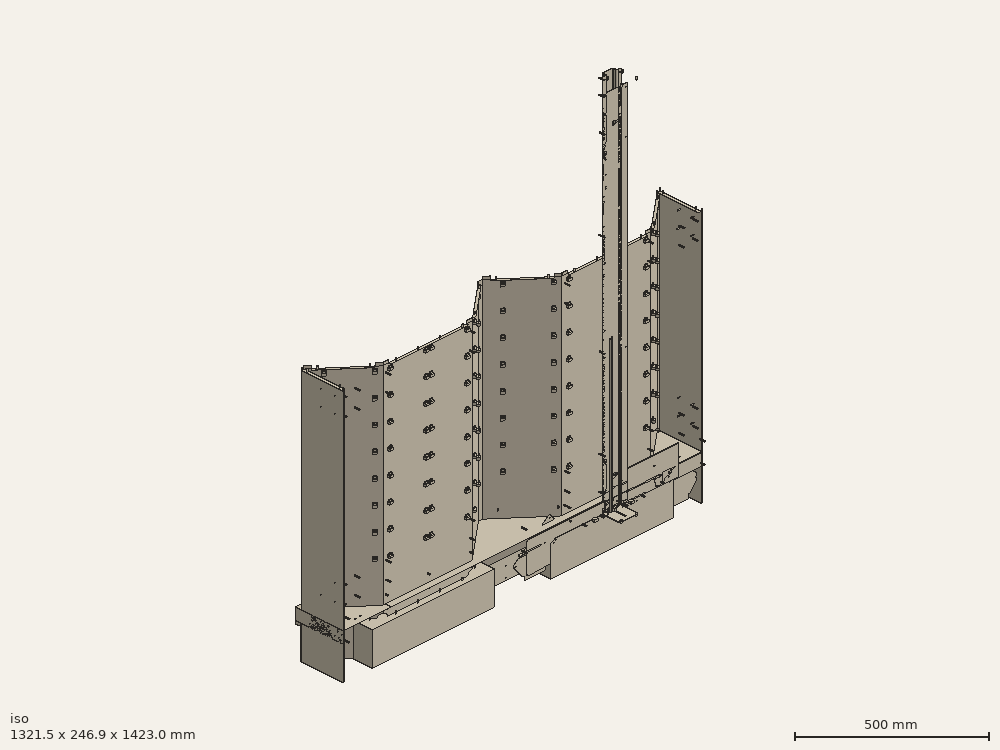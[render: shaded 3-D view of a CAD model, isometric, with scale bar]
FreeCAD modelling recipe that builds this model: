
FCSTD DOCUMENT  (FreeCAD 0.22R35209 (Git))
Label: composit_stand7
License: All rights reserved
LicenseURL: http://en.wikipedia.org/wiki/All_rights_reserved
objects: Sketcher::SketchObject×75, Part::FeaturePython×73, PartDesign::SubShapeBinder×27, Part::Compound×26, PartDesign::FeaturePython×20, PartDesign::Body×18, PartDesign::Pad×16, TechDraw::DrawViewPart×16, Part::Mirroring×15, PartDesign::Boolean×14, Part::Extrusion×12, PartDesign::Pocket×12, TechDraw::DrawViewDimension×10, PartDesign::Mirrored×9, App::DocumentObjectGroup×8, App::Part×5, TechDraw::DrawPage×5, PartDesign::Plane×4, Part::Part2DObjectPython×4, Part::Feature×4, +12 more types
note: 394 computed .brp shape members not serialized (recipe doc carries the construction recipe); baked Part::Feature solids carry a one-line shape summary decoded from their .brp
EXTERNAL_REF file=module.FCStd obj=Spreadsheet
EXTERNAL_REF file=module.FCStd obj=Sketch
EXTERNAL_REF file=dropper.FCStd obj=Part
EXTERNAL_REF file=module.FCStd obj=Body

FEATURE [Sketcher::SketchObject] Sketch  label="base_sketch"
  FullyConstrained = true
  expr: Constraints[19] = module#<<Properties>>.module_width * 2 + 2 mm
  expr: Constraints[20] = module#<<Properties>>.module_width + 2 mm
  sketch-geometry (11):
    g0: LineSegment StartX=0 StartY=21 StartZ=0 EndX=162.217 EndY=21 EndZ=0
    g1: LineSegment StartX=162.217 StartY=21 StartZ=0 EndX=319.002 EndY=154.059 EndZ=0
    g2: LineSegment StartX=0 StartY=57 StartZ=0 EndX=149 EndY=57 EndZ=0
    g3: LineSegment StartX=149 StartY=57 StartZ=0 EndX=263.366 EndY=154.059 EndZ=0
    g4: LineSegment StartX=149 StartY=21 StartZ=0 EndX=149 EndY=57 EndZ=0
    g5: LineSegment StartX=149 StartY=57 StartZ=0 EndX=172.294 EndY=29.5522 EndZ=0
    g6: LineSegment StartX=263.366 StartY=154.059 StartZ=0 EndX=286.66 EndY=126.611 EndZ=0
    g7: GeomPoint X=-149 Y=57 Z=0
    g8: GeomPoint X=-162.217 Y=21 Z=0
    g9: LineSegment StartX=162.217 StartY=21 StartZ=0 EndX=353.688 EndY=96 EndZ=0
    g10: LineSegment StartX=319.002 StartY=154.059 StartZ=0 EndX=263.366 EndY=154.059 EndZ=0
  constraints (35):
    c: Horizontal(g0)
    c: Coincident(g0,g1)
    c: PointOnObject(g0,g-2)
    c: DistanceY(g0) = 21  'offset'
    c: PointOnObject(g2,g-2)
    c: Horizontal(g2)
    c: Coincident(g2,g3)
    c: PointOnObject(g4,g0)
    c: Coincident(g4,g2)
    c: Coincident(g4,g5)
    c: PointOnObject(g5,g1)
    c: Perpendicular(g0,g4)
    c: Perpendicular(g1,g5)
    c: Equal(g4,g5)
    c: Perpendicular(g3,g5)
    c: Coincident(g6,g3)
    c: PointOnObject(g6,g1)
    c: Perpendicular(g3,g6)
    c: Symmetric(g7,g2,g-2)
    c: DistanceX(g7,g2) = 298
    c: Distance(g3) = 150
    c: DistanceY(g4,g4) = 36
    c: DistanceX(g0,g1) = 156.785
    c: DistanceX(g1) = 319.002  'width'
    c: Symmetric(g8,g0,g-2)
    c: DistanceX(g8,g0) = 324.434  'face_width'
    c: DistanceY(g1) = 154.059  'max_y'
    c: Coincident(g9,g0)
    c: Equal(g9,g1)
    c: DistanceY(g0,g9) = 75
    c: Angle(g9) = 0.373334
    c: Angle(g1) = 0.70372
    c: Coincident(g10,g3)
    c: Horizontal(g10)
    c: Coincident(g1,g10)
FEATURE [Part::Mirroring] Part__Mirroring  label="Sketch (Mirror #1)"
  Base = (0,0,0)
  Normal = (1,0,0)
  Source = -> Sketch
FEATURE [Part::FeaturePython] Connect  # WARN: FeaturePython — macro-defined, semantics opaque (R4)
  Objects = -> [Sketch,Part__Mirroring]
  Refine = true
  Tolerance = 0.0001
FEATURE [Sketcher::SketchObject] Sketch001  label="faces_bridge"
  ExternalGeometry = -> [Sketch]
  FullyConstrained = true
  sketch-geometry (3):
    g0: LineSegment StartX=319.002 StartY=154.059 StartZ=0 EndX=329.002 EndY=154.059 EndZ=0
    g1: LineSegment StartX=-319.002 StartY=154.059 StartZ=0 EndX=-326.502 EndY=154.059 EndZ=0
    g2: GeomPoint X=-334.002 Y=154.059 Z=0
  constraints (8):
    c: Coincident(g0,g-3)
    c: Horizontal(g0)
    c: Horizontal(g1)
    c: Symmetric(g1,g0,g-2)
    c: DistanceX(g1) = -326.502  'offset'
    c: Symmetric(g2,g1,g1)
    c: DistanceX(g2,g1) = 15
    c: DistanceX(g0,g0) = 10
FEATURE [Sketcher::SketchObject] Sketch002  label="wall"
  ExternalGeometry = -> [Sketch001]
  FullyConstrained = true
  sketch-geometry (1):
    g0: LineSegment StartX=329.002 StartY=154.059 StartZ=0 EndX=329.002 EndY=0 EndZ=0
  constraints (4):
    c: Coincident(g0,g-3)
    c: PointOnObject(g0,g-1)
    c: Vertical(g0)
    c: DistanceX(g0) = 329.002  'distance'
FEATURE [PartDesign::SubShapeBinder] Binder
  BindCopyOnChange = 0
  BindMode = 0
  ClaimChildren = true
  Context = -> Body [Binder.]
  Fuse = false
  MakeFace = true
  OffsetFill = false
  OffsetIntersection = false
  OffsetJoinType = 0
  OffsetOpenResult = false
  PartialLoad = false
  Placement = pos=(0,0,-115) rot=(0,0,1;0rad)
  Relative = false
  Support = -> [Connect002]
  _Version = 2
  expr: .Placement.Base.z = -<<Properties>>.bottom_extend
FEATURE [PartDesign::FeaturePython] BaseBend  # WARN: FeaturePython — macro-defined, semantics opaque (R4)
  BendSide = 0
  BendSketch = -> Binder
  MidPlane = false
  Reverse = false
  length = 870
  radius = 0.1
  thickness = 0.3
  expr: length = <<Properties>>.face_height - .BendSketch.Placement.Base.z * 1 mm
FEATURE [Spreadsheet::Sheet] Spreadsheet  label="Properties"
  cells = B2(number_of_modules)=8; C2(face_height)==755 mm; D2(rivet_d)==3.4 mm; E2(bottom_extend)==115 mm
FEATURE [Sketcher::SketchObject] Sketch003
  ExternalGeometry = -> [Sketch002]
  FullyConstrained = true
  sketch-geometry (1):
    g0: LineSegment StartX=326.002 StartY=0 StartZ=0 EndX=329.002 EndY=0 EndZ=0
  constraints (3):
    c: PointOnObject(g0,g-1)
    c: Coincident(g0,g-3)
    c: DistanceX(g0,g0) = 3
FEATURE [Part::FeaturePython] Connect001  # WARN: FeaturePython — macro-defined, semantics opaque (R4)
  Objects = -> [Connect,Sketch001,Sketch002,Sketch003]
  Tolerance = 0
FEATURE [Part::Mirroring] Part__Mirroring001  label="Connect001 (Mirror #2)"
  Base = (-326.502,0,0)
  Normal = (1,0,0)
  Source = -> Connect001
  expr: .Base.x = Sketch001.Constraints.offset
FEATURE [Part::FeaturePython] Connect002  # WARN: FeaturePython — macro-defined, semantics opaque (R4)
  Objects = -> [Connect001,Part__Mirroring001]
  Tolerance = 0
FEATURE [App::Link] Link  label="module_holes"
  LinkedObject = -> <external module.FCStd>#Sketch
FEATURE [Sketcher::SketchObject] Sketch004  label="modules_placements"
  ExternalGeometry = -> [Sketch]
  FullyConstrained = true
  sketch-geometry (14):
    g0: LineSegment StartX=0 StartY=57 StartZ=0 EndX=149 EndY=57 EndZ=0
    g1: LineSegment StartX=149 StartY=57 StartZ=0 EndX=262.604 EndY=153.412 EndZ=0
    g2: LineSegment StartX=149 StartY=21 StartZ=0 EndX=149 EndY=57 EndZ=0
    g3: LineSegment StartX=149 StartY=57 StartZ=0 EndX=172.294 EndY=29.5522 EndZ=0
    g4: LineSegment StartX=74.5 StartY=57 StartZ=0 EndX=74.5 EndY=21 EndZ=0
    g5: LineSegment StartX=205.802 StartY=105.206 StartZ=0 EndX=229.096 EndY=77.758 EndZ=0
    g6: LineSegment StartX=64.5 StartY=21 StartZ=0 EndX=74.5 EndY=21 EndZ=0
    g7: LineSegment StartX=74.5 StartY=21 StartZ=0 EndX=74.5 EndY=41 EndZ=0
    g8: LineSegment StartX=221.472 StartY=71.2874 StartZ=0 EndX=229.096 EndY=77.758 EndZ=0
    g9: LineSegment StartX=229.096 StartY=77.758 StartZ=0 EndX=216.155 EndY=93.0068 EndZ=0
    g10: LineSegment StartX=-84.5 StartY=21 StartZ=0 EndX=-74.5 EndY=21 EndZ=0
    g11: LineSegment StartX=-74.5 StartY=21 StartZ=0 EndX=-74.5 EndY=41 EndZ=0
    g12: LineSegment StartX=-236.72 StartY=84.2286 StartZ=0 EndX=-229.096 EndY=77.758 EndZ=0
    g13: LineSegment StartX=-229.096 StartY=77.758 StartZ=0 EndX=-216.155 EndY=93.0068 EndZ=0
  constraints (42):
    c: PointOnObject(g0,g-2)
    c: Horizontal(g0)
    c: Coincident(g1,g0)
    c: PointOnObject(g2,g-3)
    c: Coincident(g2,g0)
    c: Coincident(g2,g3)
    c: PointOnObject(g3,g-4)
    c: Perpendicular(g1,g3)
    c: Perpendicular(g-4,g3)
    c: Perpendicular(g0,g2)
    c: Equal(g3,g2)
    c: DistanceY(g2,g2) = 36
    c: PointOnObject(g4,g-3)
    c: Vertical(g4)
    c: PointOnObject(g5,g-4)
    c: Equal(g0,g1)
    c: Symmetric(g0,g1,g5)
    c: Perpendicular(g1,g5)
    c: Symmetric(g0,g0,g4)
    c: PointOnObject(g6,g-3)
    c: Coincident(g6,g4)
    c: Coincident(g6,g7)
    c: PointOnObject(g7,g4)
    c: PointOnObject(g8,g-4)
    c: Coincident(g8,g5)
    c: Coincident(g8,g9)
    c: PointOnObject(g9,g5)
    c: Equal(g6,g8)
    c: Equal(g7,g9)
    c: Distance(g6) = 10
    c: DistanceY(g7,g7) = 20
    c: Horizontal(g10)
    c: Coincident(g10,g11)
    c: Vertical(g11)
    c: Coincident(g12,g13)
    c: Perpendicular(g13,g12)
    c: Symmetric(g8,g12,g-2)
    c: Symmetric(g10,g6,g-2)
    c: Equal(g11,g7)
    c: Equal(g10,g6)
    c: Equal(g12,g8)
    c: Symmetric(g13,g9,g-2)
FEATURE [Part::Extrusion] Extrude
  Base = -> Link
  Dir = (0,0,1)
  DirMode = 2
  FaceMakerClass = Part::FaceMakerBullseye
  LengthFwd = 10
  LengthRev = 0
  Placement = pos=(0,0,0) rot=(1,0,0;1.5708rad)
  Solid = true
  Symmetric = false
FEATURE [PartDesign::Body] Body001  label="dummy_body"
  Origin = -> Origin001
FEATURE [Part::FeaturePython] Placment  # WARN: FeaturePython — macro-defined, semantics opaque (R4)
  AttacherType = Attacher::AttachEngine3D
  ExposePlacement = true
  MapMode = 49
  MarkerShape = 1
  MarkerSize = 20
  NumElements = 1
  Placement = pos=(74.5,21,0) rot=(0,0,1;0rad)
  Support = -> [Sketch004]
  Type = lattice2AttachablePlacement.AttachablePlacement
  isLattice = 1
FEATURE [Part::FeaturePython] PlacementSubsequence  # WARN: FeaturePython — macro-defined, semantics opaque (R4)
  Base = -> Placment
  CycleMode = 0
  ExposePlacement = false
  MarkerShape = 1
  MarkerSize = 0
  NumElements = 4
  Type = lattice2AttachablePlacement.AttachedPlacementSubsequence
  isLattice = 1
FEATURE [Part::FeaturePython] LinearArray  # WARN: FeaturePython — macro-defined, semantics opaque (R4)
  Alignment = 0
  CellStart = A1
  Count = 8
  Dir = (0,0,1)
  DirIsDriven = true
  DistributionLaw = 0
  DrivenProperty = 1
  EndInclusive = true
  ExposePlacement = false
  GeneratorMode = 1
  MarkerShape = 1
  MarkerSize = 0
  NumElements = 8
  OrientMode = 0
  Point = (0,0,0)
  PointIsDriven = true
  Reverse = false
  SpanEnd = 100
  SpanStart = 180
  Step = 80
  Type = lattice2LinearArray.LinearArray
  VSGVersion = 1
  Values = 180.0 | 260.0 | 340.0 | 420.0 | 500.0 | 580.0 | 660.0 | 740.0
  ValuesSource = 2
  isLattice = 1
  expr: Count = <<Properties>>.number_of_modules
  expr: Step = <<module>>#<<Properties>>.module_fixture_distance_y
FEATURE [Part::FeaturePython] Join  # WARN: FeaturePython — macro-defined, semantics opaque (R4)
  ExposePlacement = false
  Interleave = false
  Links = -> [PlacementSubsequence]
  MarkerShape = 1
  MarkerSize = 0
  NumElements = 4
  Type = lattice2JoinArrays.JoinArrays
  isLattice = 1
FEATURE [Part::FeaturePython] LinearArray001  label="faces_placements"  # WARN: FeaturePython — macro-defined, semantics opaque (R4)
  Alignment = 0
  CellStart = A1
  Count = 2
  Dir = (1,0,0)
  DirIsDriven = true
  DistributionLaw = 0
  DrivenProperty = 1
  EndInclusive = true
  ExposePlacement = false
  GeneratorMode = 0
  MarkerShape = 1
  MarkerSize = 0
  NumElements = 2
  OrientMode = 1
  Point = (0,0,0)
  PointIsDriven = true
  Reverse = false
  SpanEnd = -653.005
  SpanStart = 0
  Step = -653.005
  Type = lattice2LinearArray.LinearArray
  VSGVersion = 1
  Values = 0.0 | -653.0048374651761
  ValuesSource = 2
  isLattice = 1
  expr: SpanEnd = Sketch001.Constraints.offset * 2
FEATURE [Part::FeaturePython] Populate002  label="Populate LinearArray001 with Join"  # WARN: FeaturePython — macro-defined, semantics opaque (R4)
  Copying = 0
  ExposePlacement = false
  MarkerShape = 1
  MarkerSize = 0
  NumElements = 8
  Object = -> Join
  OutputCompounding = 0
  PlacementsTo = -> LinearArray001
  Referencing = 0
  Type = lattice2PopulateCopies.LatticePopulateCopies
  isLattice = 1
FEATURE [Part::FeaturePython] Populate  label="Populate Join001 with LinearArray"  # WARN: FeaturePython — macro-defined, semantics opaque (R4)
  Copying = 0
  ExposePlacement = false
  MarkerShape = 1
  MarkerSize = 0
  NumElements = 64
  Object = -> Populate002
  OutputCompounding = 0
  PlacementsTo = -> LinearArray
  Referencing = 0
  Type = lattice2PopulateCopies.LatticePopulateCopies
  isLattice = 1
FEATURE [Part::FeaturePython] Populate001  label="Populate Populate Join001 with LinearArray with Extrude"  # WARN: FeaturePython — macro-defined, semantics opaque (R4)
  Copying = 0
  ExposePlacement = false
  MarkerShape = 1
  MarkerSize = 0
  NumElements = 0
  Object = -> Extrude
  OutputCompounding = 1
  PlacementsTo = -> Populate
  Referencing = 0
  Type = lattice2PopulateCopies.LatticePopulateCopies
  isLattice = 0
FEATURE [PartDesign::FeaturePython] Extend  # WARN: FeaturePython — macro-defined, semantics opaque (R4)
  BaseFeature = -> BaseBend
  Offset = 0.02
  Refine = true
  UseSubtraction = false
  baseObject = -> BaseBend [Face1]
  gap1 = 0
  gap2 = 0
  length = 0
FEATURE [PartDesign::FeaturePython] Bend  # WARN: FeaturePython — macro-defined, semantics opaque (R4)
  AutoMiter = false
  BaseFeature = -> Extend
  BendType = 0
  LengthList = [0.1]
  LengthSpec = 0
  ReliefFactor = 0.7
  UseReliefFactor = false
  angle = 90
  baseObject = -> Extend [Edge17,Edge49,Edge199,Edge78,Edge108,Edge203,Edge138,Edge171]
  bendAList = [90]
  extend1 = 0
  extend2 = 0
  gap1 = 0
  gap2 = 0
  invert = false
  kfactor = 0.5
  length = 0.1
  maxExtendDist = 5
  minGap = 0.1
  minReliefGap = 1
  miterangle1 = 0
  miterangle2 = 0
  offset = 0
  radius = 0.1
  reliefType = 0
  reliefd = 1
  reliefw = 0.8
  sketchflip = false
  sketchinvert = false
  unfold = false
  expr: radius = BaseBend.radius
FEATURE [Sketcher::SketchObject] Sketch005  label="top_fix_lines"
  ExternalGeometry = -> [Sketch,Sketch002]
  FullyConstrained = true
  sketch-geometry (8):
    g0: LineSegment StartX=142.217 StartY=21 StartZ=0 EndX=142.217 EndY=20.5 EndZ=0
    g1: LineSegment StartX=177.466 StartY=33.9412 StartZ=0 EndX=177.789 EndY=33.56 EndZ=0
    g2: LineSegment StartX=303.754 StartY=141.118 StartZ=0 EndX=304.077 EndY=140.736 EndZ=0
    g3: LineSegment StartX=162.217 StartY=21 StartZ=0 EndX=177.466 EndY=33.9412 EndZ=0
    g4: LineSegment StartX=162.217 StartY=21 StartZ=0 EndX=142.217 EndY=21 EndZ=0
    g5: LineSegment StartX=319.002 StartY=154.059 StartZ=0 EndX=303.754 EndY=141.118 EndZ=0
    g6: LineSegment StartX=328.502 StartY=151.059 StartZ=0 EndX=329.002 EndY=151.059 EndZ=0
    g7: LineSegment StartX=328.502 StartY=2 StartZ=0 EndX=329.002 EndY=2 EndZ=0
  constraints (26):
    c: Vertical(g0)
    c: PointOnObject(g1,g-3)
    c: PointOnObject(g2,g-3)
    c: Perpendicular(g-3,g1)
    c: Perpendicular(g-3,g2)
    c: Equal(g0,g1)
    c: Equal(g1,g2)
    c: Horizontal(g0,g-3)
    c: DistanceY(g0,g0) = 0.5
    c: Distance(g-3,g1) = 20
    c: Coincident(g3,g-3)
    c: Coincident(g3,g1)
    c: Coincident(g4,g3)
    c: Coincident(g4,g0)
    c: Coincident(g5,g-3)
    c: Coincident(g5,g2)
    c: Equal(g5,g3)
    c: Equal(g3,g4)
    c: PointOnObject(g6,g-4)
    c: PointOnObject(g7,g-4)
    c: Equal(g2,g6)
    c: Equal(g6,g7)
    c: DistanceY(g-4,g7) = 2
    c: DistanceY(g6,g-4) = 3
    c: Horizontal(g7)
    c: Horizontal(g6)
FEATURE [Sketcher::SketchObject] Sketch006
  ExternalGeometry = -> [Sketch,Sketch005]
  FullyConstrained = true
  sketch-geometry (15):
    g0: LineSegment StartX=162.209 StartY=20.9935 StartZ=0 EndX=177.466 EndY=33.9412 EndZ=0
    g1: LineSegment StartX=177.466 StartY=33.9412 StartZ=0 EndX=177.789 EndY=33.56 EndZ=0
    g2: LineSegment StartX=177.789 StartY=33.56 StartZ=0 EndX=162.533 EndY=20.6123 EndZ=0
    g3: LineSegment StartX=162.533 StartY=20.6123 StartZ=0 EndX=162.209 EndY=20.9935 EndZ=0
    g4: LineSegment StartX=162.207 StartY=21 StartZ=0 EndX=142.217 EndY=21 EndZ=0
    g5: LineSegment StartX=142.217 StartY=21 StartZ=0 EndX=142.217 EndY=20.5 EndZ=0
    g6: LineSegment StartX=142.217 StartY=20.5 StartZ=0 EndX=162.207 EndY=20.5 EndZ=0
    g7: LineSegment StartX=162.207 StartY=20.5 StartZ=0 EndX=162.207 EndY=21 EndZ=0
    g8: LineSegment StartX=304.077 StartY=140.736 StartZ=0 EndX=319.318 EndY=153.671 EndZ=0
    g9: LineSegment StartX=319.318 StartY=153.671 StartZ=0 EndX=318.995 EndY=154.052 EndZ=0
    g10: LineSegment StartX=318.995 StartY=154.052 StartZ=0 EndX=303.754 EndY=141.118 EndZ=0
    g11: LineSegment StartX=303.754 StartY=141.118 StartZ=0 EndX=304.077 EndY=140.736 EndZ=0
    g12: LineSegment StartX=162.207 StartY=21 StartZ=0 EndX=162.217 EndY=21 EndZ=0
    g13: LineSegment StartX=162.217 StartY=21 StartZ=0 EndX=162.209 EndY=20.9935 EndZ=0
    g14: LineSegment StartX=318.995 StartY=154.052 StartZ=0 EndX=319.002 EndY=154.059 EndZ=0
  constraints (39):
    c: Coincident(g0,g1)
    c: Coincident(g1,g2)
    c: Coincident(g2,g3)
    c: Parallel(g0,g2)
    c: Parallel(g1,g3)
    c: Coincident(g4,g5)
    c: Coincident(g5,g6)
    c: Coincident(g6,g7)
    c: Coincident(g7,g4)
    c: Parallel(g4,g6)
    c: Parallel(g5,g7)
    c: Coincident(g8,g9)
    c: Coincident(g9,g10)
    c: Coincident(g10,g11)
    c: Coincident(g11,g8)
    c: Parallel(g8,g10)
    c: Parallel(g9,g11)
    c: Perpendicular(g1,g0)
    c: Perpendicular(g9,g8)
    c: Perpendicular(g5,g4)
    c: Coincident(g10,g-6)
    c: PointOnObject(g-6,g8)
    c: Coincident(g0,g-5)
    c: PointOnObject(g-5,g2)
    c: Coincident(g4,g-4)
    c: PointOnObject(g-4,g6)
    c: PointOnObject(g4,g-3)
    c: Coincident(g3,g0)
    c: PointOnObject(g0,g-7)
    c: Coincident(g12,g4)
    c: Coincident(g12,g-7)
    c: Coincident(g13,g12)
    c: Coincident(g13,g0)
    c: Equal(g12,g13)
    c: PointOnObject(g9,g-7)
    c: Coincident(g14,g9)
    c: Coincident(g14,g-7)
    c: Equal(g14,g13)
    c: DistanceX(g12,g12) = 0.01
FEATURE [Part::Mirroring] Part__Mirroring002  label="Sketch006 (Mirror #3)"
  Base = (0,0,0)
  Normal = (1,0,0)
  Source = -> Sketch006
FEATURE [Part::Compound] Compound001
  Links = -> [Sketch006,Part__Mirroring002]
FEATURE [Part::FeaturePython] Populate003  label="Populate LinearArray001 with Compound001"  # WARN: FeaturePython — macro-defined, semantics opaque (R4)
  Copying = 0
  ExposePlacement = false
  MarkerShape = 1
  MarkerSize = 0
  NumElements = 0
  Object = -> Compound001
  OutputCompounding = 1
  PlacementsTo = -> LinearArray001
  Referencing = 0
  Type = lattice2PopulateCopies.LatticePopulateCopies
  isLattice = 0
FEATURE [Sketcher::SketchObject] Sketch007
  ExternalGeometry = -> [Sketch002,Sketch005]
  FullyConstrained = true
  sketch-geometry (8):
    g0: LineSegment StartX=329.002 StartY=154.059 StartZ=0 EndX=328.502 EndY=154.059 EndZ=0
    g1: LineSegment StartX=328.502 StartY=154.059 StartZ=0 EndX=328.502 EndY=151.059 EndZ=0
    g2: LineSegment StartX=328.502 StartY=151.059 StartZ=0 EndX=329.002 EndY=151.059 EndZ=0
    g3: LineSegment StartX=329.002 StartY=151.059 StartZ=0 EndX=329.002 EndY=154.059 EndZ=0
    g4: LineSegment StartX=329.002 StartY=0 StartZ=0 EndX=328.502 EndY=0 EndZ=0
    g5: LineSegment StartX=328.502 StartY=0 StartZ=0 EndX=328.502 EndY=2 EndZ=0
    g6: LineSegment StartX=328.502 StartY=2 StartZ=0 EndX=329.002 EndY=2 EndZ=0
    g7: LineSegment StartX=329.002 StartY=2 StartZ=0 EndX=329.002 EndY=0 EndZ=0
  constraints (19):
    c: Coincident(g0,g1)
    c: Coincident(g1,g2)
    c: Coincident(g2,g3)
    c: Coincident(g3,g0)
    c: Horizontal(g0)
    c: Vertical(g1)
    c: Coincident(g0,g-3)
    c: Coincident(g4,g5)
    c: Coincident(g5,g6)
    c: Coincident(g6,g7)
    c: Coincident(g7,g4)
    c: Horizontal(g4)
    c: Horizontal(g6)
    c: Vertical(g5)
    c: Vertical(g7)
    c: Coincident(g4,g-3)
    c: Coincident(g2,g-4)
    c: Coincident(g1,g-4)
    c: Coincident(g5,g-5)
FEATURE [Part::Mirroring] Part__Mirroring003  label="Sketch007 (Mirror #4)"
  Base = (-326.502,0,0)
  Normal = (1,0,0)
  Source = -> Sketch007
  expr: .Base.x = Sketch001.Constraints.offset
FEATURE [Part::Compound] Compound002
  Links = -> [Sketch007,Populate003,Part__Mirroring003]
FEATURE [Part::Extrusion] Extrude001
  Base = -> Compound002
  Dir = (0,0,1)
  DirMode = 2
  FaceMakerClass = Part::FaceMakerBullseye
  LengthFwd = 10
  LengthRev = 0
  Placement = pos=(0,0,755) rot=(0,0,1;0rad)
  Solid = true
  Symmetric = false
  expr: .Placement.Base.z = <<Properties>>.face_height
FEATURE [Sketcher::SketchObject] Sketch008
  ExternalGeometry = -> [Sketch005]
  FullyConstrained = true
  sketch-geometry (7):
    g0: LineSegment StartX=182.966 StartY=27.4604 StartZ=0 EndX=309.254 EndY=134.637 EndZ=0
    g1: LineSegment StartX=309.254 StartY=134.637 StartZ=0 EndX=304.077 EndY=140.736 EndZ=0
    g2: LineSegment StartX=304.077 StartY=140.736 StartZ=0 EndX=177.789 EndY=33.56 EndZ=0
    g3: LineSegment StartX=177.789 StartY=33.56 StartZ=0 EndX=182.966 EndY=27.4604 EndZ=0
    g4: LineSegment StartX=142.217 StartY=20.5 StartZ=0 EndX=0 EndY=20.5 EndZ=0
    g5: LineSegment StartX=0 StartY=12.5 StartZ=0 EndX=142.217 EndY=12.5 EndZ=0
    g6: LineSegment StartX=142.217 StartY=12.5 StartZ=0 EndX=142.217 EndY=20.5 EndZ=0
  constraints (19):
    c: Coincident(g0,g1)
    c: Coincident(g1,g2)
    c: Coincident(g2,g3)
    c: Coincident(g3,g0)
    c: Parallel(g0,g2)
    c: Parallel(g1,g3)
    c: Perpendicular(g1,g0)
    c: Coincident(g1,g-5)
    c: Coincident(g2,g-4)
    c: Coincident(g5,g6)
    c: Coincident(g6,g4)
    c: Horizontal(g4)
    c: Horizontal(g5)
    c: Vertical(g6)
    c: Coincident(g4,g-3)
    c: PointOnObject(g5,g-2)
    c: PointOnObject(g4,g-2)
    c: Equal(g6,g3)
    c: DistanceY(g6,g6) = 8
FEATURE [Sketcher::SketchObject] Sketch009
  ExternalGeometry = -> [Sketch005]
  FullyConstrained = true
  sketch-geometry (6):
    g0: LineSegment StartX=328.502 StartY=151.059 StartZ=0 EndX=324.502 EndY=151.059 EndZ=0
    g1: LineSegment StartX=318.502 StartY=145.059 StartZ=0 EndX=318.502 EndY=2 EndZ=0
    g2: LineSegment StartX=318.502 StartY=2 StartZ=0 EndX=328.502 EndY=2 EndZ=0
    g3: LineSegment StartX=328.502 StartY=2 StartZ=0 EndX=328.502 EndY=151.059 EndZ=0
    g4: ArcOfCircle CenterX=324.502 CenterY=145.059 CenterZ=0 NormalX=0 NormalY=0 NormalZ=1 AngleXU=0 Radius=6 StartAngle=1.5708 EndAngle=3.14159
    g5: GeomPoint X=318.502 Y=151.059 Z=0
  constraints (14):
    c: Coincident(g1,g2)
    c: Coincident(g2,g3)
    c: Coincident(g3,g0)
    c: Horizontal(g0)
    c: Horizontal(g2)
    c: Vertical(g1)
    c: Coincident(g0,g-4)
    c: Coincident(g2,g-3)
    c: DistanceX(g2,g2) = 10
    c: PointOnObject(g5,g0)
    c: PointOnObject(g5,g1)
    c: Tangent(g0,g4) = -1.5708
    c: Tangent(g1,g4) = -1.5708
    c: Radius(g4) = 6
FEATURE [Part::Mirroring] Part__Mirroring004  label="Sketch008 (Mirror #5)"
  Base = (0,0,0)
  Normal = (1,0,0)
  Source = -> Sketch008
FEATURE [Part::Compound] Compound003
  Links = -> [Part__Mirroring004,Sketch008]
FEATURE [Part::FeaturePython] Populate004  label="Populate LinearArray001 with Compound003"  # WARN: FeaturePython — macro-defined, semantics opaque (R4)
  Copying = 0
  ExposePlacement = false
  MarkerShape = 1
  MarkerSize = 0
  NumElements = 0
  Object = -> Compound003
  OutputCompounding = 1
  PlacementsTo = -> LinearArray001
  Referencing = 0
  Type = lattice2PopulateCopies.LatticePopulateCopies
  isLattice = 0
FEATURE [Part::FeaturePython] Mirror  label="Mirror of Sketch009"  # WARN: FeaturePython — macro-defined, semantics opaque (R4)
  ExposePlacement = false
  FlipX = true
  FlipY = false
  FlipZ = false
  MarkerShape = 1
  MarkerSize = 0
  NumElements = 0
  Object = -> Sketch009
  ObjectTraversal = 0
  PivotPlacement = pos=(-326.502,0,0) rot=(0,0,1;0rad)
  Type = lattice2Mirror.LatticeMirror
  isLattice = 0
  expr: .PivotPlacement.Base.x = Sketch001.Constraints.offset
FEATURE [Part::Compound] Compound004
  Links = -> [Sketch009,Populate004,Mirror]
FEATURE [PartDesign::SubShapeBinder] Binder001
  BindCopyOnChange = 0
  BindMode = 0
  ClaimChildren = true
  Context = -> Body [Binder001.]
  Fuse = false
  MakeFace = true
  OffsetFill = false
  OffsetIntersection = false
  OffsetJoinType = 0
  OffsetOpenResult = false
  PartialLoad = false
  Placement = pos=(0,0,755.1) rot=(0,0,1;0rad)
  Relative = false
  Support = -> [Compound004]
  _Version = 2
  expr: .Placement.Base.z = <<Properties>>.face_height + <<BaseBend>>.radius
FEATURE [PartDesign::Pad] Pad
  BaseFeature = -> Bend
  Direction = (0,0,1)
  Length = 0.3
  Length2 = 10
  Profile = -> Binder001
  Type = 0
  expr: Length = <<BaseBend>>.thickness
FEATURE [Sketcher::SketchObject] Sketch010  label="top_base_sketch"
  ExternalGeometry = -> [Sketch]
  FullyConstrained = true
  Placement = pos=(0,0,0) rot=(0.57735,0.57735,0.57735;2.0944rad)
  sketch-geometry (2):
    g0: LineSegment StartX=-10 StartY=0 StartZ=0 EndX=154.059 EndY=0 EndZ=0
    g1: LineSegment StartX=154.059 StartY=0 StartZ=0 EndX=158.226 EndY=23.6354 EndZ=0
  constraints (6):
    c: Coincident(g0,g-3)
    c: Coincident(g1,g0)
    c: Angle(g1) = 1.39626
    c: PointOnObject(g0,g-1)
    c: DistanceX(g0) = -10
    c: Distance(g1) = 24
FEATURE [PartDesign::FeaturePython] BaseBend001  # WARN: FeaturePython — macro-defined, semantics opaque (R4)
  BendSide = 1
  BendSketch = -> Sketch010
  MidPlane = true
  Reverse = false
  length = 638.005
  radius = 0.1
  thickness = 0.3
  expr: length = <<base_sketch>>.Constraints.width * 2
FEATURE [Sketcher::SketchObject] Sketch011  label="top_cut"
  ExternalGeometry = -> [Sketch]
  FullyConstrained = true
  sketch-geometry (4):
    g0: LineSegment StartX=0 StartY=9 StartZ=0 EndX=166.623 EndY=9 EndZ=0
    g1: LineSegment StartX=166.623 StartY=9 StartZ=0 EndX=319.002 EndY=138.32 EndZ=0
    g2: LineSegment StartX=162.217 StartY=9 StartZ=0 EndX=162.217 EndY=21 EndZ=0
    g3: LineSegment StartX=162.217 StartY=21 StartZ=0 EndX=169.982 EndY=11.8507 EndZ=0
  constraints (13):
    c: PointOnObject(g0,g-2)
    c: Horizontal(g0)
    c: Coincident(g1,g0)
    c: PointOnObject(g2,g0)
    c: Coincident(g2,g-4)
    c: Coincident(g2,g3)
    c: PointOnObject(g3,g1)
    c: Perpendicular(g0,g2)
    c: Perpendicular(g1,g3)
    c: Perpendicular(g-3,g3)
    c: Equal(g3,g2)
    c: DistanceY(g2,g2) = 12
    c: Vertical(g1,g-3)
FEATURE [Sketcher::SketchObject] Sketch012
  ExternalGeometry = -> [Sketch011]
  FullyConstrained = false
  sketch-geometry (2):
    g0: LineSegment StartX=319.002 StartY=138.32 StartZ=0 EndX=319.002 EndY=-34.0475 EndZ=0
    g1: LineSegment StartX=319.002 StartY=-34.0475 StartZ=0 EndX=0 EndY=-34.0475 EndZ=0
  constraints (5):
    c: Coincident(g0,g-4)
    c: Vertical(g0)
    c: Coincident(g1,g0)
    c: PointOnObject(g1,g-2)
    c: Horizontal(g1)
FEATURE [Part::FeaturePython] Connect003  # WARN: FeaturePython — macro-defined, semantics opaque (R4)
  Objects = -> [Sketch011,Sketch012]
  Tolerance = 0
FEATURE [Part::Mirroring] Part__Mirroring005  label="Connect003 (Mirror #6)"
  Base = (0,0,0)
  Normal = (1,0,0)
  Source = -> Connect003
FEATURE [Part::FeaturePython] Connect004  # WARN: FeaturePython — macro-defined, semantics opaque (R4)
  Objects = -> [Connect003,Part__Mirroring005]
  Tolerance = 0
FEATURE [PartDesign::SubShapeBinder] Binder002
  BindCopyOnChange = 0
  BindMode = 0
  ClaimChildren = true
  Context = -> Part [Body002.Binder002.]
  Fuse = false
  MakeFace = true
  OffsetFill = false
  OffsetIntersection = false
  OffsetJoinType = 0
  OffsetOpenResult = false
  PartialLoad = false
  Relative = false
  Support = -> [Connect004]
  _Version = 2
FEATURE [PartDesign::Pocket] Pocket
  BaseFeature = -> BaseBend001
  Direction = (0,0,-1)
  Length = 5
  Length2 = 5
  Midplane = true
  Profile = -> Binder002
  Refine = true
  Type = 1
FEATURE [PartDesign::FeaturePython] Bend001  # WARN: FeaturePython — macro-defined, semantics opaque (R4)
  AutoMiter = false
  BaseFeature = -> Pocket
  BendType = 1
  LengthList = [20]
  LengthSpec = 0
  ReliefFactor = 0.7
  UseReliefFactor = false
  angle = 90
  baseObject = -> Pocket [Edge27,Edge29,Edge32,Edge33,Edge26]
  bendAList = [90]
  extend1 = 0
  extend2 = 0
  gap1 = 0
  gap2 = 0
  invert = false
  kfactor = 0.5
  length = 20
  maxExtendDist = 5
  minGap = 0.1
  minReliefGap = 1
  miterangle1 = 0
  miterangle2 = 0
  offset = 0
  radius = 0.1
  reliefType = 0
  reliefd = 1
  reliefw = 0.8
  sketchflip = false
  sketchinvert = false
  unfold = false
  expr: radius = BaseBend001.radius
FEATURE [PartDesign::SubShapeBinder] Binder003
  BindCopyOnChange = 0
  BindMode = 0
  ClaimChildren = false
  Context = -> Part [Body002.Binder003.]
  Fuse = false
  MakeFace = true
  OffsetFill = false
  OffsetIntersection = false
  OffsetJoinType = 0
  OffsetOpenResult = false
  PartialLoad = false
  Relative = true
  Support = -> [Sketch,Sketch011]
  _Version = 2
  expr: Support = list(<<top_cut>>._self; <<base_sketch>>._self)
FEATURE [Sketcher::SketchObject] Sketch013
  ExternalGeometry = -> [Binder003]
  FullyConstrained = true
  MapMode = 5
  Support = -> [XY_Plane003]
  sketch-geometry (12):
    g0: LineSegment StartX=167.462 StartY=9.71268 StartZ=0 EndX=165.521 EndY=12 EndZ=0
    g1: LineSegment StartX=165.521 StartY=12 StartZ=0 EndX=165.521 EndY=9 EndZ=0
    g2: LineSegment StartX=165.521 StartY=9 StartZ=0 EndX=166.623 EndY=9 EndZ=0
    g3: LineSegment StartX=166.623 StartY=9 StartZ=0 EndX=167.462 EndY=9.71268 EndZ=0
    g4: LineSegment StartX=319.002 StartY=138.32 StartZ=0 EndX=319.002 EndY=138.32 EndZ=0
    g5: LineSegment StartX=319.002 StartY=138.32 StartZ=0 EndX=317.061 EndY=140.607 EndZ=0
    g6: LineSegment StartX=317.061 StartY=140.607 StartZ=0 EndX=319.002 EndY=138.32 EndZ=0
    g7: LineSegment StartX=319.002 StartY=138.32 StartZ=0 EndX=319.002 EndY=138.32 EndZ=0
    g8: LineSegment StartX=319.002 StartY=153.759 StartZ=0 EndX=318.602 EndY=153.759 EndZ=0
    g9: LineSegment StartX=318.602 StartY=153.759 StartZ=0 EndX=318.602 EndY=150.759 EndZ=0
    g10: LineSegment StartX=318.602 StartY=150.759 StartZ=0 EndX=319.002 EndY=150.759 EndZ=0
    g11: LineSegment StartX=319.002 StartY=150.759 StartZ=0 EndX=319.002 EndY=153.759 EndZ=0
  constraints (34):
    c: Coincident(g0,g1)
    c: Coincident(g1,g2)
    c: Coincident(g3,g0)
    c: Coincident(g5,g6)
    c: Coincident(g6,g7)
    c: Perpendicular(g4,g5)
    c: Perpendicular(g7,g6)
    c: Equal(g0,g1)
    c: Equal(g1,g5)
    c: Equal(g5,g6)
    c: Coincident(g8,g9)
    c: Coincident(g9,g10)
    c: Coincident(g10,g11)
    c: Horizontal(g8)
    c: Horizontal(g10)
    c: Vertical(g9)
    c: Vertical(g11)
    c: Equal(g11,g6)
    c: Coincident(g2,g3)
    c: Coincident(g2,g-4)
    c: PointOnObject(g0,g-4)
    c: Horizontal(g2)
    c: Perpendicular(g2,g1)
    c: Perpendicular(g3,g0)
    c: DistanceY(g1,g1) = 3
    c: DistanceX(g10,g10) = 0.4
    c: Coincident(g11,g8)
    c: Vertical(g8,g-3)
    c: DistanceY(g8,g-3) = 0.3
    c: Coincident(g7,g4)
    c: Coincident(g5,g4)
    c: PointOnObject(g6,g-4)
    c: Coincident(g4,g-4)
    c: Vertical(g4)
FEATURE [PartDesign::Pocket] Pocket001
  BaseFeature = -> Bend001
  Direction = (0,0,-1)
  Length = 5
  Length2 = 5
  Profile = -> Sketch013
  ReferenceAxis = -> Sketch013 [N_Axis]
  Reversed = true
  Type = 1
FEATURE [PartDesign::Mirrored] Mirrored
  BaseFeature = -> Pocket001
  MirrorPlane = -> Sketch013 [V_Axis]
  Originals = -> [Pocket001]
FEATURE [Sketcher::SketchObject] Sketch014
  ExternalGeometry = -> [Sketch005]
  FullyConstrained = true
  expr: Constraints[10] = <<Properties>>.rivet_d
  expr: Constraints[34] = <<Properties>>.rivet_d / 2 + 3 mm + 1 mm
  sketch-geometry (16):
    g0: LineSegment StartX=142.217 StartY=21 StartZ=0 EndX=0 EndY=21 EndZ=0
    g1: LineSegment StartX=177.466 StartY=33.9412 StartZ=0 EndX=303.754 EndY=141.118 EndZ=0
    g2: Circle CenterX=122.217 CenterY=15.3 CenterZ=0 NormalX=0 NormalY=0 NormalZ=1 AngleXU=0 Radius=1.7
    g3: Circle CenterX=40.739 CenterY=15.3 CenterZ=0 NormalX=0 NormalY=0 NormalZ=1 AngleXU=0 Radius=1.7
    g4: Circle CenterX=192.591 CenterY=39.3011 CenterZ=0 NormalX=0 NormalY=0 NormalZ=1 AngleXU=0 Radius=1.7
    g5: Circle CenterX=296.005 CenterY=127.066 CenterZ=0 NormalX=0 NormalY=0 NormalZ=1 AngleXU=0 Radius=1.7
    g6: Circle CenterX=0 CenterY=0 CenterZ=0 NormalX=0 NormalY=0 NormalZ=1 AngleXU=0 Radius=1.7
    g7: LineSegment StartX=0 StartY=15.3 StartZ=0 EndX=40.739 EndY=15.3 EndZ=0
    g8: LineSegment StartX=40.739 StartY=15.3 StartZ=0 EndX=81.478 EndY=15.3 EndZ=0
    g9: LineSegment StartX=81.478 StartY=15.3 StartZ=0 EndX=122.217 EndY=15.3 EndZ=0
    g10: LineSegment StartX=122.217 StartY=15.3 StartZ=0 EndX=142.217 EndY=15.3 EndZ=0
    g11: LineSegment StartX=122.217 StartY=15.3 StartZ=0 EndX=122.217 EndY=21 EndZ=0
    g12: LineSegment StartX=192.591 StartY=39.3011 StartZ=0 EndX=296.005 EndY=127.066 EndZ=0
    g13: LineSegment StartX=192.591 StartY=39.3011 StartZ=0 EndX=188.902 EndY=43.6471 EndZ=0
    g14: LineSegment StartX=177.466 StartY=33.9412 StartZ=0 EndX=192.591 EndY=39.3011 EndZ=0
    g15: LineSegment StartX=303.754 StartY=141.118 StartZ=0 EndX=296.005 EndY=127.066 EndZ=0
  constraints (42):
    c: Coincident(g0,g-3)
    c: PointOnObject(g0,g-2)
    c: Horizontal(g0)
    c: Coincident(g1,g-4)
    c: Coincident(g1,g-5)
    c: Coincident(g6,g-1)
    c: Equal(g6,g3)
    c: Equal(g6,g2)
    c: Equal(g6,g4)
    c: Equal(g6,g5)
    c: Diameter(g6) = 3.4
    c: PointOnObject(g7,g-2)
    c: Coincident(g7,g3)
    c: Horizontal(g7)
    c: Coincident(g8,g3)
    c: Horizontal(g8)
    c: Coincident(g9,g8)
    c: Coincident(g9,g2)
    c: Horizontal(g9)
    c: Coincident(g10,g2)
    c: Horizontal(g10)
    c: Vertical(g10,g0)
    c: Equal(g7,g8)
    c: Equal(g8,g9)
    c: DistanceX(g10,g10) = 20
    c: Coincident(g11,g2)
    c: PointOnObject(g11,g0)
    c: Vertical(g11)
    c: Coincident(g12,g4)
    c: Coincident(g12,g5)
    c: Coincident(g13,g4)
    c: PointOnObject(g13,g1)
    c: Parallel(g12,g1)
    c: Equal(g13,g11)
    c: DistanceY(g11,g11) = 5.7
    c: Coincident(g14,g1)
    c: Coincident(g14,g4)
    c: Coincident(g15,g1)
    c: Coincident(g15,g5)
    c: Equal(g15,g14)
    c: Perpendicular(g1,g13)
    c: Distance(g1,g13) = 15
FEATURE [Sketcher::SketchObject] Sketch015
  ExternalGeometry = -> [Sketch005]
  FullyConstrained = true
  expr: Constraints[13] = <<Properties>>.rivet_d / 2 + 3 mm + 1 mm
  expr: Constraints[3] = <<Properties>>.rivet_d
  sketch-geometry (6):
    g0: Circle CenterX=323.302 CenterY=17 CenterZ=0 NormalX=0 NormalY=0 NormalZ=1 AngleXU=0 Radius=1.7
    g1: Circle CenterX=323.302 CenterY=136.059 CenterZ=0 NormalX=0 NormalY=0 NormalZ=1 AngleXU=0 Radius=1.7
    g2: Circle CenterX=0 CenterY=0 CenterZ=0 NormalX=0 NormalY=0 NormalZ=1 AngleXU=0 Radius=1.7
    g3: LineSegment StartX=329.002 StartY=2 StartZ=0 EndX=329.002 EndY=151.059 EndZ=0
    g4: LineSegment StartX=323.302 StartY=136.059 StartZ=0 EndX=329.002 EndY=136.059 EndZ=0
    g5: LineSegment StartX=323.302 StartY=17 StartZ=0 EndX=329.002 EndY=17 EndZ=0
  constraints (16):
    c: Coincident(g2,g-1)
    c: Equal(g2,g0)
    c: Equal(g2,g1)
    c: Diameter(g2) = 3.4
    c: Coincident(g3,g-4)
    c: Coincident(g3,g-3)
    c: Coincident(g4,g1)
    c: PointOnObject(g4,g3)
    c: Horizontal(g4)
    c: Coincident(g5,g0)
    c: PointOnObject(g5,g3)
    c: Horizontal(g5)
    c: Equal(g5,g4)
    c: DistanceX(g5,g5) = 5.7
    c: DistanceY(g3,g5) = 15
    c: DistanceY(g4,g3) = 15
FEATURE [Part::Mirroring] Part__Mirroring006  label="Sketch014 (Mirror #7)"
  Base = (0,0,0)
  Normal = (1,0,0)
  Source = -> Sketch014
FEATURE [Part::Compound] Compound005
  Links = -> [Part__Mirroring006,Sketch014,Sketch015]
FEATURE [Part::Mirroring] Part__Mirroring007  label="Compound005 (Mirror #8)"
  Base = (-326.502,0,0)
  Normal = (1,0,0)
  Source = -> Compound005
  expr: .Base.x = <<faces_bridge>>.Constraints.offset
FEATURE [Part::Compound] Compound006
  Links = -> [Part__Mirroring007,Compound005]
FEATURE [Part::Extrusion] Extrude002
  Base = -> Compound006
  Dir = (0,0,1)
  DirMode = 2
  FaceMakerClass = Part::FaceMakerBullseye
  LengthFwd = 10
  LengthRev = 0
  Solid = true
  Symmetric = false
FEATURE [Part::FeaturePython] Placment001  label="top_placement"  # WARN: FeaturePython — macro-defined, semantics opaque (R4)
  AttacherType = Attacher::AttachEngine3D
  ExposePlacement = true
  MarkerShape = 1
  MarkerSize = 100
  NumElements = 1
  Placement = pos=(0,0,755) rot=(0,0,1;0rad)
  Type = lattice2AttachablePlacement.AttachablePlacement
  isLattice = 1
  expr: .Placement.Base.z = <<Properties>>.face_height
FEATURE [Part::FeaturePython] Populate005  label="Populate top_placement with Extrude002"  # WARN: FeaturePython — macro-defined, semantics opaque (R4)
  Copying = 0
  ExposePlacement = false
  MarkerShape = 1
  MarkerSize = 0
  NumElements = 0
  Object = -> Extrude002
  OutputCompounding = 2
  PlacementsTo = -> Placment001
  Referencing = 0
  Type = lattice2PopulateCopies.LatticePopulateCopies
  isLattice = 0
FEATURE [PartDesign::SubShapeBinder] Binder004
  BindCopyOnChange = 0
  BindMode = 0
  ClaimChildren = false
  Fuse = false
  MakeFace = true
  Offset = 0.5
  OffsetFill = false
  OffsetIntersection = false
  OffsetJoinType = 0
  OffsetOpenResult = false
  PartialLoad = false
  Relative = true
  Support = -> [<external dropper.FCStd>#Part[Body.Binder.Connect.]]
  _Version = 2
FEATURE [PartDesign::SubShapeBinder] Binder005
  BindCopyOnChange = 0
  BindMode = 0
  ClaimChildren = false
  Fuse = false
  MakeFace = true
  OffsetFill = false
  OffsetIntersection = false
  OffsetJoinType = 0
  OffsetOpenResult = false
  PartialLoad = false
  Relative = true
  Support = -> [<external dropper.FCStd>#Part[Body001.Sketch007.]]
  _Version = 2
FEATURE [Part::FeaturePython] LinearArray002  # WARN: FeaturePython — macro-defined, semantics opaque (R4)
  Alignment = 0
  CellStart = A1
  Count = 2
  Dir = (1,0,0)
  DirIsDriven = true
  DistributionLaw = 0
  DrivenProperty = 1
  EndInclusive = true
  ExposePlacement = false
  GeneratorMode = 0
  MarkerShape = 1
  MarkerSize = 0
  NumElements = 2
  OrientMode = 1
  Placement = pos=(-32.5,13.8,0) rot=(0,0,1;0rad)
  Point = (0,0,0)
  PointIsDriven = true
  Reverse = false
  SpanEnd = 65
  SpanStart = 0
  Step = 65
  Type = lattice2LinearArray.LinearArray
  VSGVersion = 1
  Values = 0.0 | 65.0
  ValuesSource = 2
  isLattice = 1
  expr: .Placement.Base.x = -SpanEnd / 2
  expr: .Placement.Base.y = 11.8 + 2
FEATURE [Part::Compound] Compound008
  Links = -> [Binder004,Binder005]
FEATURE [Part::FeaturePython] FuseCompound  # WARN: FeaturePython — macro-defined, semantics opaque (R4)
  Base = -> Compound008
  Refine = true
  recomputeQuota = -1
FEATURE [Part::Extrusion] Extrude003
  Base = -> FuseCompound
  Dir = (0,0,1)
  DirMode = 2
  FaceMakerClass = Part::FaceMakerBullseye
  LengthFwd = 2.5
  LengthRev = 0
  Solid = false
  Symmetric = false
FEATURE [Part::FeaturePython] Populate006  label="Populate Join with LinearArray002"  # WARN: FeaturePython — macro-defined, semantics opaque (R4)
  Copying = 0
  ExposePlacement = false
  MarkerShape = 1
  MarkerSize = 0
  NumElements = 8
  Object = -> LinearArray002
  OutputCompounding = 0
  PlacementsTo = -> Join
  Referencing = 0
  Type = lattice2PopulateCopies.LatticePopulateCopies
  isLattice = 1
FEATURE [Part::Extrusion] Extrude004
  Base = -> Binder005
  Dir = (0,0,1)
  DirMode = 2
  FaceMakerClass = Part::FaceMakerBullseye
  LengthFwd = 10
  LengthRev = 0
  Solid = false
  Symmetric = false
FEATURE [Part::FeaturePython] Populate008  label="Populate Populate Join with LinearArray002 with Extrude004"  # WARN: FeaturePython — macro-defined, semantics opaque (R4)
  Copying = 0
  ExposePlacement = false
  MarkerShape = 1
  MarkerSize = 0
  NumElements = 0
  Object = -> Extrude004
  OutputCompounding = 1
  PlacementsTo = -> Populate006
  Referencing = 0
  Type = lattice2PopulateCopies.LatticePopulateCopies
  isLattice = 0
FEATURE [PartDesign::SubShapeBinder] Binder006
  BindCopyOnChange = 0
  BindMode = 0
  ClaimChildren = false
  Context = -> Part [Body003.Binder006.]
  Fuse = false
  MakeFace = true
  OffsetFill = false
  OffsetIntersection = false
  OffsetJoinType = 0
  OffsetOpenResult = false
  PartialLoad = false
  Relative = false
  Support = -> [Sketch011]
  _Version = 2
FEATURE [PartDesign::SubShapeBinder] Binder007
  BindCopyOnChange = 0
  BindMode = 0
  ClaimChildren = false
  Fuse = false
  MakeFace = true
  OffsetFill = false
  OffsetIntersection = false
  OffsetJoinType = 0
  OffsetOpenResult = false
  PartialLoad = false
  Relative = true
  Support = -> [<external dropper.FCStd>#Part[Body.Sketch008.]]
  _Version = 2
FEATURE [Part::Extrusion] Extrude005
  Base = -> Binder007
  Dir = (0,0,1)
  DirMode = 2
  FaceMakerClass = Part::FaceMakerBullseye
  LengthFwd = 10
  LengthRev = 0
  Solid = false
  Symmetric = false
FEATURE [Part::Box] Box  label="Cube"
  AttacherType = Attacher::AttachEngine3D
  AttachmentOffset = pos=(0,-5,0) rot=(0,0,1;0rad)
  Height = 2.5
  Length = 3.2
  Placement = pos=(-1.6,-50,0) rot=(0,0,1;0rad)
  Width = 100
  expr: .Placement.Base.x = -Length / 2
  expr: .Placement.Base.y = -Width / 2
  expr: Height = <<Extrude003>>.LengthFwd
FEATURE [Part::MultiFuse] Fusion
  Refine = true
  Shapes = -> [Extrude003,Extrude005,Box]
FEATURE [Part::FeaturePython] Populate009  label="Populate Populate Join with LinearArray002 with Fusion"  # WARN: FeaturePython — macro-defined, semantics opaque (R4)
  Copying = 0
  ExposePlacement = false
  MarkerShape = 1
  MarkerSize = 0
  NumElements = 0
  Object = -> Fusion
  OutputCompounding = 1
  PlacementsTo = -> Populate006
  Referencing = 0
  Type = lattice2PopulateCopies.LatticePopulateCopies
  isLattice = 0
FEATURE [PartDesign::SubShapeBinder] Binder008
  BindCopyOnChange = 0
  BindMode = 0
  ClaimChildren = false
  Context = -> Part [Body003.Binder008.]
  Fuse = false
  MakeFace = true
  OffsetFill = false
  OffsetIntersection = false
  OffsetJoinType = 0
  OffsetOpenResult = false
  PartialLoad = false
  Relative = true
  Support = -> [Sketch]
  _Version = 2
  expr: Support = <<base_sketch>>._self
FEATURE [Sketcher::SketchObject] Sketch016
  ExternalGeometry = -> [Binder006,Binder008]
  FullyConstrained = true
  MapMode = 5
  Support = -> [XY_Plane004]
  expr: Constraints[45] = <<base_sketch>>.Constraints.offset + LinearArray002.Placement.Base.y + 11.8 mm
  sketch-geometry (17):
    g0: LineSegment StartX=166.623 StartY=9 StartZ=0 EndX=167.462 EndY=9.71268 EndZ=0
    g1: LineSegment StartX=167.462 StartY=9.71268 StartZ=0 EndX=165.521 EndY=12 EndZ=0
    g2: LineSegment StartX=165.521 StartY=12 StartZ=0 EndX=165.521 EndY=9 EndZ=0
    g3: LineSegment StartX=165.521 StartY=9 StartZ=0 EndX=166.623 EndY=9 EndZ=0
    g4: LineSegment StartX=0 StartY=12 StartZ=0 EndX=165.521 EndY=12 EndZ=0
    g5: LineSegment StartX=165.521 StartY=12 StartZ=0 EndX=312.059 EndY=136.362 EndZ=0
    g6: LineSegment StartX=149.757 StartY=46.6 StartZ=0 EndX=0 EndY=46.6 EndZ=0
    g7: LineSegment StartX=0 StartY=46.6 StartZ=0 EndX=0 EndY=12 EndZ=0
    g8: ArcOfCircle CenterX=149.757 CenterY=54.9388 CenterZ=0 NormalX=0 NormalY=0 NormalZ=1 AngleXU=0 Radius=8.33877 StartAngle=4.71239 EndAngle=5.41611
    g9: GeomPoint X=152.818 Y=46.6 Z=0
    g10: LineSegment StartX=152.818 StartY=46.6 StartZ=0 EndX=152.818 EndY=9 EndZ=0
    g11: LineSegment StartX=155.152 StartY=48.581 StartZ=0 EndX=275.904 EndY=151.059 EndZ=0
    g12: LineSegment StartX=152.818 StartY=46.6 StartZ=0 EndX=177.148 EndY=17.9322 EndZ=0
    g13: LineSegment StartX=275.904 StartY=151.059 StartZ=0 EndX=306.664 EndY=151.059 EndZ=0
    g14: ArcOfCircle CenterX=306.664 CenterY=142.72 CenterZ=0 NormalX=0 NormalY=0 NormalZ=1 AngleXU=0 Radius=8.33877 StartAngle=5.41611 EndAngle=7.85398
    g15: GeomPoint X=329.377 Y=151.059 Z=0
    g16: LineSegment StartX=315.002 StartY=134.925 StartZ=0 EndX=315.002 EndY=150.664 EndZ=0
  constraints (46):
    c: Coincident(g-4,g0)
    c: PointOnObject(g0,g-3)
    c: Coincident(g0,g1)
    c: Coincident(g1,g2)
    c: PointOnObject(g2,g-4)
    c: Vertical(g2)
    c: Coincident(g2,g3)
    c: Coincident(g3,g0)
    c: Perpendicular(g1,g0)
    c: Equal(g1,g2)
    c: PointOnObject(g4,g-2)
    c: Coincident(g4,g1)
    c: Coincident(g5,g4)
    c: PointOnObject(g6,g-2)
    c: Coincident(g7,g6)
    c: Coincident(g7,g4)
    c: Horizontal(g4)
    c: Perpendicular(g5,g1)
    c: PointOnObject(g9,g6)
    c: Tangent(g6,g8) = 1.5708
    c: Coincident(g10,g9)
    c: Vertical(g10)
    c: PointOnObject(g10,g-4)
    c: DistanceY(g2,g2) = 3
    c: PointOnObject(g9,g11)
    c: Tangent(g11,g8) = -1.5708
    c: Parallel(g11,g5)
    c: Perpendicular(g7,g6)
    c: Coincident(g12,g9)
    c: PointOnObject(g12,g-3)
    c: Perpendicular(g-3,g12)
    c: Horizontal(g13)
    c: DistanceY(g15,g-5) = 3
    c: Coincident(g13,g11)
    c: PointOnObject(g15,g5)
    c: PointOnObject(g15,g13)
    c: Tangent(g5,g14) = -1.5708
    c: Tangent(g13,g14) = 1.5708
    c: PointOnObject(g16,g-3)
    c: PointOnObject(g16,g-5)
    c: Vertical(g16)
    c: Distance(g-3,g16) = 4
    c: Tangent(g16,g14)
    c: Equal(g10,g12)
    c: Equal(g8,g14)
    c: DistanceY(g6) = 46.6
FEATURE [PartDesign::Pad] Pad001
  Direction = (0,0,1)
  Length = 5
  Length2 = 10
  Profile = -> Sketch016
  ReferenceAxis = -> Sketch016 [N_Axis]
  Type = 0
FEATURE [PartDesign::Mirrored] Mirrored001
  BaseFeature = -> Pad001
  MirrorPlane = -> Sketch016 [V_Axis]
  Originals = -> [Pad001]
  Refine = true
FEATURE [PartDesign::SubShapeBinder] Binder009
  BindCopyOnChange = 0
  BindMode = 0
  ClaimChildren = false
  Context = -> Part [Body004.Binder009.]
  Fuse = false
  MakeFace = true
  OffsetFill = false
  OffsetIntersection = false
  OffsetJoinType = 0
  OffsetOpenResult = false
  PartialLoad = false
  Relative = false
  Support = -> [Sketch002,Sketch011]
  _Version = 2
  expr: Support = list(<<wall>>._self; <<top_cut>>._self)
FEATURE [Sketcher::SketchObject] Sketch017
  ExternalGeometry = -> [Binder009]
  FullyConstrained = true
  MapMode = 5
  Support = -> [XY_Plane005]
  sketch-geometry (4):
    g0: LineSegment StartX=166.623 StartY=9 StartZ=0 EndX=326.002 EndY=9 EndZ=0
    g1: LineSegment StartX=326.002 StartY=9 StartZ=0 EndX=326.002 EndY=138.32 EndZ=0
    g2: LineSegment StartX=326.002 StartY=138.32 StartZ=0 EndX=319.002 EndY=138.32 EndZ=0
    g3: LineSegment StartX=319.002 StartY=138.32 StartZ=0 EndX=166.623 EndY=9 EndZ=0
  constraints (10):
    c: Horizontal(g0)
    c: Coincident(g0,g1)
    c: Vertical(g1)
    c: Coincident(g1,g2)
    c: Horizontal(g2)
    c: Coincident(g2,g3)
    c: Coincident(g3,g0)
    c: DistanceX(g0,g-3) = 3
    c: Coincident(g2,g-4)
    c: Coincident(g0,g-4)
FEATURE [PartDesign::FeaturePython] BaseBend002  # WARN: FeaturePython — macro-defined, semantics opaque (R4)
  BendSide = 0
  BendSketch = -> Sketch017
  MidPlane = false
  Reverse = false
  length = 100
  radius = 0.1
  thickness = 0.3
FEATURE [PartDesign::FeaturePython] Bend002  # WARN: FeaturePython — macro-defined, semantics opaque (R4)
  AutoMiter = true
  BaseFeature = -> BaseBend002
  BendType = 1
  LengthList = [20]
  LengthSpec = 0
  ReliefFactor = 0.7
  UseReliefFactor = false
  angle = 90
  baseObject = -> BaseBend002 [Edge11]
  bendAList = [90]
  extend1 = 0
  extend2 = 0
  gap1 = 0
  gap2 = 0
  invert = false
  kfactor = 0.5
  length = 20
  maxExtendDist = 5
  minGap = 0.1
  minReliefGap = 1
  miterangle1 = 0
  miterangle2 = 0
  offset = 0
  radius = 0.1
  reliefType = 0
  reliefd = 1
  reliefw = 0.8
  sketchflip = false
  sketchinvert = false
  unfold = false
  expr: radius = BaseBend.radius
FEATURE [Sketcher::SketchObject] Sketch018  label="cap_base_sketch"
  ExternalGeometry = -> [Sketch002]
  FullyConstrained = false
  expr: Constraints[7] = <<faces_bridge>>.Constraints.offset
  sketch-geometry (4):
    g0: LineSegment StartX=329.002 StartY=0 StartZ=0 EndX=329.002 EndY=175.034 EndZ=0
    g1: LineSegment StartX=329.002 StartY=175.034 StartZ=0 EndX=-982.007 EndY=175.034 EndZ=0
    g2: LineSegment StartX=-982.007 StartY=175.034 StartZ=0 EndX=-982.007 EndY=0 EndZ=0
    g3: GeomPoint X=-326.502 Y=0 Z=0
  constraints (11):
    c: Vertical(g0)
    c: Coincident(g0,g1)
    c: Horizontal(g1)
    c: Coincident(g1,g2)
    c: PointOnObject(g2,g-1)
    c: Vertical(g2)
    c: PointOnObject(g3,g-1)
    c: DistanceX(g3) = -326.502
    c: Symmetric(g0,g2,g3)
    c: PointOnObject(g0,g-3)
    c: DistanceY(g0,g0) = 175.034  'cap_length'
FEATURE [PartDesign::SubShapeBinder] Binder010
  BindCopyOnChange = 0
  BindMode = 0
  ClaimChildren = true
  Context = -> Part [Part001.Body005.Binder010.]
  Fuse = false
  MakeFace = true
  OffsetFill = false
  OffsetIntersection = false
  OffsetJoinType = 0
  OffsetOpenResult = false
  PartialLoad = false
  Relative = false
  Support = -> [Sketch018]
  _Version = 2
FEATURE [PartDesign::FeaturePython] BaseBend003  # WARN: FeaturePython — macro-defined, semantics opaque (R4)
  BendSide = 1
  BendSketch = -> Binder010
  MidPlane = false
  Reverse = false
  length = 40
  radius = 0.1
  thickness = 0.3
FEATURE [PartDesign::FeaturePython] Bend003  # WARN: FeaturePython — macro-defined, semantics opaque (R4)
  AutoMiter = false
  BaseFeature = -> BaseBend003
  BendType = 0
  LengthList = [175.034]
  LengthSpec = 1
  ReliefFactor = 0.7
  UseReliefFactor = false
  angle = 90
  baseObject = -> BaseBend003 [Edge43,Edge29,Edge14]
  bendAList = [90]
  extend1 = 0
  extend2 = 0
  gap1 = 0
  gap2 = 0
  invert = false
  kfactor = 0.3
  length = 175.034
  maxExtendDist = 5
  minGap = 0.05
  minReliefGap = 1
  miterangle1 = 0
  miterangle2 = 0
  offset = 0
  radius = 0.1
  reliefType = 0
  reliefd = 1
  reliefw = 0.8
  sketchflip = false
  sketchinvert = false
  unfold = false
  expr: length = <<cap_base_sketch>>.Constraints.cap_length
  expr: radius = BaseBend003.radius
FEATURE [Sketcher::SketchObject] Sketch019
  ExternalGeometry = -> [Sketch002,Sketch018]
  FullyConstrained = true
  sketch-geometry (3):
    g0: LineSegment StartX=329.002 StartY=156.059 StartZ=0 EndX=329.002 EndY=175.034 EndZ=0
    g1: LineSegment StartX=329.002 StartY=175.034 StartZ=0 EndX=-982.007 EndY=175.034 EndZ=0
    g2: LineSegment StartX=-982.007 StartY=175.034 StartZ=0 EndX=-982.007 EndY=156.059 EndZ=0
  constraints (8):
    c: Coincident(g0,g-4)
    c: Vertical(g0)
    c: Coincident(g0,g1)
    c: Coincident(g1,g-4)
    c: Coincident(g1,g2)
    c: Vertical(g2)
    c: Horizontal(g2,g0)
    c: DistanceY(g-3,g0) = 2
FEATURE [PartDesign::SubShapeBinder] Binder011
  BindCopyOnChange = 0
  BindMode = 0
  ClaimChildren = true
  Context = -> Part [Part001.Body005.Boolean003.Body006.Binder011.]
  Fuse = false
  MakeFace = true
  OffsetFill = false
  OffsetIntersection = false
  OffsetJoinType = 0
  OffsetOpenResult = false
  PartialLoad = false
  Relative = false
  Support = -> [Sketch019]
  _Version = 2
FEATURE [PartDesign::FeaturePython] BaseBend004  # WARN: FeaturePython — macro-defined, semantics opaque (R4)
  BendSide = 1
  BendSketch = -> Binder011
  MidPlane = false
  Reverse = true
  length = 10
  radius = 0.1
  thickness = 0.3
FEATURE [PartDesign::Plane] DatumPlane
  AttachmentOffset = pos=(0,0,-326.502) rot=(0,0,1;0rad)
  Length = 220.036
  MapMode = 5
  Placement = pos=(-326.502,0,0) rot=(0.57735,0.57735,0.57735;2.0944rad)
  ResizeMode = 0
  Support = -> [YZ_Plane008]
  Width = 70.0017
  expr: .AttachmentOffset.Base.z = <<faces_bridge>>.Constraints.offset
FEATURE [PartDesign::CoordinateSystem] Local_CS
  AttacherType = Attacher::AttachEngine3D
  AttachmentOffset = pos=(0,0,0) rot=(0,1,0;1.5708rad)
  MapMode = 7
  Placement = pos=(329.002,156.059,0) rot=(0.57735,0.57735,0.57735;2.0944rad)
  Support = -> [Binder011]
FEATURE [Sketcher::SketchObject] Sketch020
  FullyConstrained = true
  MapMode = 5
  Placement = pos=(329.002,156.059,0) rot=(0.57735,0.57735,0.57735;2.0944rad)
  Support = -> [Local_CS]
  expr: Constraints[6] = -<<BaseBend004>>.length
  sketch-geometry (3):
    g0: ArcOfCircle CenterX=5 CenterY=-5 CenterZ=0 NormalX=0 NormalY=0 NormalZ=1 AngleXU=0 Radius=5 StartAngle=3.14159 EndAngle=4.71239
    g1: LineSegment StartX=0 StartY=-5 StartZ=0 EndX=0 EndY=-10 EndZ=0
    g2: LineSegment StartX=0 StartY=-10 StartZ=0 EndX=5 EndY=-10 EndZ=0
  constraints (8):
    c: PointOnObject(g0,g-2)
    c: PointOnObject(g1,g-2)
    c: Coincident(g2,g1)
    c: Horizontal(g2)
    c: Tangent(g2,g0) = -1.5708
    c: Tangent(g1,g0) = -1.5708
    c: DistanceY(g1) = -10
    c: DistanceX(g2,g2) = 5
FEATURE [PartDesign::Pocket] Pocket002
  BaseFeature = -> BaseBend004
  Direction = (-1,0,0)
  Length = 5
  Length2 = 5
  Profile = -> Sketch020
  ReferenceAxis = -> Sketch020 [N_Axis]
  Type = 0
FEATURE [PartDesign::Mirrored] Mirrored002
  BaseFeature = -> Pocket002
  MirrorPlane = -> DatumPlane
  Originals = -> [Pocket002]
FEATURE [PartDesign::Body] Body006
  Group = -> [Binder011,BaseBend004,DatumPlane,Local_CS,Sketch020,Pocket002,Mirrored002]
  Origin = -> Origin008
  Tip = -> Mirrored002
FEATURE [Part::Compound] Compound010  label="cap_outer_fuse1"
  Links = -> [Body006]
FEATURE [Sketcher::SketchObject] Sketch021  label="cap_cut"
  ExternalGeometry = -> [Sketch018]
  FullyConstrained = true
  sketch-geometry (2):
    g0: LineSegment StartX=329.002 StartY=175.034 StartZ=0 EndX=326.002 EndY=172.034 EndZ=0
    g1: ArcOfCircle CenterX=498.036 CenterY=0 CenterZ=0 NormalX=0 NormalY=0 NormalZ=1 AngleXU=0 Radius=243.293 StartAngle=2.35619 EndAngle=3.14159
  constraints (6):
    c: Coincident(g0,g-4)
    c: DistanceX(g0,g0) = 3
    c: DistanceY(g0,g0) = 3
    c: PointOnObject(g1,g-1)
    c: PointOnObject(g1,g-1)
    c: Tangent(g1,g0) = -1.5708
FEATURE [Part::Offset2D] Offset2D
  Fill = false
  Intersection = false
  Join = 0
  Mode = 1
  SelfIntersection = false
  Source = -> Sketch021
  Value = 0.05
FEATURE [PartDesign::SubShapeBinder] Binder012
  BindCopyOnChange = 0
  BindMode = 0
  ClaimChildren = true
  Context = -> Part [Part001.Body005.Binder012.]
  Fuse = false
  MakeFace = true
  OffsetFill = false
  OffsetIntersection = false
  OffsetJoinType = 0
  OffsetOpenResult = false
  PartialLoad = false
  Placement = pos=(0,0,40) rot=(0,0,1;0rad)
  Relative = false
  Support = -> [Offset2D]
  _Version = 2
  expr: .Placement.Base.z = BaseBend003.length
FEATURE [PartDesign::Plane] DatumPlane001
  AttachmentOffset = pos=(0,0,-326.502) rot=(0,0,1;0rad)
  Length = 222.91
  MapMode = 5
  Placement = pos=(-326.502,0,0) rot=(0.57735,0.57735,0.57735;2.0944rad)
  ResizeMode = 0
  Support = -> [YZ_Plane007]
  Width = 88.2755
  expr: .AttachmentOffset.Base.z = <<faces_bridge>>.Constraints.offset
FEATURE [PartDesign::Body] Body008  label="sink_hand"
  Origin = -> Origin011
FEATURE [Part::Part2DObjectPython] Line001  # Draft 2D object (typed FeaturePython)
  Area = 0
  ChamferSize = 0
  Closed = false
  End = (-162.217,21,-5e-16)
  FilletRadius = 0
  Length = 324.434
  MakeFace = false
  Placement = pos=(0,0,0) rot=(-0.14785,0.816318,0.55836;2.18251rad)
  Points = (2) [(-81.9646,-95.0022,104.937),(93.1832,114.943,-69.7159)]
  Start = (162.217,21,-5e-16)
  Subdivisions = 0
  expr: .End.x = -.Start.x
  expr: .End.y = .Start.y
  expr: .End.z = .Start.z
  expr: Start = <<Line>>.Start
FEATURE [PartDesign::SubShapeBinder] Binder013
  BindCopyOnChange = 0
  BindMode = 0
  ClaimChildren = false
  Context = -> Part002 [Body007.Binder013.]
  Fuse = false
  MakeFace = true
  OffsetFill = false
  OffsetIntersection = false
  OffsetJoinType = 0
  OffsetOpenResult = false
  PartialLoad = false
  Relative = false
  Support = -> [Sketch]
  _Version = 2
  expr: Support = <<base_sketch>>._self
FEATURE [Part::Part2DObjectPython] Line  # Draft 2D object (typed FeaturePython)
  Angle = 5.55506
  AngleYZ = 8.54811
  Area = 0
  ChamferSize = 0
  Closed = false
  End = (319.002,154.059,20)
  FilletRadius = 0
  Length = 206.607
  MakeFace = false
  MapMode = 1
  Placement = pos=(162.217,21,0) rot=(-0.14785,0.816318,0.55836;2.18251rad)
  Points = (2) [(1.42109e-14,1.42109e-14,-2.84217e-14),(-65.0656,-26.3536,194.315)]
  Start = (162.217,21,-5e-16)
  Subdivisions = 0
  Support = -> [Binder013]
  expr: Angle = asin((.End.z - .Start.z) / Length)
  expr: AngleYZ = asin((.End.z - .Start.z) / hypot(.End.y - .Start.y; .End.z - .Start.z))
  expr: End = <<DatumPoint>>.Placement.Base
FEATURE [PartDesign::Point] DatumPoint
  AttacherType = Attacher::AttachEnginePoint
  AttachmentOffset = pos=(0,0,20) rot=(0,0,1;0rad)
  MapMode = 39
  Placement = pos=(319.002,154.059,20) rot=(0,0,1;0rad)
  Support = -> [Binder013]
FEATURE [PartDesign::CoordinateSystem] Local_CS001
  AttacherType = Attacher::AttachEngine3D
  AttachmentOffset = pos=(0,21,0) rot=(1,0,0;0.149193rad)
  MapMode = 5
  Placement = pos=(0,21,0) rot=(1,0,0;0.149193rad)
  Support = -> [XY_Plane010]
  expr: .AttachmentOffset.Base.y = <<Line>>.Start.y
  expr: .AttachmentOffset.Rotation.Angle = <<Line>>.AngleYZ
FEATURE [Part::Part2DObjectPython] Line002  # Draft 2D object (typed FeaturePython)
  Area = 0
  ChamferSize = 0
  Closed = false
  End = (0,154.059,20)
  FilletRadius = 0
  Length = 134.553
  MakeFace = true
  Placement = pos=(-8.82408,2.54769,28.5595) rot=(0.548521,0.511664,0.661305;1.81276rad)
  Points = (2) [(20.7889,-28.2166,-2.37515),(151.568,2.1228,-11.3743)]
  Start = (0,21,-5e-16)
  Subdivisions = 0
  expr: .End.x = 0 mm
  expr: .End.y = <<Line>>.End.y
  expr: .End.z = <<Line>>.End.z
  expr: .Start.x = 0 mm
  expr: .Start.y = <<Line>>.Start.y
  expr: .Start.z = <<Line>>.Start.z
FEATURE [Sketcher::SketchObject] Sketch024
  ExternalGeometry = -> [Line001]
  FullyConstrained = true
  MapMode = 7
  Placement = pos=(162.217,21,-1.8e-15) rot=(0.847961,-0.39253,-0.356205;1.82987rad)
  Support = -> [Line]
  sketch-geometry (3):
    g0: ArcOfCircle CenterX=-2.5 CenterY=2.80137 CenterZ=0 NormalX=0 NormalY=0 NormalZ=1 AngleXU=0 Radius=2.5 StartAngle=4.59882 EndAngle=6.28319
    g1: LineSegment StartX=-2.78332 StartY=0.317476 StartZ=0 EndX=0 EndY=7.1e-15 EndZ=0
    g2: LineSegment StartX=0 StartY=7.1e-15 StartZ=0 EndX=0 EndY=2.80137 EndZ=0
  constraints (8):
    c: Tangent(g0,g-3) = 1.5708
    c: Coincident(g1,g0)
    c: Coincident(g1,g-3)
    c: Coincident(g2,g1)
    c: Tangent(g2,g0) = -1.5708
    c: PointOnObject(g0,g-2)
    c: Radius(g0) = 2.5
    c: Distance(g1) = 2.80137  'length'
FEATURE [Sketcher::SketchObject] Sketch025
  ExternalGeometry = -> [Line]
  FullyConstrained = true
  MapMode = 7
  Placement = pos=(162.217,21,0) rot=(0.57735,0.57735,0.57735;2.0944rad)
  Support = -> [Line001]
  sketch-geometry (3):
    g0: ArcOfCircle CenterX=2.5 CenterY=2.90386 CenterZ=0 NormalX=0 NormalY=0 NormalZ=1 AngleXU=0 Radius=2.5 StartAngle=3.14159 EndAngle=4.86158
    g1: LineSegment StartX=2.84e-14 StartY=-5e-16 StartZ=0 EndX=0 EndY=2.90386 EndZ=0
    g2: LineSegment StartX=2.84e-14 StartY=-5e-16 StartZ=0 EndX=2.8716 EndY=0.431629 EndZ=0
  constraints (7):
    c: PointOnObject(g0,g-3)
    c: PointOnObject(g0,g-2)
    c: Coincident(g1,g-3)
    c: Coincident(g2,g1)
    c: Tangent(g2,g0) = -1.5708
    c: Tangent(g1,g0) = 1.5708
    c: Radius(g0) = 2.5
FEATURE [Sketcher::SketchObject] Sketch023  label="sink_base_sketch"
  ExternalGeometry = -> [Line,Sketch025,Sketch024,Line001]
  FullyConstrained = true
  MapMode = 5
  Placement = pos=(0,21,0) rot=(1,0,0;0.149193rad)
  Support = -> [Local_CS001]
  sketch-geometry (4):
    g0: LineSegment StartX=-161.299 StartY=2.90386 StartZ=0 EndX=161.299 EndY=2.90386 EndZ=0
    g1: LineSegment StartX=161.299 StartY=2.90386 StartZ=0 EndX=314.701 EndY=134.553 EndZ=0
    g2: LineSegment StartX=314.701 StartY=134.553 StartZ=0 EndX=-314.701 EndY=134.553 EndZ=0
    g3: LineSegment StartX=-314.701 StartY=134.553 StartZ=0 EndX=-161.299 EndY=2.90386 EndZ=0
  constraints (13):
    c: Coincident(g0,g1)
    c: Coincident(g1,g2)
    c: Coincident(g2,g3)
    c: Coincident(g3,g0)
    c: PointOnObject(g-4,g0)
    c: PointOnObject(g-5,g1)
    c: Parallel(g1,g-3)
    c: Horizontal(g1,g-3)
    c: Distance(g1) = 202.148  'side_length'
    c: Symmetric(g0,g0,g-2)
    c: Symmetric(g1,g2,g-2)
    c: Distance(g0) = 322.598  'front_length'
    c: Distance(g2) = 629.402  'end'
FEATURE [PartDesign::FeaturePython] BaseBend005  # WARN: FeaturePython — macro-defined, semantics opaque (R4)
  BendSide = 0
  BendSketch = -> Sketch023
  MidPlane = false
  Reverse = false
  length = 100
  radius = 2
  thickness = 0.5
FEATURE [Sketcher::SketchObject] Sketch026
  ExternalGeometry = -> [Sketch025]
  FullyConstrained = true
  MapMode = 5
  Placement = pos=(0,0,0) rot=(0.57735,0.57735,0.57735;2.0944rad)
  Support = -> [YZ_Plane010]
  sketch-geometry (4):
    g0: ArcOfCircle CenterX=23.5 CenterY=2.90386 CenterZ=0 NormalX=0 NormalY=0 NormalZ=1 AngleXU=0 Radius=2.5 StartAngle=3.14159 EndAngle=4.86158
    g1: LineSegment StartX=23.8716 StartY=0.431629 StartZ=0 EndX=23.7973 EndY=0.926074 EndZ=0
    g2: ArcOfCircle CenterX=23.5 CenterY=2.90386 CenterZ=0 NormalX=0 NormalY=0 NormalZ=1 AngleXU=0 Radius=2 StartAngle=3.14159 EndAngle=4.86158
    g3: LineSegment StartX=21 StartY=2.90386 StartZ=0 EndX=21.5 EndY=2.90386 EndZ=0
  constraints (10):
    c: Coincident(g2,g0)
    c: Coincident(g2,g1)
    c: Perpendicular(g0,g1)
    c: Coincident(g3,g0)
    c: Coincident(g3,g2)
    c: Horizontal(g3)
    c: DistanceX(g3,g3) = 0.5
    c: Coincident(g0,g-3)
    c: Tangent(g0,g-3) = -1.5708
    c: Coincident(g1,g0)
FEATURE [PartDesign::Pad] Pad002
  BaseFeature = -> BaseBend005
  Direction = (1,0,0)
  Length = 322.598
  Length2 = 10
  Midplane = true
  Profile = -> Sketch026
  ReferenceAxis = -> Sketch026 [N_Axis]
  Type = 0
  expr: Length = <<sink_base_sketch>>.Constraints.front_length
FEATURE [Sketcher::SketchObject] Sketch027
  AttachmentOffset = pos=(0,0,-21) rot=(0,0,1;0rad)
  ExternalGeometry = -> [Sketch025]
  FullyConstrained = true
  MapMode = 5
  Placement = pos=(0,21,-4.7e-15) rot=(1,0,0;1.5708rad)
  Support = -> [XZ_Plane010]
  expr: .AttachmentOffset.Base.z = -<<base_sketch>>.Constraints.offset
  expr: Constraints[10] = <<sink_base_sketch>>.Constraints.front_length
  sketch-geometry (4):
    g0: LineSegment StartX=-161.299 StartY=2.90386 StartZ=0 EndX=161.299 EndY=2.90386 EndZ=0
    g1: LineSegment StartX=161.299 StartY=2.90386 StartZ=0 EndX=161.299 EndY=80 EndZ=0
    g2: LineSegment StartX=161.299 StartY=80 StartZ=0 EndX=-161.299 EndY=80 EndZ=0
    g3: LineSegment StartX=-161.299 StartY=80 StartZ=0 EndX=-161.299 EndY=2.90386 EndZ=0
  constraints (11):
    c: Coincident(g0,g1)
    c: Coincident(g1,g2)
    c: Coincident(g2,g3)
    c: Coincident(g3,g0)
    c: Horizontal(g2)
    c: Vertical(g1)
    c: Vertical(g3)
    c: Horizontal(g0,g-3)
    c: DistanceY(g1) = 80
    c: Symmetric(g0,g0,g-2)
    c: DistanceX(g0,g0) = 322.598
FEATURE [PartDesign::Pad] Pad003
  BaseFeature = -> Pad002
  Direction = (0,-1,2e-16)
  Length = 0.5
  Length2 = 10
  Profile = -> Sketch027
  ReferenceAxis = -> Sketch027 [N_Axis]
  Reversed = true
  Type = 0
FEATURE [Sketcher::SketchObject] Sketch028
  ExternalGeometry = -> [Sketch024]
  FullyConstrained = true
  MapMode = 7
  Placement = pos=(163.124,21.7694,0.115643) rot=(0.847961,-0.39253,-0.356205;1.82987rad)
  Support = -> [Line,Sketch023]
  sketch-geometry (4):
    g0: ArcOfCircle CenterX=-2.5 CenterY=2.80137 CenterZ=0 NormalX=0 NormalY=0 NormalZ=1 AngleXU=0 Radius=2 StartAngle=4.59882 EndAngle=6.28319
    g1: ArcOfCircle CenterX=-2.5 CenterY=2.80137 CenterZ=0 NormalX=0 NormalY=0 NormalZ=1 AngleXU=0 Radius=2.5 StartAngle=4.59882 EndAngle=6.28319
    g2: LineSegment StartX=-2.78332 StartY=0.317476 StartZ=0 EndX=-2.72666 EndY=0.814255 EndZ=0
    g3: LineSegment StartX=-0.5 StartY=2.80137 StartZ=0 EndX=-1.42e-14 EndY=2.80137 EndZ=0
  constraints (10):
    c: Coincident(g0,g-3)
    c: Coincident(g1,g-3)
    c: Tangent(g1,g-3) = -1.5708
    c: Coincident(g2,g1)
    c: Coincident(g2,g0)
    c: Coincident(g3,g0)
    c: Coincident(g3,g1)
    c: Perpendicular(g1,g3)
    c: Perpendicular(g1,g2)
    c: Distance(g2) = 0.5
FEATURE [PartDesign::Pad] Pad004
  BaseFeature = -> Pad003
  Direction = (-0.75886,-0.64402,-0.0968023)
  Length = 202.148
  Length2 = 10
  Profile = -> Sketch028
  ReferenceAxis = -> Sketch028 [N_Axis]
  Reversed = true
  Type = 0
  expr: Length = <<sink_base_sketch>>.Constraints.side_length
FEATURE [PartDesign::Line] DatumLine
  AttacherType = Attacher::AttachEngineLine
  Length = 20
  MapMode = 16
  Placement = pos=(0,0,0) rot=(0,0,1;3.14159rad)
  ResizeMode = 0
  Support = -> [Z_Axis010]
FEATURE [Sketcher::SketchObject] Sketch029
  AttachmentOffset = pos=(0,0,0) rot=(0,1,0;1.5708rad)
  ExternalGeometry = -> [Line,Sketch028]
  FullyConstrained = true
  MapMode = 7
  Placement = pos=(162.217,21,0) rot=(0.887503,0.325836,0.325836;1.68986rad)
  Support = -> [Binder013]
  expr: Constraints[9] = <<sink_base_sketch>>.Constraints.side_length
  sketch-geometry (4):
    g0: LineSegment StartX=0.917845 StartY=2.90386 StartZ=0 EndX=0.917845 EndY=80 EndZ=0
    g1: LineSegment StartX=0.917845 StartY=80 StartZ=0 EndX=202.116 EndY=80 EndZ=0
    g2: LineSegment StartX=202.116 StartY=80 StartZ=0 EndX=202.116 EndY=22.4722 EndZ=0
    g3: LineSegment StartX=0.917845 StartY=2.90386 StartZ=0 EndX=202.116 EndY=22.4722 EndZ=0
  constraints (11):
    c: Coincident(g-4,g0)
    c: Vertical(g0)
    c: Coincident(g0,g1)
    c: Horizontal(g1)
    c: Coincident(g1,g2)
    c: Vertical(g2)
    c: Coincident(g3,g0)
    c: Coincident(g3,g2)
    c: Parallel(g3,g-3)
    c: Distance(g3) = 202.148
    c: DistanceY(g0) = 80
FEATURE [PartDesign::Pad] Pad005
  BaseFeature = -> Pad004
  Direction = (0.647059,-0.76244,0)
  Length = 0.5
  Length2 = 10
  Profile = -> Sketch029
  ReferenceAxis = -> Sketch029 [N_Axis]
  Reversed = true
  Type = 0
FEATURE [Part::Mirroring] Part__Mirroring008  label="Sketch028 (Mirror #9)"
  Base = (0,0,0)
  Normal = (1,0,0)
  Source = -> Sketch028
FEATURE [PartDesign::Pad] Pad006
  BaseFeature = -> Pad005
  Direction = (0.75886,-0.64402,-0.0968023)
  Length = 202.148
  Length2 = 10
  Profile = -> Part__Mirroring008
  Reversed = true
  Type = 0
  expr: Length = <<sink_base_sketch>>.Constraints.side_length
FEATURE [Part::Mirroring] Part__Mirroring009  label="Sketch029 (Mirror #10)"
  Base = (0,0,0)
  Normal = (1,0,0)
  Source = -> Sketch029
FEATURE [PartDesign::Pad] Pad007
  BaseFeature = -> Pad006
  Direction = (0.647059,0.76244,1e-16)
  Length = 0.5
  Length2 = 10
  Profile = -> Part__Mirroring009
  Type = 0
FEATURE [App::Link] Link001  label="module"
  LinkPlacement = pos=(0,0,0) rot=(0,0.707107,0.707107;3.14159rad)
  LinkedObject = -> <external module.FCStd>#Body
  Placement = pos=(0,0,0) rot=(0,0.707107,0.707107;3.14159rad)
FEATURE [Part::FeaturePython] Populate010  label="modules"  # WARN: FeaturePython — macro-defined, semantics opaque (R4)
  Copying = 0
  ExposePlacement = false
  MarkerShape = 1
  MarkerSize = 0
  NumElements = 0
  Object = -> Link001
  OutputCompounding = 1
  PlacementsTo = -> Populate
  Referencing = 0
  Type = lattice2PopulateCopies.LatticePopulateCopies
  isLattice = 0
FEATURE [Sketcher::SketchObject] Sketch030
  ExternalGeometry = -> [Sketch023]
  FullyConstrained = true
  MapMode = 5
  Placement = pos=(0,0,0) rot=(0.57735,0.57735,0.57735;2.0944rad)
  Support = -> [YZ_Plane010]
  sketch-geometry (13):
    g0: ArcOfCircle CenterX=154.356 CenterY=18.0222 CenterZ=0 NormalX=0 NormalY=0 NormalZ=1 AngleXU=0 Radius=2 StartAngle=1.5708 EndAngle=1.71999
    g1: ArcOfCircle CenterX=154.356 CenterY=18.0222 CenterZ=0 NormalX=0 NormalY=0 NormalZ=1 AngleXU=0 Radius=2.5 StartAngle=1.5708 EndAngle=1.71999
    g2: ArcOfCircle CenterX=156.059 CenterY=18.0222 CenterZ=0 NormalX=0 NormalY=0 NormalZ=1 AngleXU=0 Radius=2 StartAngle=1.032e-13 EndAngle=1.5708
    g3: ArcOfCircle CenterX=156.059 CenterY=18.0222 CenterZ=0 NormalX=0 NormalY=0 NormalZ=1 AngleXU=0 Radius=2.5 StartAngle=8.21e-14 EndAngle=1.5708
    g4: LineSegment StartX=158.059 StartY=10.5222 StartZ=0 EndX=158.559 EndY=10.5222 EndZ=0
    g5: LineSegment StartX=158.559 StartY=10.5222 StartZ=0 EndX=158.559 EndY=18.0222 EndZ=0
    g6: LineSegment StartX=158.559 StartY=18.0222 StartZ=0 EndX=158.059 EndY=18.0222 EndZ=0
    g7: LineSegment StartX=158.059 StartY=18.0222 StartZ=0 EndX=158.059 EndY=10.5222 EndZ=0
    g8: LineSegment StartX=154.356 StartY=20.0222 StartZ=0 EndX=156.059 EndY=20.0222 EndZ=0
    g9: LineSegment StartX=156.059 StartY=20.0222 StartZ=0 EndX=156.059 EndY=20.5222 EndZ=0
    g10: LineSegment StartX=156.059 StartY=20.5222 StartZ=0 EndX=154.356 EndY=20.5222 EndZ=0
    g11: LineSegment StartX=154.356 StartY=20.5222 StartZ=0 EndX=154.356 EndY=20.0222 EndZ=0
    g12: LineSegment StartX=154.059 StartY=20 StartZ=0 EndX=153.984 EndY=20.4944 EndZ=0
  constraints (35):
    c: Coincident(g1,g0)
    c: Coincident(g3,g2)
    c: Coincident(g4,g5)
    c: Coincident(g5,g6)
    c: Coincident(g6,g7)
    c: Coincident(g7,g4)
    c: Horizontal(g4)
    c: Horizontal(g6)
    c: Vertical(g5)
    c: Vertical(g7)
    c: Coincident(g5,g3)
    c: Coincident(g6,g2)
    c: Coincident(g8,g9)
    c: Coincident(g9,g10)
    c: Coincident(g10,g11)
    c: Horizontal(g8)
    c: Horizontal(g10)
    c: Vertical(g9)
    c: Vertical(g11)
    c: Coincident(g9,g3)
    c: Coincident(g1,g10)
    c: Coincident(g12,g1)
    c: Perpendicular(g0,g12)
    c: PointOnObject(g2,g6)
    c: Equal(g2,g0)
    c: Tangent(g2,g8) = 1.5708
    c: DistanceY(g11,g11) = 0.5
    c: Radius(g2) = 2
    c: Tangent(g8,g0) = 1.5708
    c: Coincident(g11,g0)
    c: DistanceX(g0,g2) = 4
    c: DistanceY(g4,g3) = 10
    c: Coincident(g12,g-3)
    c: Coincident(g0,g12)
    c: Perpendicular(g-3,g12)
FEATURE [PartDesign::Pad] Pad008
  BaseFeature = -> Pad007
  Direction = (1,0,0)
  Length = 629.402
  Length2 = 10
  Midplane = true
  Profile = -> Sketch030
  ReferenceAxis = -> Sketch030 [N_Axis]
  Type = 0
  expr: Length = <<sink_base_sketch>>.Constraints.end
FEATURE [Sketcher::SketchObject] Sketch031
  ExternalGeometry = -> [Sketch023]
  FullyConstrained = true
  MapMode = 5
  Placement = pos=(0,21,0) rot=(1,0,0;0.149193rad)
  Support = -> [Local_CS001]
  sketch-geometry (5):
    g0: ArcOfCircle CenterX=161.299 CenterY=2.90386 CenterZ=0 NormalX=0 NormalY=0 NormalZ=1 AngleXU=0 Radius=10 StartAngle=0.709236 EndAngle=3.14159
    g1: LineSegment StartX=151.299 StartY=2.90386 StartZ=0 EndX=151.299 EndY=0 EndZ=0
    g2: LineSegment StartX=151.299 StartY=0 StartZ=0 EndX=162.374 EndY=0 EndZ=0
    g3: LineSegment StartX=162.374 StartY=0 StartZ=0 EndX=170.779 EndY=7.21278 EndZ=0
    g4: LineSegment StartX=170.779 StartY=7.21278 StartZ=0 EndX=168.888 EndY=9.4164 EndZ=0
  constraints (14):
    c: Coincident(g0,g-3)
    c: PointOnObject(g0,g-3)
    c: Radius(g0) = 10
    c: Tangent(g0,g1) = -1.5708
    c: Coincident(g1,g2)
    c: PointOnObject(g2,g-1)
    c: Horizontal(g2)
    c: Coincident(g2,g3)
    c: Coincident(g3,g4)
    c: Coincident(g4,g0)
    c: Vertical(g1)
    c: Perpendicular(g-3,g4)
    c: Equal(g4,g1)
    c: Perpendicular(g4,g3)
FEATURE [Sketcher::SketchObject] Sketch032
  ExternalGeometry = -> [Sketch029,Sketch031]
  FullyConstrained = true
  MapMode = 2
  Placement = pos=(162.217,21,0) rot=(0.887503,0.325836,0.325836;1.68986rad)
  Support = -> [Sketch029]
  sketch-geometry (9):
    g0: LineSegment StartX=1.15829 StartY=0.431629 StartZ=0 EndX=11.1113 EndY=1.39965 EndZ=0
    g1: LineSegment StartX=1.15829 StartY=0.431629 StartZ=0 EndX=0.917845 EndY=2.90386 EndZ=0
    g2: LineSegment StartX=11.1113 StartY=1.39965 StartZ=0 EndX=10.8709 EndY=3.87188 EndZ=0
    g3: LineSegment StartX=0.917845 StartY=2.90386 StartZ=0 EndX=0.917845 EndY=17.046 EndZ=0
    g4: ArcOfCircle CenterX=5.91784 CenterY=75 CenterZ=0 NormalX=0 NormalY=0 NormalZ=1 AngleXU=0 Radius=5 StartAngle=1.5708 EndAngle=3.14159
    g5: LineSegment StartX=0.917845 StartY=75 StartZ=0 EndX=0.917845 EndY=80 EndZ=0
    g6: LineSegment StartX=0.917845 StartY=80 StartZ=0 EndX=5.91784 EndY=80 EndZ=0
    g7: ArcOfCircle CenterX=0.917845 CenterY=2.90386 CenterZ=0 NormalX=0 NormalY=0 NormalZ=1 AngleXU=0 Radius=10 StartAngle=0.0969541 EndAngle=1.23096
    g8: ArcOfCircle CenterX=5.91784 CenterY=17.046 CenterZ=0 NormalX=0 NormalY=0 NormalZ=1 AngleXU=0 Radius=5 StartAngle=3.14159 EndAngle=4.37255
  constraints (23):
    c: Coincident(g0,g-4)
    c: PointOnObject(g0,g-4)
    c: Parallel(g0,g-5)
    c: Coincident(g1,g0)
    c: Coincident(g1,g-5)
    c: Coincident(g2,g0)
    c: PointOnObject(g2,g-5)
    c: Perpendicular(g0,g2)
    c: Coincident(g3,g1)
    c: Vertical(g3)
    c: Coincident(g7,g1)
    c: Coincident(g7,g2)
    c: Coincident(g5,g6)
    c: Coincident(g6,g4)
    c: Horizontal(g6)
    c: Tangent(g6,g4)
    c: Coincident(g5,g-3)
    c: Vertical(g5)
    c: Tangent(g4,g5) = 1.5708
    c: Radius(g4) = 5
    c: Tangent(g8,g7) = 1.5708
    c: Tangent(g8,g3) = 1.5708
    c: Radius(g8) = 5
FEATURE [PartDesign::Pocket] Pocket005
  BaseFeature = -> Pad008
  Direction = (0,0.14864,-0.988891)
  Length = 5
  Length2 = 5
  Midplane = true
  Profile = -> Sketch031
  ReferenceAxis = -> Sketch031 [N_Axis]
  Type = 0
FEATURE [PartDesign::Pocket] Pocket006
  BaseFeature = -> Pocket005
  Direction = (-0.647059,0.76244,0)
  Length = 2.80137
  Length2 = 5
  Profile = -> Sketch032
  ReferenceAxis = -> Sketch032 [N_Axis]
  Type = 0
  expr: Length = <<Sketch024>>.Constraints.length
FEATURE [Sketcher::SketchObject] Sketch033
  ExternalGeometry = -> [Sketch031,Sketch027]
  FullyConstrained = true
  MapMode = 2
  Placement = pos=(0,21,-4.7e-15) rot=(1,0,0;1.5708rad)
  Support = -> [Sketch027]
  sketch-geometry (8):
    g0: LineSegment StartX=161.299 StartY=0.431629 StartZ=0 EndX=151.299 EndY=0.431629 EndZ=0
    g1: LineSegment StartX=151.299 StartY=0.431629 StartZ=0 EndX=151.299 EndY=2.90386 EndZ=0
    g2: LineSegment StartX=161.299 StartY=0.431629 StartZ=0 EndX=161.299 EndY=17.046 EndZ=0
    g3: ArcOfCircle CenterX=156.299 CenterY=75 CenterZ=0 NormalX=0 NormalY=0 NormalZ=1 AngleXU=0 Radius=5 StartAngle=2.4e-15 EndAngle=1.5708
    g4: LineSegment StartX=156.299 StartY=80 StartZ=0 EndX=161.299 EndY=80 EndZ=0
    g5: LineSegment StartX=161.299 StartY=80 StartZ=0 EndX=161.299 EndY=75 EndZ=0
    g6: ArcOfCircle CenterX=161.299 CenterY=2.90386 CenterZ=0 NormalX=0 NormalY=0 NormalZ=1 AngleXU=0 Radius=10 StartAngle=1.91063 EndAngle=3.14159
    g7: ArcOfCircle CenterX=156.299 CenterY=17.046 CenterZ=0 NormalX=0 NormalY=0 NormalZ=1 AngleXU=0 Radius=5 StartAngle=5.05223 EndAngle=6.28319
  constraints (19):
    c: Coincident(g0,g-3)
    c: PointOnObject(g0,g-3)
    c: Horizontal(g0)
    c: PointOnObject(g2,g-4)
    c: Tangent(g1,g6) = 1.5708
    c: Vertical(g1)
    c: Coincident(g1,g0)
    c: Coincident(g2,g0)
    c: PointOnObject(g3,g-4)
    c: Coincident(g4,g5)
    c: Tangent(g5,g3) = 1.5708
    c: Tangent(g3,g4) = 1.5708
    c: Horizontal(g4)
    c: Coincident(g4,g-4)
    c: Radius(g3) = 5
    c: Tangent(g7,g6) = 1.5708
    c: Tangent(g7,g2) = -1.5708
    c: Radius(g7) = 5
    c: Coincident(g6,g-4)
FEATURE [PartDesign::Pocket] Pocket007
  BaseFeature = -> Pocket006
  Direction = (0,1,-2e-16)
  Length = 0.7
  Length2 = 5
  Profile = -> Sketch033
  ReferenceAxis = -> Sketch033 [N_Axis]
  Refine = true
  Type = 0
FEATURE [Sketcher::SketchObject] Sketch034
  ExternalGeometry = -> [Sketch029]
  FullyConstrained = false
  MapMode = 2
  Placement = pos=(162.217,21,0) rot=(0.887503,0.325836,0.325836;1.68986rad)
  Support = -> [Sketch029]
  sketch-geometry (6):
    g0: ArcOfCircle CenterX=206.072 CenterY=77 CenterZ=0 NormalX=0 NormalY=0 NormalZ=1 AngleXU=0 Radius=3 StartAngle=5.06802 EndAngle=7.85398
    g1: ArcOfCircle CenterX=204.116 CenterY=25.6809 CenterZ=0 NormalX=0 NormalY=0 NormalZ=1 AngleXU=0 Radius=3 StartAngle=4.80934 EndAngle=6.28319
    g2: LineSegment StartX=202.116 StartY=22.4722 StartZ=0 EndX=204.407 EndY=22.695 EndZ=0
    g3: LineSegment StartX=202.116 StartY=80 StartZ=0 EndX=206.072 EndY=80 EndZ=0
    g4: LineSegment StartX=202.116 StartY=80 StartZ=0 EndX=202.116 EndY=22.4722 EndZ=0
    g5: LineSegment StartX=207.116 StartY=25.6809 StartZ=0 EndX=207.116 EndY=74.1877 EndZ=0
  constraints (14):
    c: Coincident(g2,g-4)
    c: Coincident(g3,g-3)
    c: Coincident(g4,g3)
    c: Coincident(g4,g2)
    c: Coincident(g5,g0)
    c: Equal(g0,g1)
    c: Radius(g0) = 3
    c: Tangent(g5,g1) = -1.5708
    c: Parallel(g2,g-4)
    c: Tangent(g2,g1) = -1.5708
    c: Vertical(g5)
    c: Tangent(g3,g0) = 1.5708
    c: Horizontal(g3)
    c: DistanceX(g2,g1) = 5
FEATURE [PartDesign::Pad] Pad009
  BaseFeature = -> Pocket007
  Direction = (0.647059,-0.76244,0)
  Length = 0.5
  Length2 = 10
  Profile = -> Sketch034
  ReferenceAxis = -> Sketch034 [N_Axis]
  Reversed = true
  Type = 0
FEATURE [PartDesign::Fillet] Fillet
  Base = -> Pad009 [Edge88]
  BaseFeature = -> Pad009
  Radius = 2
  SupportTransform = false
  UseAllEdges = false
FEATURE [PartDesign::Mirrored] Mirrored004
  BaseFeature = -> Fillet
  MirrorPlane = -> YZ_Plane010
  Originals = -> [Pocket005,Pocket006,Pocket007,Pad009,Fillet]
  Refine = true
FEATURE [Sketcher::SketchObject] Sketch035
  ExternalGeometry = -> [Sketch023]
  FullyConstrained = true
  MapMode = 5
  Placement = pos=(0,21,0) rot=(1,0,0;0.149193rad)
  Support = -> [Local_CS001]
  sketch-geometry (4):
    g0: ArcOfCircle CenterX=0 CenterY=2.90386 CenterZ=0 NormalX=0 NormalY=0 NormalZ=1 AngleXU=0 Radius=10 StartAngle=0 EndAngle=3.14159
    g1: LineSegment StartX=-10 StartY=2.90386 StartZ=0 EndX=-10 EndY=0 EndZ=0
    g2: LineSegment StartX=-10 StartY=0 StartZ=0 EndX=10 EndY=0 EndZ=0
    g3: LineSegment StartX=10 StartY=0 StartZ=0 EndX=10 EndY=2.90386 EndZ=0
  constraints (13):
    c: PointOnObject(g0,g-3)
    c: PointOnObject(g0,g-3)
    c: PointOnObject(g0,g-3)
    c: PointOnObject(g0,g-2)
    c: Coincident(g1,g0)
    c: PointOnObject(g1,g-1)
    c: Vertical(g1)
    c: Coincident(g2,g1)
    c: PointOnObject(g2,g-1)
    c: Coincident(g3,g2)
    c: Coincident(g3,g0)
    c: Vertical(g3)
    c: Radius(g0) = 10
FEATURE [Sketcher::SketchObject] Sketch036
  AttachmentOffset = pos=(0,0,-14) rot=(0,0,1;0rad)
  ExternalGeometry = -> [Sketch025,Sketch035]
  FullyConstrained = true
  MapMode = 5
  Placement = pos=(0,14,-3.1e-15) rot=(1,0,0;1.5708rad)
  Support = -> [XZ_Plane010]
  sketch-geometry (4):
    g0: ArcOfCircle CenterX=0 CenterY=2.90386 CenterZ=0 NormalX=0 NormalY=0 NormalZ=1 AngleXU=0 Radius=10 StartAngle=0 EndAngle=3.14159
    g1: LineSegment StartX=10 StartY=5.1e-15 StartZ=0 EndX=10 EndY=2.90386 EndZ=0
    g2: LineSegment StartX=10 StartY=5.1e-15 StartZ=0 EndX=-10 EndY=0 EndZ=0
    g3: LineSegment StartX=-10 StartY=0 StartZ=0 EndX=-10 EndY=2.90386 EndZ=0
  constraints (10):
    c: PointOnObject(g0,g-2)
    c: Horizontal(g0,g-3)
    c: Coincident(g1,g-4)
    c: Vertical(g1)
    c: Tangent(g1,g0) = -1.5708
    c: Coincident(g1,g2)
    c: PointOnObject(g2,g-1)
    c: Coincident(g2,g3)
    c: Tangent(g3,g0) = 1.5708
    c: Vertical(g3)
FEATURE [Sketcher::SketchObject] Sketch037
  ExternalGeometry = -> [Sketch004]
  FullyConstrained = true
  Placement = pos=(0,21.5,0) rot=(0,0.707107,0.707107;3.14159rad)
  expr: .Placement.Base.y = <<base_sketch>>.Constraints.offset + 0.5 mm
  expr: Constraints[10] = <<Properties>>.rivet_d
  sketch-geometry (12):
    g0: Circle CenterX=0 CenterY=30 CenterZ=0 NormalX=0 NormalY=0 NormalZ=1 AngleXU=0 Radius=1.7
    g1: Circle CenterX=0 CenterY=70 CenterZ=0 NormalX=0 NormalY=0 NormalZ=1 AngleXU=0 Radius=1.7
    g2: Circle CenterX=-154 CenterY=70 CenterZ=0 NormalX=0 NormalY=0 NormalZ=1 AngleXU=0 Radius=1.7
    g3: LineSegment StartX=-74.5 StartY=0 StartZ=0 EndX=-74.5 EndY=70 EndZ=0
    g4: Circle CenterX=154 CenterY=70 CenterZ=0 NormalX=0 NormalY=0 NormalZ=1 AngleXU=0 Radius=1.7
    g5: GeomPoint X=-149 Y=70 Z=0
    g6: LineSegment StartX=-154 StartY=70 StartZ=0 EndX=154 EndY=70 EndZ=0
    g7: LineSegment StartX=154 StartY=70 StartZ=0 EndX=154 EndY=30 EndZ=0
    g8: LineSegment StartX=154 StartY=30 StartZ=0 EndX=-154 EndY=30 EndZ=0
    g9: LineSegment StartX=-154 StartY=30 StartZ=0 EndX=-154 EndY=70 EndZ=0
    g10: Circle CenterX=-154 CenterY=30 CenterZ=0 NormalX=0 NormalY=0 NormalZ=1 AngleXU=0 Radius=1.7
    g11: Circle CenterX=154 CenterY=30 CenterZ=0 NormalX=0 NormalY=0 NormalZ=1 AngleXU=0 Radius=1.7
  constraints (29):
    c: PointOnObject(g0,g-2)
    c: PointOnObject(g1,g-2)
    c: Coincident(g3,g-3)
    c: Vertical(g3)
    c: Horizontal(g3,g1)
    c: DistanceY(g1) = 70  'height'
    c: DistanceY(g0,g1) = 40
    c: Equal(g0,g4)
    c: Equal(g0,g1)
    c: Equal(g0,g2)
    c: Diameter(g0) = 3.4
    c: Symmetric(g4,g2,g-2)
    c: Symmetric(g5,g1,g3)
    c: Horizontal(g2,g5)
    c: DistanceX(g2,g5) = 5
    c: Coincident(g6,g7)
    c: Coincident(g7,g8)
    c: Coincident(g8,g9)
    c: Coincident(g9,g6)
    c: Horizontal(g8)
    c: Vertical(g7)
    c: Vertical(g9)
    c: Coincident(g6,g2)
    c: Coincident(g6,g4)
    c: PointOnObject(g0,g8)
    c: Coincident(g10,g8)
    c: Coincident(g11,g7)
    c: Equal(g11,g0)
    c: Equal(g0,g10)
FEATURE [Sketcher::SketchObject] Sketch038
  AttachmentOffset = pos=(0,0,-0.5) rot=(0,1,0;3.14159rad)
  FullyConstrained = true
  MapMode = 7
  Placement = pos=(228.772,78.1392,0) rot=(-0.251276,0.68442,0.68442;3.63395rad)
  Support = -> [Sketch004]
  expr: Constraints[4] = <<Properties>>.rivet_d
  sketch-geometry (2):
    g0: Circle CenterX=78.5 CenterY=70 CenterZ=0 NormalX=0 NormalY=0 NormalZ=1 AngleXU=0 Radius=1.7
    g1: Circle CenterX=-78.5 CenterY=70 CenterZ=0 NormalX=0 NormalY=0 NormalZ=1 AngleXU=0 Radius=1.7
  constraints (5):
    c: Symmetric(g1,g0,g-2)
    c: DistanceX(g1,g0) = 157
    c: DistanceY(g0) = 70
    c: Equal(g0,g1)
    c: Diameter(g0) = 3.4
FEATURE [Part::Extrusion] Extrude006
  Base = -> Sketch037
  Dir = (0,1,-2e-16)
  DirMode = 2
  FaceMakerClass = Part::FaceMakerBullseye
  LengthFwd = 10
  LengthRev = 0
  Reversed = true
  Solid = true
  Symmetric = false
FEATURE [Part::Extrusion] Extrude007
  Base = -> Sketch038
  Dir = (-0.647059,0.76244,0)
  DirMode = 2
  FaceMakerClass = Part::FaceMakerBullseye
  LengthFwd = 10
  LengthRev = 0
  Reversed = true
  Solid = true
  Symmetric = false
FEATURE [Part::Mirroring] Part__Mirroring010  label="Extrude007 (Mirror #11)"
  Base = (0,0,0)
  Normal = (1,0,0)
  Source = -> Extrude007
FEATURE [Part::Compound] Compound011
  Links = -> [Extrude007,Part__Mirroring010,Extrude006]
FEATURE [Part::Compound] Compound012  label="sink_cut1"
  Links = -> [Compound011]
FEATURE [PartDesign::Boolean] Boolean004
  BaseFeature = -> Mirrored004
  Group = -> [Compound012]
  Type = 1
FEATURE [PartDesign::Body] Body007  label="sink_ss_material_0.30ansi"
  Group = -> [Line001,Line,Binder013,DatumPoint,Local_CS001,Sketch023,Line002,Sketch024,Sketch025,BaseBend005,Sketch026,Pad002,Sketch027,Pad003,Sketch028,Pad004,DatumLine,Sketch029,Pad005,Part__Mirroring008,Pad006,Part__Mirroring009,Pad007,Sketch030,Pad008,Sketch031,Sketch032,Pocket005,Pocket006,Sketch033,Pocket007,Sketch034,Pad009,Fillet,Mirrored004,Sketch035,Sketch036,Boolean004]
  Origin = -> Origin010
  Tip = -> Boolean004
FEATURE [App::Part] Part002  label="sink"
  Group = -> [Body007,Body008]
  Origin = -> Origin009
FEATURE [Part::FeaturePython] Populate011  label="Populate faces_placements with Extrude006"  # WARN: FeaturePython — macro-defined, semantics opaque (R4)
  Copying = 0
  ExposePlacement = false
  MarkerShape = 1
  MarkerSize = 0
  NumElements = 0
  Object = -> Extrude006
  OutputCompounding = 1
  PlacementsTo = -> LinearArray001
  Referencing = 0
  Type = lattice2PopulateCopies.LatticePopulateCopies
  isLattice = 0
FEATURE [Sketcher::SketchObject] Sketch039  label="bar_base_sketch"
  FullyConstrained = true
  expr: Constraints[11] = <<base_sketch>>.Constraints.offset - 3 mm - 2 mm
  sketch-geometry (5):
    g0: LineSegment StartX=-34 StartY=0 StartZ=0 EndX=-20 EndY=0 EndZ=0
    g1: LineSegment StartX=-20 StartY=0 StartZ=0 EndX=-20 EndY=16 EndZ=0
    g2: LineSegment StartX=-20 StartY=16 StartZ=0 EndX=20 EndY=16 EndZ=0
    g3: LineSegment StartX=20 StartY=16 StartZ=0 EndX=20 EndY=0 EndZ=0
    g4: LineSegment StartX=20 StartY=0 StartZ=0 EndX=34 EndY=0 EndZ=0
  constraints (14):
    c: PointOnObject(g0,g-1)
    c: Coincident(g0,g1)
    c: Vertical(g1)
    c: Coincident(g1,g2)
    c: Coincident(g2,g3)
    c: PointOnObject(g3,g-1)
    c: Coincident(g3,g4)
    c: PointOnObject(g4,g-1)
    c: Symmetric(g1,g2,g-2)
    c: Vertical(g3)
    c: Symmetric(g0,g4,g-2)
    c: DistanceY(g3,g3) = 16
    c: DistanceX(g2,g2) = 40
    c: DistanceX(g4,g4) = 14
FEATURE [PartDesign::SubShapeBinder] Binder014
  BindCopyOnChange = 0
  BindMode = 0
  ClaimChildren = true
  Context = -> Part003 [Body009.Binder014.]
  Fuse = false
  MakeFace = true
  OffsetFill = false
  OffsetIntersection = false
  OffsetJoinType = 0
  OffsetOpenResult = false
  PartialLoad = false
  Relative = true
  Support = -> [Sketch039]
  _Version = 2
FEATURE [Part::Part2DObjectPython] Line003  label="length"  # Draft 2D object (typed FeaturePython)
  Area = 0
  ChamferSize = 0
  Closed = false
  End = (-982.007,0,0)
  FilletRadius = 0
  Length = 1311.01
  MakeFace = true
  Placement = pos=(249.164,-1.59552,0) rot=(0,0,1;0rad)
  Points = (2) [(79.8384,1.59552,0),(-1231.17,1.59552,0)]
  Start = (329.002,0,0)
  Subdivisions = 0
  expr: .End.x = -.Start.x + <<faces_bridge>>.Constraints.offset * 2
  expr: .Start.x = <<wall>>.Constraints.distance
FEATURE [App::DocumentObjectGroup] Group  label="sketches"
  Group = -> [Sketch004,Sketch005,Line003]
FEATURE [Sketcher::SketchObject] Sketch040  label="wall_fix_sketch"
  FullyConstrained = true
  sketch-geometry (9):
    g0: ArcOfCircle CenterX=0 CenterY=0 CenterZ=0 NormalX=0 NormalY=0 NormalZ=1 AngleXU=0 Radius=7.5 StartAngle=5.32983 EndAngle=10.3781
    g1: ArcOfCircle CenterX=0 CenterY=-12 CenterZ=0 NormalX=0 NormalY=0 NormalZ=1 AngleXU=0 Radius=3.5 StartAngle=3.14159 EndAngle=6.28319
    g2: LineSegment StartX=-3.5 StartY=-12 StartZ=0 EndX=-3.5 EndY=-7.74597 EndZ=0
    g3: LineSegment StartX=3.5 StartY=-7.74597 StartZ=0 EndX=3.5 EndY=-12 EndZ=0
    g4: GeomPoint X=0 Y=7.5 Z=0
    g5: GeomPoint X=0 Y=-15.5 Z=0
    g6: GeomPoint X=0 Y=-4 Z=0
    g7: ArcOfCircle CenterX=5.5 CenterY=-7.74597 CenterZ=0 NormalX=0 NormalY=0 NormalZ=1 AngleXU=0 Radius=2 StartAngle=2.18823 EndAngle=3.14159
    g8: ArcOfCircle CenterX=-5.5 CenterY=-7.74597 CenterZ=0 NormalX=0 NormalY=0 NormalZ=1 AngleXU=0 Radius=2 StartAngle=1e-16 EndAngle=0.953359
  constraints (21):
    c: Coincident(g0,g-1)
    c: PointOnObject(g1,g-2)
    c: Vertical(g2)
    c: Vertical(g3)
    c: Tangent(g3,g1) = 1.5708
    c: Tangent(g2,g1) = 1.5708
    c: Diameter(g0) = 15
    c: Diameter(g1) = 7
    c: DistanceY(g1) = -12
    c: PointOnObject(g4,g0)
    c: PointOnObject(g5,g1)
    c: PointOnObject(g5,g-2)
    c: PointOnObject(g4,g-2)
    c: Symmetric(g5,g4,g6)
    c: DistanceY(g6) = -4  'center'
    c: Tangent(g3,g7) = -1.5708
    c: Tangent(g0,g7) = 1.5708
    c: Tangent(g2,g8) = -1.5708
    c: Tangent(g0,g8) = 1.5708
    c: Equal(g7,g8)
    c: Radius(g7) = 2
FEATURE [Part::FeaturePython] LinearArray003  label="wall_fix_array"  # WARN: FeaturePython — macro-defined, semantics opaque (R4)
  Alignment = 0
  CellStart = A1
  Count = 2
  Dir = (1,0,0)
  DirIsDriven = true
  DistributionLaw = 0
  DrivenProperty = 1
  EndInclusive = true
  ExposePlacement = false
  GeneratorMode = 0
  MarkerShape = 1
  MarkerSize = 0
  NumElements = 2
  OrientMode = 1
  Point = (0,0,0)
  PointIsDriven = true
  Reverse = false
  SpanEnd = 1205.01
  SpanStart = 100
  Step = 1105.01
  Type = lattice2LinearArray.LinearArray
  VSGVersion = 1
  Values = 100.0 | 1205.009674930353
  ValuesSource = 2
  isLattice = 1
  expr: SpanEnd = <<length>>.Length - 6 mm - SpanStart
FEATURE [Part::Extrusion] Extrude008
  Base = -> Sketch040
  Dir = (0,0,1)
  DirMode = 2
  FaceMakerClass = Part::FaceMakerBullseye
  LengthFwd = 10
  LengthRev = 0
  Solid = true
  Symmetric = false
FEATURE [Part::FeaturePython] Populate012  label="Populate wall_fix_array with Extrude008"  # WARN: FeaturePython — macro-defined, semantics opaque (R4)
  Copying = 0
  ExposePlacement = false
  MarkerShape = 1
  MarkerSize = 0
  NumElements = 0
  Object = -> Extrude008
  OutputCompounding = 1
  Placement = pos=(-4,18,0) rot=(0.57735,-0.57735,0.57735;2.0944rad)
  PlacementsTo = -> LinearArray003
  Referencing = 0
  Type = lattice2PopulateCopies.LatticePopulateCopies
  isLattice = 0
  expr: .Placement.Base.x = <<wall_fix_sketch>>.Constraints.center
  expr: .Placement.Base.y = <<base_sketch>>.Constraints.offset - 3 mm
FEATURE [Sketcher::SketchObject] Sketch041
  ExternalGeometry = -> [Sketch039]
  FullyConstrained = true
  sketch-geometry (16):
    g0: LineSegment StartX=34 StartY=0 StartZ=0 EndX=22 EndY=1.6e-14 EndZ=0
    g1: LineSegment StartX=18 StartY=4 StartZ=0 EndX=18 EndY=12 EndZ=0
    g2: LineSegment StartX=16 StartY=14 StartZ=0 EndX=0 EndY=14 EndZ=0
    g3: LineSegment StartX=0 StartY=16 StartZ=0 EndX=16 EndY=16 EndZ=0
    g4: LineSegment StartX=20 StartY=12 StartZ=0 EndX=20 EndY=4 EndZ=0
    g5: LineSegment StartX=22 StartY=2 StartZ=0 EndX=34 EndY=2 EndZ=0
    g6: LineSegment StartX=34 StartY=2 StartZ=0 EndX=34 EndY=0 EndZ=0
    g7: LineSegment StartX=0 StartY=14 StartZ=0 EndX=0 EndY=16 EndZ=0
    g8: ArcOfCircle CenterX=22 CenterY=4 CenterZ=0 NormalX=0 NormalY=0 NormalZ=1 AngleXU=0 Radius=4 StartAngle=3.14159 EndAngle=4.71239
    g9: GeomPoint X=18 Y=0 Z=0
    g10: ArcOfCircle CenterX=22 CenterY=4 CenterZ=0 NormalX=0 NormalY=0 NormalZ=1 AngleXU=0 Radius=2 StartAngle=3.14159 EndAngle=4.71239
    g11: GeomPoint X=20 Y=2 Z=0
    g12: ArcOfCircle CenterX=16 CenterY=12 CenterZ=0 NormalX=0 NormalY=0 NormalZ=1 AngleXU=0 Radius=2 StartAngle=4e-16 EndAngle=1.5708
    g13: GeomPoint X=18 Y=14 Z=0
    g14: ArcOfCircle CenterX=16 CenterY=12 CenterZ=0 NormalX=0 NormalY=0 NormalZ=1 AngleXU=0 Radius=4 StartAngle=-2.7e-15 EndAngle=1.5708
    g15: GeomPoint X=20 Y=16 Z=0
  constraints (36):
    c: Coincident(g-3,g0)
    c: PointOnObject(g9,g-1)
    c: Vertical(g1)
    c: PointOnObject(g2,g-2)
    c: Horizontal(g2)
    c: PointOnObject(g3,g-4)
    c: Coincident(g15,g-4)
    c: Vertical(g4)
    c: Horizontal(g5)
    c: Coincident(g5,g6)
    c: Coincident(g6,g0)
    c: Vertical(g6)
    c: Coincident(g7,g2)
    c: Coincident(g7,g3)
    c: Vertical(g7)
    c: Equal(g7,g6)
    c: PointOnObject(g9,g0)
    c: PointOnObject(g9,g1)
    c: Tangent(g0,g8) = 1.5708
    c: Tangent(g1,g8) = 1.5708
    c: PointOnObject(g11,g4)
    c: PointOnObject(g11,g5)
    c: Tangent(g4,g10) = -1.5708
    c: Tangent(g5,g10) = -1.5708
    c: PointOnObject(g13,g1)
    c: PointOnObject(g13,g2)
    c: Tangent(g1,g12) = -1.5708
    c: Tangent(g2,g12) = -1.5708
    c: PointOnObject(g15,g4)
    c: Tangent(g4,g14) = 1.5708
    c: Tangent(g3,g14) = 1.5708
    c: Coincident(g14,g12)
    c: Coincident(g8,g10)
    c: Equal(g10,g12)
    c: Radius(g12) = 2
    c: DistanceY(g6,g6) = 2
FEATURE [Part::Mirroring] Part__Mirroring011  label="Sketch041 (Mirror #12)"
  Base = (0,0,0)
  Normal = (1,0,0)
  Source = -> Sketch041
FEATURE [Part::FeaturePython] Connect005  # WARN: FeaturePython — macro-defined, semantics opaque (R4)
  Objects = -> [Sketch041,Part__Mirroring011]
  Tolerance = 0
FEATURE [PartDesign::SubShapeBinder] Binder015
  BindCopyOnChange = 0
  BindMode = 0
  ClaimChildren = true
  Context = -> Part003 [Body009.Binder015.]
  Fuse = false
  MakeFace = true
  OffsetFill = false
  OffsetIntersection = false
  OffsetJoinType = 0
  OffsetOpenResult = false
  PartialLoad = false
  Relative = true
  Support = -> [Connect005]
  _Version = 2
FEATURE [Part::FeaturePython] Placment002  # WARN: FeaturePython — macro-defined, semantics opaque (R4)
  AttacherType = Attacher::AttachEngine3D
  AttachmentOffset = pos=(0,0,4.7) rot=(0,-1,0;1.5708rad)
  ExposePlacement = true
  MapMode = 7
  MarkerShape = 1
  MarkerSize = 5
  NumElements = 1
  Placement = pos=(29.3,0,0) rot=(0,-0.707107,-0.707107;3.14159rad)
  Support = -> [Sketch039]
  Type = lattice2AttachablePlacement.AttachablePlacement
  isLattice = 1
FEATURE [Part::FeaturePython] Mirror001  label="Mirror001 of Placment002"  # WARN: FeaturePython — macro-defined, semantics opaque (R4)
  ExposePlacement = false
  FlipX = true
  FlipY = false
  FlipZ = false
  MarkerShape = 1
  MarkerSize = 5
  NumElements = 1
  Object = -> Placment002
  ObjectTraversal = 0
  Type = lattice2Mirror.LatticeMirror
  isLattice = 1
FEATURE [Part::FeaturePython] Join001  # WARN: FeaturePython — macro-defined, semantics opaque (R4)
  ExposePlacement = false
  Interleave = false
  Links = -> [Mirror001,Placment002]
  MarkerShape = 1
  MarkerSize = 0
  NumElements = 2
  Type = lattice2JoinArrays.JoinArrays
  isLattice = 1
FEATURE [Sketcher::SketchObject] Sketch042
  FullyConstrained = true
  MapMode = 5
  Placement = pos=(0,0,0) rot=(0.57735,0.57735,0.57735;2.0944rad)
  Support = -> [YZ_Plane013]
  sketch-geometry (4):
    g0: ArcOfCircle CenterX=4 CenterY=4 CenterZ=0 NormalX=0 NormalY=0 NormalZ=1 AngleXU=0 Radius=4 StartAngle=3.14159 EndAngle=4.71239
    g1: ArcOfCircle CenterX=4 CenterY=4 CenterZ=0 NormalX=0 NormalY=0 NormalZ=1 AngleXU=0 Radius=2 StartAngle=3.14159 EndAngle=4.71239
    g2: LineSegment StartX=0 StartY=4 StartZ=0 EndX=2 EndY=4 EndZ=0
    g3: LineSegment StartX=4 StartY=0 StartZ=0 EndX=4 EndY=2 EndZ=0
  constraints (11):
    c: Coincident(g1,g0)
    c: Coincident(g2,g0)
    c: Coincident(g2,g1)
    c: Coincident(g3,g0)
    c: Coincident(g3,g1)
    c: Perpendicular(g1,g3)
    c: Perpendicular(g1,g2)
    c: Tangent(g0,g-1) = -1.5708
    c: Tangent(g0,g-2) = 1.5708
    c: Radius(g1) = 2
    c: DistanceY(g3,g3) = 2
FEATURE [Sketcher::SketchObject] Sketch043
  FullyConstrained = true
  MapMode = 5
  Support = -> [XY_Plane013]
  sketch-geometry (10):
    g0: LineSegment StartX=-34 StartY=4 StartZ=0 EndX=-34 EndY=65 EndZ=0
    g1: LineSegment StartX=-27 StartY=72 StartZ=0 EndX=27 EndY=72 EndZ=0
    g2: LineSegment StartX=34 StartY=65 StartZ=0 EndX=34 EndY=4 EndZ=0
    g3: LineSegment StartX=34 StartY=4 StartZ=0 EndX=-34 EndY=4 EndZ=0
    g4: GeomPoint X=0 Y=38 Z=0
    g5: ArcOfCircle CenterX=27 CenterY=65 CenterZ=0 NormalX=0 NormalY=0 NormalZ=1 AngleXU=0 Radius=7 StartAngle=0 EndAngle=1.5708
    g6: GeomPoint X=34 Y=72 Z=0
    g7: ArcOfCircle CenterX=-27 CenterY=65 CenterZ=0 NormalX=0 NormalY=0 NormalZ=1 AngleXU=0 Radius=7 StartAngle=1.5708 EndAngle=3.14159
    g8: GeomPoint X=-34 Y=72 Z=0
    g9: LineSegment StartX=34 StartY=4 StartZ=0 EndX=34 EndY=72 EndZ=0
  constraints (23):
    c: Coincident(g2,g3)
    c: Coincident(g3,g0)
    c: Horizontal(g1)
    c: Horizontal(g3)
    c: Vertical(g0)
    c: Vertical(g2)
    c: Symmetric(g6,g0,g4)
    c: PointOnObject(g4,g-2)
    c: DistanceY(g2) = 4
    c: DistanceX(g3,g3) = 68  'width'
    c: PointOnObject(g6,g1)
    c: PointOnObject(g6,g2)
    c: Tangent(g1,g5) = 1.5708
    c: Tangent(g2,g5) = 1.5708
    c: PointOnObject(g8,g0)
    c: PointOnObject(g8,g1)
    c: Tangent(g0,g7) = 1.5708
    c: Tangent(g1,g7) = 1.5708
    c: Equal(g5,g7)
    c: Radius(g5) = 7
    c: Coincident(g9,g2)
    c: Coincident(g9,g6)
    c: Equal(g9,g3)
FEATURE [PartDesign::Pad] Pad011
  Direction = (1,0,0)
  Length = 68
  Length2 = 10
  Midplane = true
  Placement = pos=(0,0,0) rot=(0.57735,0.57735,0.57735;2.0944rad)
  Profile = -> Sketch042
  ReferenceAxis = -> Sketch042 [N_Axis]
  Type = 0
  expr: Length = <<Sketch043>>.Constraints.width
FEATURE [PartDesign::Pad] Pad012
  BaseFeature = -> Pad011
  Direction = (0,0,1)
  Length = 2
  Length2 = 10
  Placement = pos=(0,0,0) rot=(0.57735,0.57735,0.57735;2.0944rad)
  Profile = -> Sketch043
  ReferenceAxis = -> Sketch043 [N_Axis]
  Type = 0
FEATURE [Sketcher::SketchObject] Sketch044
  ExternalGeometry = -> [Sketch043]
  FullyConstrained = true
  MapMode = 5
  Placement = pos=(0,0,0) rot=(1,0,0;1.5708rad)
  Support = -> [XZ_Plane013]
  sketch-geometry (9):
    g0: LineSegment StartX=34 StartY=59 StartZ=0 EndX=34 EndY=4 EndZ=0
    g1: LineSegment StartX=34 StartY=4 StartZ=0 EndX=-34 EndY=4 EndZ=0
    g2: LineSegment StartX=-34 StartY=4 StartZ=0 EndX=-34 EndY=59 EndZ=0
    g3: GeomPoint X=0 Y=35 Z=0
    g4: ArcOfCircle CenterX=-27 CenterY=59 CenterZ=0 NormalX=0 NormalY=0 NormalZ=1 AngleXU=0 Radius=7 StartAngle=1.5708 EndAngle=3.14159
    g5: GeomPoint X=-34 Y=66 Z=0
    g6: ArcOfCircle CenterX=27 CenterY=59 CenterZ=0 NormalX=0 NormalY=0 NormalZ=1 AngleXU=0 Radius=7 StartAngle=0 EndAngle=1.5708
    g7: GeomPoint X=34 Y=66 Z=0
    g8: LineSegment StartX=-27 StartY=66 StartZ=0 EndX=27 EndY=66 EndZ=0
  constraints (21):
    c: Coincident(g0,g1)
    c: Coincident(g1,g2)
    c: Horizontal(g1)
    c: Vertical(g0)
    c: Vertical(g2)
    c: Symmetric(g1,g7,g3)
    c: PointOnObject(g3,g-2)
    c: DistanceY(g1) = 4
    c: Vertical(g0,g-3)
    c: DistanceY(g5) = 66
    c: PointOnObject(g5,g2)
    c: PointOnObject(g7,g0)
    c: Equal(g4,g6)
    c: Radius(g4) = 7
    c: Tangent(g6,g8) = 1.5708
    c: Tangent(g6,g0) = 1.5708
    c: Tangent(g8,g4) = 1.5708
    c: Tangent(g2,g4) = 1.5708
    c: Horizontal(g8)
    c: PointOnObject(g5,g8)
    c: PointOnObject(g7,g8)
FEATURE [PartDesign::Pad] Pad013
  BaseFeature = -> Pad012
  Direction = (0,-1,2e-16)
  Length = 2
  Length2 = 10
  Placement = pos=(0,0,0) rot=(0.57735,0.57735,0.57735;2.0944rad)
  Profile = -> Sketch044
  ReferenceAxis = -> Sketch044 [N_Axis]
  Reversed = true
  Type = 0
FEATURE [PartDesign::Pad] Pad010
  Direction = (0,0,1)
  Length = 1305.01
  Length2 = 10
  Profile = -> Binder015
  Type = 0
  expr: Length = <<length>>.Length - 6 mm
FEATURE [Spreadsheet::Sheet] Spreadsheet001  label="bar_Properties"
  cells = B2=10; D2(offset_center)==module#<<Properties>>.module_width + 5 mm; B3=60; B4==(<<wall>>.Constraints.distance - 3 mm - offset_center) / 1 mm; B5==(<<wall>>.Constraints.distance - 3 mm + offset_center) / 1 mm; B6==(<<length>>.Length - 6 mm - B2 * 1 mm) / 1 mm; B7==(<<length>>.Length - 6 mm - B3 * 1 mm) / 1 mm; B8==(<<length>>.Length - 6 mm - B4 * 1 mm) / 1 mm; B9==(<<length>>.Length - 6 mm - B5 * 1 mm) / 1 mm
FEATURE [Part::FeaturePython] LinearArray004  # WARN: FeaturePython — macro-defined, semantics opaque (R4)
  Alignment = 0
  CellStart = B2
  Count = 5
  Dir = (0,0,1)
  DirIsDriven = true
  DistributionLaw = 0
  DrivenProperty = 1
  EndInclusive = true
  ExposePlacement = false
  GeneratorMode = 0
  MarkerShape = 1
  MarkerSize = 0
  NumElements = 8
  OrientMode = 0
  Point = (0,0,0)
  PointIsDriven = true
  Reverse = false
  SpanEnd = 20
  SpanStart = 0
  SpreadsheetLink = -> Spreadsheet001
  Step = 5
  Type = lattice2LinearArray.LinearArray
  VSGVersion = 1
  Values = 10 | 60 | 173.00241873258835 | 479.00241873258835 | 1295.009674930353 | 1245.009674930353 | 1132.0072561977645 | 826.0072561977646
  ValuesSource = 1
  isLattice = 1
FEATURE [Part::FeaturePython] Populate014  label="Populate LinearArray004 with Join001"  # WARN: FeaturePython — macro-defined, semantics opaque (R4)
  Copying = 0
  ExposePlacement = false
  MarkerShape = 1
  MarkerSize = 0
  NumElements = 16
  Object = -> Join001
  OutputCompounding = 0
  Placement = pos=(0,-3,0) rot=(0,0,1;0rad)
  PlacementsTo = -> LinearArray004
  Referencing = 0
  Type = lattice2PopulateCopies.LatticePopulateCopies
  isLattice = 1
FEATURE [Part::Cylinder] Cylinder  label="hole_3.4_mm"
  Angle = 360
  AttacherType = Attacher::AttachEngine3D
  FirstAngle = 0
  Height = 20
  Radius = 1.7
  SecondAngle = 0
FEATURE [Part::FeaturePython] Populate015  label="Populate Populate LinearArray004 with Join001 with Cylinder"  # WARN: FeaturePython — macro-defined, semantics opaque (R4)
  Copying = 0
  ExposePlacement = false
  MarkerShape = 1
  MarkerSize = 0
  NumElements = 0
  Object = -> Cylinder
  OutputCompounding = 1
  PlacementsTo = -> Populate014
  Referencing = 0
  Type = lattice2PopulateCopies.LatticePopulateCopies
  isLattice = 0
FEATURE [Part::Compound] Compound013  label="bar_cut1"
  Links = -> [Populate012,Populate015]
FEATURE [PartDesign::Fillet] Fillet001
  Base = -> Pad010 [Edge48]
  BaseFeature = -> Pad010
  Radius = 2
  SupportTransform = false
  UseAllEdges = false
FEATURE [PartDesign::Mirrored] Mirrored005
  MirrorPlane = -> YZ_Plane012
FEATURE [PartDesign::Plane] DatumPlane002
  AttachmentOffset = pos=(0,0,652.505) rot=(0,0,1;0rad)
  Length = 79.6619
  MapMode = 5
  Placement = pos=(0,0,652.505) rot=(0,0,1;0rad)
  ResizeMode = 0
  Support = -> [XY_Plane012]
  Width = 61.6619
  expr: .AttachmentOffset.Base.z = Pad010.Length / 2
FEATURE [PartDesign::Mirrored] Mirrored006
  MirrorPlane = -> DatumPlane002
FEATURE [Sketcher::SketchObject] Sketch045
  ExternalGeometry = -> [Binder015]
  FullyConstrained = true
  MapMode = 5
  Support = -> [XY_Plane012]
  sketch-geometry (12):
    g0: LineSegment StartX=0 StartY=14 StartZ=0 EndX=16 EndY=14 EndZ=0
    g1: LineSegment StartX=16 StartY=14 StartZ=0 EndX=16 EndY=12 EndZ=0
    g2: LineSegment StartX=16 StartY=12 StartZ=0 EndX=0 EndY=12 EndZ=0
    g3: LineSegment StartX=0 StartY=12 StartZ=0 EndX=0 EndY=14 EndZ=0
    g4: LineSegment StartX=18 StartY=4 StartZ=0 EndX=20 EndY=4 EndZ=0
    g5: LineSegment StartX=20 StartY=4 StartZ=0 EndX=20 EndY=12 EndZ=0
    g6: LineSegment StartX=20 StartY=12 StartZ=0 EndX=18 EndY=12 EndZ=0
    g7: LineSegment StartX=18 StartY=12 StartZ=0 EndX=18 EndY=4 EndZ=0
    g8: LineSegment StartX=22 StartY=2 StartZ=0 EndX=34 EndY=2 EndZ=0
    g9: LineSegment StartX=34 StartY=2 StartZ=0 EndX=34 EndY=0 EndZ=0
    g10: LineSegment StartX=34 StartY=0 StartZ=0 EndX=22 EndY=0 EndZ=0
    g11: LineSegment StartX=22 StartY=0 StartZ=0 EndX=22 EndY=2 EndZ=0
  constraints (30):
    c: Coincident(g0,g1)
    c: Coincident(g1,g2)
    c: Coincident(g2,g3)
    c: Coincident(g3,g0)
    c: Horizontal(g2)
    c: Vertical(g1)
    c: Vertical(g3)
    c: Coincident(g0,g-5)
    c: Coincident(g4,g5)
    c: Coincident(g5,g6)
    c: Coincident(g6,g7)
    c: Coincident(g7,g4)
    c: Horizontal(g4)
    c: Horizontal(g6)
    c: Vertical(g5)
    c: Coincident(g4,g-4)
    c: Coincident(g8,g9)
    c: Coincident(g9,g10)
    c: Coincident(g10,g11)
    c: Coincident(g11,g8)
    c: Horizontal(g10)
    c: Vertical(g9)
    c: Vertical(g11)
    c: Coincident(g8,g-3)
    c: PointOnObject(g9,g-1)
    c: Coincident(g8,g-3)
    c: Equal(g11,g4)
    c: Equal(g4,g1)
    c: Coincident(g0,g-5)
    c: Coincident(g6,g-4)
FEATURE [PartDesign::Pocket] Pocket008
  BaseFeature = -> Fillet001
  Direction = (0,0,-1)
  Length = 5
  Length2 = 5
  Profile = -> Sketch045
  ReferenceAxis = -> Sketch045 [N_Axis]
  Type = 0
FEATURE [PartDesign::MultiTransform] MultiTransform
  BaseFeature = -> Pocket008
  Originals = -> [Fillet001,Pocket008]
  Refine = true
  Transformations = -> [Mirrored005,Mirrored006]
FEATURE [PartDesign::Boolean] Boolean005
  BaseFeature = -> MultiTransform
  Group = -> [Compound013]
  Type = 1
FEATURE [PartDesign::Body] Body009  label="bar_material_0.50ansi"
  Group = -> [Binder014,Binder015,Pad010,Fillet001,Pocket008,MultiTransform,Mirrored005,DatumPlane002,Mirrored006,Sketch045,Boolean005]
  Origin = -> Origin012
  Tip = -> Boolean005
FEATURE [Sketcher::SketchObject] Sketch046
  FullyConstrained = true
  expr: Constraints[17] = <<Properties>>.rivet_d
  sketch-geometry (9):
    g0: LineSegment StartX=-27.5 StartY=-25 StartZ=0 EndX=-27.5 EndY=25 EndZ=0
    g1: LineSegment StartX=-27.5 StartY=25 StartZ=0 EndX=27.5 EndY=25 EndZ=0
    g2: LineSegment StartX=27.5 StartY=25 StartZ=0 EndX=27.5 EndY=-25 EndZ=0
    g3: LineSegment StartX=27.5 StartY=-25 StartZ=0 EndX=-27.5 EndY=-25 EndZ=0
    g4: GeomPoint X=0 Y=0 Z=0
    g5: Circle CenterX=27.5 CenterY=25 CenterZ=0 NormalX=0 NormalY=0 NormalZ=1 AngleXU=0 Radius=1.7
    g6: Circle CenterX=27.5 CenterY=-25 CenterZ=0 NormalX=0 NormalY=0 NormalZ=1 AngleXU=0 Radius=1.7
    g7: Circle CenterX=-27.5 CenterY=25 CenterZ=0 NormalX=0 NormalY=0 NormalZ=1 AngleXU=0 Radius=1.7
    g8: Circle CenterX=-27.5 CenterY=-25 CenterZ=0 NormalX=0 NormalY=0 NormalZ=1 AngleXU=0 Radius=1.7
  constraints (20):
    c: Coincident(g0,g1)
    c: Coincident(g1,g2)
    c: Coincident(g2,g3)
    c: Coincident(g3,g0)
    c: Horizontal(g1)
    c: Horizontal(g3)
    c: Vertical(g0)
    c: Vertical(g2)
    c: Symmetric(g1,g0,g4)
    c: Coincident(g4,g-1)
    c: Coincident(g5,g1)
    c: Coincident(g6,g2)
    c: Coincident(g7,g0)
    c: Coincident(g8,g0)
    c: Equal(g5,g7)
    c: Equal(g5,g8)
    c: Equal(g5,g6)
    c: Diameter(g5) = 3.4
    c: DistanceX(g1,g1) = 55
    c: DistanceY(g2,g2) = 50
FEATURE [Part::Extrusion] Extrude009
  Base = -> Sketch046
  Dir = (0,0,1)
  DirMode = 2
  FaceMakerClass = Part::FaceMakerBullseye
  LengthFwd = 10
  LengthRev = 0
  Placement = pos=(0,37,-3) rot=(0,0,1;0rad)
  Solid = true
  Symmetric = false
FEATURE [Part::Compound] Compound014  label="bar_fix_cut1"
  Links = -> [Populate015,Extrude009]
FEATURE [PartDesign::Boolean] Boolean006
  BaseFeature = -> Pad013
  Group = -> [Compound014]
  Type = 1
FEATURE [PartDesign::Body] Body010  label="bar_fix_material_0.50ansi"
  Group = -> [Sketch042,Sketch043,Pad011,Pad012,Sketch044,Pad013,Boolean006]
  Origin = -> Origin013
  Tip = -> Boolean006
FEATURE [Part::Feature] Unfold  label="bar_fix_unfold"
  shape: bbox 68 x 134.7 x 2 mm, 18 faces (baked)
FEATURE [Sketcher::SketchObject] Unfold_Sketch_Outline
  FullyConstrained = true
FEATURE [Sketcher::SketchObject] Unfold_Sketch_bends  label="bar_fix_Sketch_bends"
  FullyConstrained = false
  sketch-geometry (1):
    g0: LineSegment StartX=1.64381 StartY=-34 StartZ=0 EndX=1.64381 EndY=34 EndZ=0
FEATURE [Sketcher::SketchObject] Unfold_Sketch  label="bar_fix_Sketch"
  ExternalGeometry = -> [Unfold_Sketch_bends]
  FullyConstrained = false
  sketch-geometry (18):
    g0: LineSegment StartX=-62.7124 StartY=27 StartZ=0 EndX=-62.7124 EndY=-27 EndZ=0
    g1: LineSegment StartX=72 StartY=27 StartZ=0 EndX=72 EndY=-27 EndZ=0
    g2: Circle CenterX=-56.7124 CenterY=29.3 CenterZ=0 NormalX=0 NormalY=0 NormalZ=-1 AngleXU=-1.5708 Radius=1.7
    g3: Circle CenterX=-56.7124 CenterY=-29.3 CenterZ=0 NormalX=0 NormalY=0 NormalZ=-1 AngleXU=1.5708 Radius=1.7
    g4: Circle CenterX=62 CenterY=27.5 CenterZ=0 NormalX=0 NormalY=0 NormalZ=-1 AngleXU=-1.5708 Radius=1.7
    g5: Circle CenterX=62 CenterY=-27.5 CenterZ=0 NormalX=0 NormalY=0 NormalZ=-1 AngleXU=-1.5708 Radius=1.7
    g6: Circle CenterX=-6.71239 CenterY=29.3 CenterZ=0 NormalX=0 NormalY=0 NormalZ=-1 AngleXU=-1.5708 Radius=1.7
    g7: Circle CenterX=-6.71239 CenterY=-29.3 CenterZ=0 NormalX=0 NormalY=0 NormalZ=-1 AngleXU=1.5708 Radius=1.7
    g8: Circle CenterX=12 CenterY=27.5 CenterZ=0 NormalX=0 NormalY=0 NormalZ=-1 AngleXU=-1.5708 Radius=1.7
    g9: Circle CenterX=12 CenterY=-27.5 CenterZ=0 NormalX=0 NormalY=0 NormalZ=-1 AngleXU=-1.5708 Radius=1.7
    g10: LineSegment StartX=65 StartY=-34 StartZ=0 EndX=-55.7124 EndY=-34 EndZ=0
    g11: LineSegment StartX=-55.7124 StartY=34 StartZ=0 EndX=65 EndY=34 EndZ=0
    g12: LineSegment StartX=1.64381 StartY=34 StartZ=0 EndX=1.64381 EndY=32 EndZ=0
    g13: LineSegment StartX=1.64381 StartY=-34 StartZ=0 EndX=1.64381 EndY=-32 EndZ=0
    g14: ArcOfCircle CenterX=65 CenterY=-27 CenterZ=0 NormalX=0 NormalY=0 NormalZ=1 AngleXU=0 Radius=7 StartAngle=4.71239 EndAngle=6.28319
    g15: ArcOfCircle CenterX=65 CenterY=27 CenterZ=0 NormalX=0 NormalY=0 NormalZ=1 AngleXU=0 Radius=7 StartAngle=-4.698e-13 EndAngle=1.5708
    g16: ArcOfCircle CenterX=-55.7124 CenterY=27 CenterZ=0 NormalX=0 NormalY=0 NormalZ=1 AngleXU=0 Radius=7 StartAngle=1.5708 EndAngle=3.14159
    g17: ArcOfCircle CenterX=-55.7124 CenterY=-27 CenterZ=0 NormalX=0 NormalY=0 NormalZ=1 AngleXU=0 Radius=7 StartAngle=3.14159 EndAngle=4.71239
  constraints (18):
    c: Block(g11)
    c: Block(g10)
    c: Block(g1)
    c: Block(g0)
    c: Coincident(g12,g-3)
    c: PointOnObject(g12,g-3)
    c: Coincident(g13,g-3)
    c: PointOnObject(g13,g-3)
    c: Equal(g13,g12)
    c: Distance(g12) = 2
    c: Tangent(g14,g10) = 1.5708
    c: Tangent(g14,g1) = 1.5708
    c: Tangent(g15,g1) = 1.5708
    c: Tangent(g15,g11) = 1.5708
    c: Tangent(g16,g11) = 1.5708
    c: Tangent(g16,g0) = -1.5708
    c: Coincident(g17,g10)
    c: Tangent(g17,g0) = -1.5708
FEATURE [TechDraw::DrawSVGTemplate] Template
  Height = 210
  Orientation = 1
  Template = <path>
  Width = 297
FEATURE [TechDraw::DrawViewPart] View
  CoarseView = false
  Direction = (1,0,0)
  Focus = 100
  HardHidden = false
  IsoCount = 0
  IsoHidden = false
  IsoVisible = false
  LockPosition = false
  Perspective = false
  Rotation = 0
  ScaleType = 0
  ScrubCount = 0
  SeamHidden = false
  SeamVisible = true
  SmoothHidden = false
  SmoothVisible = true
  Source = -> [Body010]
  X = 88.5
  XDirection = (0,1,0)
  Y = 105
FEATURE [TechDraw::DrawViewPart] View001
  CoarseView = false
  Direction = (-0.57735,0.57735,0.57735)
  Focus = 100
  HardHidden = false
  IsoCount = 0
  IsoHidden = false
  IsoVisible = false
  LockPosition = false
  Perspective = false
  Rotation = 0
  ScaleType = 0
  ScrubCount = 0
  SeamHidden = false
  SeamVisible = true
  SmoothHidden = false
  SmoothVisible = true
  Source = -> [Body010]
  X = 208.5
  XDirection = (-0.707107,-0.707107,0)
  Y = 105
FEATURE [TechDraw::DrawViewPart] View002
  CoarseView = false
  Direction = (0,0,1)
  Focus = 100
  HardHidden = false
  IsoCount = 0
  IsoHidden = false
  IsoVisible = false
  LockPosition = false
  Perspective = false
  Rotation = 0
  ScaleType = 0
  ScrubCount = 0
  SeamHidden = false
  SeamVisible = true
  SmoothHidden = false
  SmoothVisible = true
  Source = -> [Body009]
  X = 148.5
  XDirection = (1,0,0)
  Y = 35
FEATURE [TechDraw::DrawViewDimension] Dimension
  AngleOverride = false
  Arbitrary = false
  ArbitraryTolerances = false
  EqualTolerance = true
  ExtensionAngle = 0
  FormatSpec = R%.2w
  FormatSpecOverTolerance = %+.2w
  FormatSpecUnderTolerance = %+.2w
  Inverted = false
  LineAngle = 0
  LockPosition = false
  MeasureType = 1
  OverTolerance = 0
  References2D = -> [View]
  Rotation = 0
  ScaleType = 0
  TheoreticalExact = false
  Type = 4
  UnderTolerance = 0
  X = -13.2254
  Y = -6.00761
FEATURE [TechDraw::DrawViewDimension] Dimension001
  AngleOverride = false
  Arbitrary = false
  ArbitraryTolerances = false
  EqualTolerance = true
  ExtensionAngle = 0
  FormatSpec = %.2w
  FormatSpecOverTolerance = %+.2w
  FormatSpecUnderTolerance = %+.2w
  Inverted = false
  LineAngle = 0
  LockPosition = false
  MeasureType = 1
  OverTolerance = 0
  References2D = -> [View]
  Rotation = 0
  ScaleType = 0
  TheoreticalExact = false
  Type = 1
  UnderTolerance = 0
  X = -2.13e-14
  Y = -28.5
FEATURE [TechDraw::DrawViewDimension] Dimension002
  AngleOverride = false
  Arbitrary = false
  ArbitraryTolerances = false
  EqualTolerance = true
  ExtensionAngle = 0
  FormatSpec = %.2w
  FormatSpecOverTolerance = %+.2w
  FormatSpecUnderTolerance = %+.2w
  Inverted = false
  LineAngle = 0
  LockPosition = false
  MeasureType = 1
  OverTolerance = 0
  References2D = -> [View]
  Rotation = 0
  ScaleType = 0
  TheoreticalExact = false
  Type = 2
  UnderTolerance = 0
  X = -50.7409
  Y = -0.429664
FEATURE [TechDraw::DrawPage] Page
  KeepUpdated = true
  NextBalloonIndex = 1
  ProjectionType = 0
  Template = -> Template
  Views = -> [View,View001,Dimension,Dimension001,Dimension002]
FEATURE [App::DocumentObjectGroup] Group003  label="bar_fix_Group"
  Group = -> [Unfold,Unfold_Sketch,Unfold_Sketch_Outline,Unfold_Sketch_bends,Page]
FEATURE [TechDraw::DrawViewPart] View003
  CoarseView = false
  Direction = (0,-1,0)
  Focus = 100
  HardHidden = false
  IsoCount = 0
  IsoHidden = false
  IsoVisible = false
  LockPosition = false
  Perspective = false
  Rotation = 0
  Scale = 0.2
  ScaleType = 1
  ScrubCount = 0
  SeamHidden = false
  SeamVisible = true
  SmoothHidden = false
  SmoothVisible = true
  Source = -> [Body009]
  X = 148.5
  XDirection = (0,0,-1)
  Y = 115
FEATURE [TechDraw::DrawViewPart] View004
  CoarseView = false
  Direction = (-0.57735,-0.57735,0.57735)
  Focus = 100
  HardHidden = false
  IsoCount = 0
  IsoHidden = false
  IsoVisible = false
  LockPosition = false
  Perspective = false
  Rotation = 90
  Scale = 0.25
  ScaleType = 1
  ScrubCount = 0
  SeamHidden = false
  SeamVisible = true
  SmoothHidden = false
  SmoothVisible = true
  Source = -> [Body009]
  X = 148.5
  XDirection = (0.707107,-0.707107,0)
  Y = 175
FEATURE [TechDraw::DrawViewDimension] Dimension003
  AngleOverride = false
  Arbitrary = false
  ArbitraryTolerances = false
  EqualTolerance = true
  ExtensionAngle = 0
  FormatSpec = %.2w
  FormatSpecOverTolerance = %+.2w
  FormatSpecUnderTolerance = %+.2w
  Inverted = false
  LineAngle = 0
  LockPosition = false
  MeasureType = 1
  OverTolerance = 0
  References2D = -> [View002]
  Rotation = 0
  ScaleType = 0
  TheoreticalExact = false
  Type = 1
  UnderTolerance = 0
  X = -26.8414
  Y = -10.353
FEATURE [TechDraw::DrawViewDimension] Dimension004
  AngleOverride = false
  Arbitrary = false
  ArbitraryTolerances = false
  EqualTolerance = true
  ExtensionAngle = 0
  FormatSpec = %.2w
  FormatSpecOverTolerance = %+.2w
  FormatSpecUnderTolerance = %+.2w
  Inverted = false
  LineAngle = 0
  LockPosition = false
  MeasureType = 1
  OverTolerance = 0
  References2D = -> [View002]
  Rotation = 0
  ScaleType = 0
  TheoreticalExact = false
  Type = 2
  UnderTolerance = 0
  X = -45.5088
  Y = 2.40827
FEATURE [TechDraw::DrawViewDimension] Dimension005
  AngleOverride = false
  Arbitrary = false
  ArbitraryTolerances = false
  EqualTolerance = true
  ExtensionAngle = 0
  FormatSpec = %.2w
  FormatSpecOverTolerance = %+.2w
  FormatSpecUnderTolerance = %+.2w
  Inverted = false
  LineAngle = 0
  LockPosition = false
  MeasureType = 1
  OverTolerance = 0
  References2D = -> [View002]
  Rotation = 0
  ScaleType = 0
  TheoreticalExact = false
  Type = 1
  UnderTolerance = 0
  X = -1.48432
  Y = 25.7961
FEATURE [TechDraw::DrawPage] Page001
  KeepUpdated = true
  NextBalloonIndex = 1
  ProjectionType = 0
  Template = -> Template
  Views = -> [View002,View003,View004,Dimension003,Dimension004,Dimension005]
FEATURE [TechDraw::DrawViewPart] View005
  CoarseView = false
  Direction = (0.860094,0.496575,0.116841)
  Focus = 100
  HardHidden = false
  IsoCount = 0
  IsoHidden = false
  IsoVisible = false
  LockPosition = false
  Perspective = false
  Rotation = 0
  Scale = 0.5
  ScaleType = 2
  ScrubCount = 0
  SeamHidden = false
  SeamVisible = true
  SmoothHidden = false
  SmoothVisible = true
  Source = -> [Body007]
  X = 198.5
  XDirection = (-0.5,0.866026,6.17049e-07)
  Y = 145
FEATURE [TechDraw::DrawViewPart] View006
  CoarseView = false
  Direction = (1,0,0)
  Focus = 100
  HardHidden = false
  IsoCount = 0
  IsoHidden = false
  IsoVisible = false
  LockPosition = false
  Perspective = false
  Rotation = 0
  ScaleType = 1
  ScrubCount = 0
  SeamHidden = false
  SeamVisible = true
  SmoothHidden = false
  SmoothVisible = true
  Source = -> [Body007]
  X = 63.5
  XDirection = (0,1,0)
  Y = 145
FEATURE [TechDraw::DrawViewPart] View007
  CoarseView = false
  Direction = (0,1,0)
  Focus = 100
  HardHidden = false
  IsoCount = 0
  IsoHidden = false
  IsoVisible = false
  LockPosition = false
  Perspective = false
  Rotation = 0
  Scale = 0.375
  ScaleType = 1
  ScrubCount = 0
  SeamHidden = false
  SeamVisible = true
  SmoothHidden = false
  SmoothVisible = true
  Source = -> [Body007]
  X = 148.5
  XDirection = (-1,0,0)
  Y = 55
FEATURE [TechDraw::DrawPage] Page002
  KeepUpdated = true
  NextBalloonIndex = 1
  ProjectionType = 0
  Template = -> Template
  Views = -> [View005,View006,View007]
FEATURE [Part::Feature] Unfold001
  shape: bbox 90.85 x 2 x 1252 mm, 38 faces (baked)
FEATURE [Sketcher::SketchObject] Unfold_Sketch_Outline001
  FullyConstrained = false
  sketch-geometry (8):
    g0: LineSegment StartX=0 StartY=-32 StartZ=0 EndX=0 EndY=54.8496 EndZ=0
    g1: ArcOfCircle CenterX=2 CenterY=54.8496 CenterZ=0 NormalX=0 NormalY=0 NormalZ=1 AngleXU=-3.14159 Radius=2 StartAngle=4.71239 EndAngle=6.28319
    g2: LineSegment StartX=2 StartY=56.8496 StartZ=0 EndX=1250.48 EndY=56.8496 EndZ=0
    g3: ArcOfCircle CenterX=1250.48 CenterY=54.8496 CenterZ=0 NormalX=0 NormalY=0 NormalZ=1 AngleXU=0 Radius=2 StartAngle=0 EndAngle=1.5708
    g4: LineSegment StartX=1252.48 StartY=-32 StartZ=0 EndX=1252.48 EndY=54.8496 EndZ=0
    g5: ArcOfCircle CenterX=1250.48 CenterY=-32 CenterZ=0 NormalX=0 NormalY=0 NormalZ=1 AngleXU=2e-16 Radius=2 StartAngle=4.71239 EndAngle=6.28319
    g6: LineSegment StartX=2 StartY=-34 StartZ=0 EndX=1250.48 EndY=-34 EndZ=0
    g7: ArcOfCircle CenterX=2 CenterY=-32 CenterZ=0 NormalX=0 NormalY=0 NormalZ=1 AngleXU=3.14159 Radius=2 StartAngle=0 EndAngle=1.5708
FEATURE [Sketcher::SketchObject] Unfold_Sketch_Internal
  FullyConstrained = false
  sketch-geometry (28):
    g0: LineSegment StartX=1155.98 StartY=15.1707 StartZ=0 EndX=1155.98 EndY=19.4248 EndZ=0
    g1: ArcOfCircle CenterX=1152.48 CenterY=19.4248 CenterZ=0 NormalX=0 NormalY=0 NormalZ=1 AngleXU=-4e-16 Radius=3.5 StartAngle=2e-16 EndAngle=3.14159
    g2: LineSegment StartX=1148.98 StartY=19.4248 StartZ=0 EndX=1148.98 EndY=15.1707 EndZ=0
    g3: ArcOfCircle CenterX=1146.98 CenterY=15.1707 CenterZ=0 NormalX=0 NormalY=0 NormalZ=1 AngleXU=-4e-16 Radius=2 StartAngle=5.32983 EndAngle=6.28319
    g4: ArcOfCircle CenterX=1152.48 CenterY=7.42478 CenterZ=0 NormalX=0 NormalY=0 NormalZ=1 AngleXU=-4e-16 Radius=7.5 StartAngle=2.18823 EndAngle=7.23654
    g5: ArcOfCircle CenterX=1157.98 CenterY=15.1707 CenterZ=0 NormalX=0 NormalY=0 NormalZ=1 AngleXU=-4e-16 Radius=2 StartAngle=3.14159 EndAngle=4.09495
    g6: LineSegment StartX=103.5 StartY=15.1707 StartZ=0 EndX=103.5 EndY=19.4248 EndZ=0
    g7: ArcOfCircle CenterX=100 CenterY=19.4248 CenterZ=0 NormalX=0 NormalY=0 NormalZ=1 AngleXU=-4e-16 Radius=3.5 StartAngle=2e-16 EndAngle=3.14159
    g8: LineSegment StartX=96.5 StartY=19.4248 StartZ=0 EndX=96.5 EndY=15.1707 EndZ=0
    g9: ArcOfCircle CenterX=94.5 CenterY=15.1707 CenterZ=0 NormalX=0 NormalY=0 NormalZ=1 AngleXU=-4e-16 Radius=2 StartAngle=5.32983 EndAngle=6.28319
    g10: ArcOfCircle CenterX=100 CenterY=7.42478 CenterZ=0 NormalX=0 NormalY=0 NormalZ=1 AngleXU=-4e-16 Radius=7.5 StartAngle=2.18823 EndAngle=7.23654
    g11: ArcOfCircle CenterX=105.5 CenterY=15.1707 CenterZ=0 NormalX=0 NormalY=0 NormalZ=1 AngleXU=-4e-16 Radius=2 StartAngle=3.14159 EndAngle=4.09495
    g12: Circle CenterX=465.87 CenterY=52.1496 CenterZ=0 NormalX=0 NormalY=0 NormalZ=-1 AngleXU=-1.5708 Radius=1.7
    g13: Circle CenterX=465.87 CenterY=-29.3 CenterZ=0 NormalX=0 NormalY=0 NormalZ=-1 AngleXU=1.5708 Radius=1.7
    g14: Circle CenterX=60 CenterY=52.1496 CenterZ=0 NormalX=0 NormalY=0 NormalZ=-1 AngleXU=-1.5708 Radius=1.7
    g15: Circle CenterX=10 CenterY=52.1496 CenterZ=0 NormalX=0 NormalY=0 NormalZ=-1 AngleXU=-1.5708 Radius=1.7
    g16: Circle CenterX=60 CenterY=-29.3 CenterZ=0 NormalX=0 NormalY=0 NormalZ=-1 AngleXU=1.5708 Radius=1.7
    g17: Circle CenterX=10 CenterY=-29.3 CenterZ=0 NormalX=0 NormalY=0 NormalZ=-1 AngleXU=1.5708 Radius=1.7
    g18: Circle CenterX=159.87 CenterY=52.1496 CenterZ=0 NormalX=0 NormalY=0 NormalZ=-1 AngleXU=-1.5708 Radius=1.7
    g19: Circle CenterX=159.87 CenterY=-29.3 CenterZ=0 NormalX=0 NormalY=0 NormalZ=-1 AngleXU=1.5708 Radius=1.7
    g20: Circle CenterX=1192.48 CenterY=52.1496 CenterZ=0 NormalX=0 NormalY=0 NormalZ=-1 AngleXU=-1.5708 Radius=1.7
    g21: Circle CenterX=1092.61 CenterY=52.1496 CenterZ=0 NormalX=0 NormalY=0 NormalZ=-1 AngleXU=-1.5708 Radius=1.7
    g22: Circle CenterX=786.611 CenterY=52.1496 CenterZ=0 NormalX=0 NormalY=0 NormalZ=-1 AngleXU=-1.5708 Radius=1.7
    g23: Circle CenterX=1242.48 CenterY=52.1496 CenterZ=0 NormalX=0 NormalY=0 NormalZ=-1 AngleXU=-1.5708 Radius=1.7
    g24: Circle CenterX=786.611 CenterY=-29.3 CenterZ=0 NormalX=0 NormalY=0 NormalZ=-1 AngleXU=1.5708 Radius=1.7
    g25: Circle CenterX=1092.61 CenterY=-29.3 CenterZ=0 NormalX=0 NormalY=0 NormalZ=-1 AngleXU=1.5708 Radius=1.7
    g26: Circle CenterX=1192.48 CenterY=-29.3 CenterZ=0 NormalX=0 NormalY=0 NormalZ=-1 AngleXU=1.5708 Radius=1.7
    g27: Circle CenterX=1242.48 CenterY=-29.3 CenterZ=0 NormalX=0 NormalY=0 NormalZ=-1 AngleXU=1.5708 Radius=1.7
FEATURE [Sketcher::SketchObject] Unfold_Sketch_bends001  label="Unfold_Sketch_bends"
  FullyConstrained = false
  sketch-geometry (4):
    g0: LineSegment StartX=1252.48 StartY=42.4934 StartZ=0 EndX=0 EndY=42.4934 EndZ=0
    g1: LineSegment StartX=1252.48 StartY=29.781 StartZ=0 EndX=0 EndY=29.781 EndZ=0
    g2: LineSegment StartX=1252.48 StartY=-6.93142 StartZ=0 EndX=0 EndY=-6.93142 EndZ=0
    g3: LineSegment StartX=1252.48 StartY=-19.6438 StartZ=0 EndX=0 EndY=-19.6438 EndZ=0
FEATURE [Sketcher::SketchObject] Unfold_Sketch001  label="bar_Unfold_Sketch"
  ExternalGeometry = -> [Unfold_Sketch_bends001]
  FullyConstrained = false
  sketch-geometry (44):
    g0: LineSegment StartX=2 StartY=56.8496 StartZ=0 EndX=1250.48 EndY=56.8496 EndZ=0
    g1: ArcOfCircle CenterX=2 CenterY=54.8496 CenterZ=0 NormalX=0 NormalY=0 NormalZ=1 AngleXU=-3.14159 Radius=2 StartAngle=4.71239 EndAngle=6.28319
    g2: ArcOfCircle CenterX=1250.48 CenterY=54.8496 CenterZ=0 NormalX=0 NormalY=0 NormalZ=1 AngleXU=0 Radius=2 StartAngle=0 EndAngle=1.5708
    g3: ArcOfCircle CenterX=2 CenterY=-32 CenterZ=0 NormalX=0 NormalY=0 NormalZ=1 AngleXU=3.14159 Radius=2 StartAngle=0 EndAngle=1.5708
    g4: LineSegment StartX=2 StartY=-34 StartZ=0 EndX=1250.48 EndY=-34 EndZ=0
    g5: ArcOfCircle CenterX=1250.48 CenterY=-32 CenterZ=0 NormalX=0 NormalY=0 NormalZ=1 AngleXU=2e-16 Radius=2 StartAngle=4.71239 EndAngle=6.28319
    g6: LineSegment StartX=103.5 StartY=15.1707 StartZ=0 EndX=103.5 EndY=19.4248 EndZ=0
    g7: ArcOfCircle CenterX=100 CenterY=19.4248 CenterZ=0 NormalX=0 NormalY=0 NormalZ=1 AngleXU=-4e-16 Radius=3.5 StartAngle=2e-16 EndAngle=3.14159
    g8: LineSegment StartX=96.5 StartY=19.4248 StartZ=0 EndX=96.5 EndY=15.1707 EndZ=0
    g9: ArcOfCircle CenterX=94.5 CenterY=15.1707 CenterZ=0 NormalX=0 NormalY=0 NormalZ=1 AngleXU=-4e-16 Radius=2 StartAngle=5.32983 EndAngle=6.28319
    g10: ArcOfCircle CenterX=100 CenterY=7.42478 CenterZ=0 NormalX=0 NormalY=0 NormalZ=1 AngleXU=-4e-16 Radius=7.5 StartAngle=2.18823 EndAngle=7.23654
    g11: ArcOfCircle CenterX=105.5 CenterY=15.1707 CenterZ=0 NormalX=0 NormalY=0 NormalZ=1 AngleXU=-4e-16 Radius=2 StartAngle=3.14159 EndAngle=4.09495
    g12: LineSegment StartX=1155.98 StartY=15.1707 StartZ=0 EndX=1155.98 EndY=19.4248 EndZ=0
    g13: ArcOfCircle CenterX=1152.48 CenterY=19.4248 CenterZ=0 NormalX=0 NormalY=0 NormalZ=1 AngleXU=-4e-16 Radius=3.5 StartAngle=2e-16 EndAngle=3.14159
    g14: LineSegment StartX=1148.98 StartY=19.4248 StartZ=0 EndX=1148.98 EndY=15.1707 EndZ=0
    g15: ArcOfCircle CenterX=1146.98 CenterY=15.1707 CenterZ=0 NormalX=0 NormalY=0 NormalZ=1 AngleXU=-4e-16 Radius=2 StartAngle=5.32983 EndAngle=6.28319
    g16: ArcOfCircle CenterX=1152.48 CenterY=7.42478 CenterZ=0 NormalX=0 NormalY=0 NormalZ=1 AngleXU=-4e-16 Radius=7.5 StartAngle=2.18823 EndAngle=7.23654
    g17: ArcOfCircle CenterX=1157.98 CenterY=15.1707 CenterZ=0 NormalX=0 NormalY=0 NormalZ=1 AngleXU=-4e-16 Radius=2 StartAngle=3.14159 EndAngle=4.09495
    g18: Circle CenterX=1242.48 CenterY=52.1496 CenterZ=0 NormalX=0 NormalY=0 NormalZ=-1 AngleXU=-1.5708 Radius=1.7
    g19: Circle CenterX=786.611 CenterY=52.1496 CenterZ=0 NormalX=0 NormalY=0 NormalZ=-1 AngleXU=-1.5708 Radius=1.7
    g20: Circle CenterX=1092.61 CenterY=52.1496 CenterZ=0 NormalX=0 NormalY=0 NormalZ=-1 AngleXU=-1.5708 Radius=1.7
    g21: Circle CenterX=1192.48 CenterY=52.1496 CenterZ=0 NormalX=0 NormalY=0 NormalZ=-1 AngleXU=-1.5708 Radius=1.7
    g22: Circle CenterX=1242.48 CenterY=-29.3 CenterZ=0 NormalX=0 NormalY=0 NormalZ=-1 AngleXU=1.5708 Radius=1.7
    g23: Circle CenterX=1192.48 CenterY=-29.3 CenterZ=0 NormalX=0 NormalY=0 NormalZ=-1 AngleXU=1.5708 Radius=1.7
    g24: Circle CenterX=1092.61 CenterY=-29.3 CenterZ=0 NormalX=0 NormalY=0 NormalZ=-1 AngleXU=1.5708 Radius=1.7
    g25: Circle CenterX=786.611 CenterY=-29.3 CenterZ=0 NormalX=0 NormalY=0 NormalZ=-1 AngleXU=1.5708 Radius=1.7
    g26: Circle CenterX=60 CenterY=52.1496 CenterZ=0 NormalX=0 NormalY=0 NormalZ=-1 AngleXU=-1.5708 Radius=1.7
    g27: Circle CenterX=10 CenterY=52.1496 CenterZ=0 NormalX=0 NormalY=0 NormalZ=-1 AngleXU=-1.5708 Radius=1.7
    g28: Circle CenterX=60 CenterY=-29.3 CenterZ=0 NormalX=0 NormalY=0 NormalZ=-1 AngleXU=1.5708 Radius=1.7
    g29: Circle CenterX=10 CenterY=-29.3 CenterZ=0 NormalX=0 NormalY=0 NormalZ=-1 AngleXU=1.5708 Radius=1.7
    g30: Circle CenterX=465.87 CenterY=52.1496 CenterZ=0 NormalX=0 NormalY=0 NormalZ=-1 AngleXU=-1.5708 Radius=1.7
    g31: Circle CenterX=159.87 CenterY=52.1496 CenterZ=0 NormalX=0 NormalY=0 NormalZ=-1 AngleXU=-1.5708 Radius=1.7
    g32: Circle CenterX=465.87 CenterY=-29.3 CenterZ=0 NormalX=0 NormalY=0 NormalZ=-1 AngleXU=1.5708 Radius=1.7
    g33: Circle CenterX=159.87 CenterY=-29.3 CenterZ=0 NormalX=0 NormalY=0 NormalZ=-1 AngleXU=1.5708 Radius=1.7
    g34: LineSegment StartX=-7.5e-15 StartY=-32 StartZ=0 EndX=-4e-16 EndY=54.8496 EndZ=0
    g35: LineSegment StartX=1252.48 StartY=-32 StartZ=0 EndX=1252.48 EndY=54.8496 EndZ=0
    g36: LineSegment StartX=0 StartY=-19.6438 StartZ=0 EndX=2 EndY=-19.6438 EndZ=0
    g37: LineSegment StartX=0 StartY=-6.93142 StartZ=0 EndX=2 EndY=-6.93142 EndZ=0
    g38: LineSegment StartX=0 StartY=29.781 StartZ=0 EndX=2 EndY=29.781 EndZ=0
    g39: LineSegment StartX=0 StartY=42.4934 StartZ=0 EndX=2 EndY=42.4934 EndZ=0
    g40: LineSegment StartX=1252.48 StartY=42.4934 StartZ=0 EndX=1250.48 EndY=42.4934 EndZ=0
    g41: LineSegment StartX=1252.48 StartY=29.781 StartZ=0 EndX=1250.48 EndY=29.781 EndZ=0
    g42: LineSegment StartX=1252.48 StartY=-6.93142 StartZ=0 EndX=1250.48 EndY=-6.93142 EndZ=0
    g43: LineSegment StartX=1252.48 StartY=-19.6438 StartZ=0 EndX=1250.48 EndY=-19.6438 EndZ=0
  constraints (46):
    c: Coincident(g3,g34)
    c: Coincident(g1,g34)
    c: Coincident(g3,g4)
    c: Coincident(g0,g1)
    c: Coincident(g9,g10)
    c: Coincident(g8,g9)
    c: Coincident(g7,g8)
    c: Coincident(g6,g11)
    c: Coincident(g6,g7)
    c: Coincident(g10,g11)
    c: Coincident(g15,g16)
    c: Coincident(g14,g15)
    c: Coincident(g13,g14)
    c: Coincident(g12,g17)
    c: Coincident(g12,g13)
    c: Coincident(g16,g17)
    c: Coincident(g4,g5)
    c: Coincident(g0,g2)
    c: Coincident(g5,g35)
    c: Coincident(g2,g35)
    c: Block(g35)
    c: Block(g34)
    c: Coincident(g36,g-6)
    c: PointOnObject(g36,g-6)
    c: Coincident(g37,g-5)
    c: PointOnObject(g37,g-5)
    c: Coincident(g38,g-4)
    c: PointOnObject(g38,g-4)
    c: Coincident(g39,g-3)
    c: PointOnObject(g39,g-3)
    c: Coincident(g40,g-3)
    c: PointOnObject(g40,g-3)
    c: Coincident(g41,g-4)
    c: PointOnObject(g41,g-4)
    c: Coincident(g42,g-5)
    c: PointOnObject(g42,g-5)
    c: Coincident(g43,g-6)
    c: PointOnObject(g43,g-6)
    c: Equal(g43,g42)
    c: Equal(g42,g41)
    c: Equal(g41,g40)
    c: Equal(g40,g36)
    c: Equal(g36,g37)
    c: Equal(g37,g38)
    c: Equal(g38,g39)
    c: Distance(g36) = 2
FEATURE [App::DocumentObjectGroup] Group005  label="bar_Group"
  Group = -> [Page001,Unfold001,Unfold_Sketch001,Unfold_Sketch_Outline001,Unfold_Sketch_Internal,Unfold_Sketch_bends001]
FEATURE [Part::Feature] Unfold002
  shape: bbox 679.1 x 0.5 x 177.8 mm, 52 faces (baked)
FEATURE [Sketcher::SketchObject] Unfold_Sketch_Outline002
  FullyConstrained = false
  sketch-geometry (54):
    g0: ArcOfCircle CenterX=-0.71755 CenterY=-157.976 CenterZ=0 NormalX=0 NormalY=0 NormalZ=1 AngleXU=-1.5708 Radius=10 StartAngle=3.14159 EndAngle=5.73153
    g1: LineSegment StartX=-0.71755 StartY=-147.976 StartZ=0 EndX=3.15651 EndY=-147.976 EndZ=0
    g2: ArcOfCircle CenterX=3.15651 CenterY=-157.976 CenterZ=0 NormalX=0 NormalY=0 NormalZ=1 AngleXU=-1.5708 Radius=10 StartAngle=1.91063 EndAngle=3.14159
    g3: ArcOfCircle CenterX=17.2986 CenterY=-152.976 CenterZ=0 NormalX=0 NormalY=0 NormalZ=1 AngleXU=-1.5708 Radius=5 StartAngle=5.05223 EndAngle=6.28319
    g4: LineSegment StartX=75 StartY=-157.976 StartZ=0 EndX=17.2986 EndY=-157.976 EndZ=0
    g5: ArcOfCircle CenterX=75 CenterY=-152.976 CenterZ=0 NormalX=0 NormalY=0 NormalZ=1 AngleXU=-1.5708 Radius=5 StartAngle=0 EndAngle=1.5708
    g6: LineSegment StartX=80 StartY=152.976 StartZ=0 EndX=80 EndY=-152.976 EndZ=0
    g7: ArcOfCircle CenterX=75 CenterY=152.976 CenterZ=0 NormalX=0 NormalY=0 NormalZ=1 AngleXU=1.5708 Radius=5 StartAngle=4.71239 EndAngle=6.28319
    g8: LineSegment StartX=17.2986 StartY=157.976 StartZ=0 EndX=75 EndY=157.976 EndZ=0
    g9: ArcOfCircle CenterX=17.2986 CenterY=152.976 CenterZ=0 NormalX=0 NormalY=0 NormalZ=1 AngleXU=1.5708 Radius=5 StartAngle=0 EndAngle=1.23096
    g10: ArcOfCircle CenterX=3.15651 CenterY=157.976 CenterZ=0 NormalX=0 NormalY=0 NormalZ=1 AngleXU=1.5708 Radius=10 StartAngle=3.14159 EndAngle=4.37255
    g11: LineSegment StartX=3.15651 StartY=147.976 StartZ=0 EndX=-0.71755 EndY=147.976 EndZ=0
    g12: ArcOfCircle CenterX=-0.71755 CenterY=157.976 CenterZ=0 NormalX=0 NormalY=0 NormalZ=1 AngleXU=1.5708 Radius=10 StartAngle=0.551659 EndAngle=3.14159
    g13: BSplineCurve PolesCount=15 KnotsCount=15 Degree=1 IsPeriodic=0
    g14: LineSegment StartX=-5.87221 StartY=166.546 StartZ=0 EndX=-5.87211 EndY=166.545 EndZ=0
    g15: LineSegment StartX=-5.95924 StartY=166.494 StartZ=0 EndX=-5.95856 EndY=166.493 EndZ=0
    g16: LineSegment StartX=-2.54495 StartY=168.519 StartZ=0 EndX=-5.95924 EndY=166.494 EndZ=0
    g17: ArcOfCircle CenterX=2.55641 CenterY=159.918 CenterZ=0 NormalX=0 NormalY=0 NormalZ=1 AngleXU=2.22325 Radius=10 StartAngle=5.05223 EndAngle=6.16608
    g18: ArcOfCircle CenterX=10.758 CenterY=172.477 CenterZ=0 NormalX=0 NormalY=0 NormalZ=1 AngleXU=2.22325 Radius=5 StartAngle=1.91063 EndAngle=3.14159
    g19: LineSegment StartX=13.7937 StartY=168.504 StartZ=0 EndX=59.6431 EndY=203.537 EndZ=0
    g20: ArcOfCircle CenterX=56.6074 CenterY=207.51 CenterZ=0 NormalX=0 NormalY=0 NormalZ=1 AngleXU=2.22325 Radius=5 StartAngle=3.14159 EndAngle=4.71239
    g21: LineSegment StartX=60.5804 StartY=210.546 StartZ=0 EndX=-37.0837 EndY=338.365 EndZ=0
    g22: ArcOfCircle CenterX=-39.4675 CenterY=336.543 CenterZ=0 NormalX=0 NormalY=0 NormalZ=1 AngleXU=2.22325 Radius=3 StartAngle=4.71239 EndAngle=6.22301
    g23: LineSegment StartX=-82.0568 StartY=307.77 StartZ=0 EndX=-41.1423 EndY=339.032 EndZ=0
    g24: ArcOfCircle CenterX=-80.2354 CenterY=305.387 CenterZ=0 NormalX=0 NormalY=0 NormalZ=1 AngleXU=2.22325 Radius=3 StartAngle=0 EndAngle=1.45369
    g25: LineSegment StartX=-81.6083 StartY=301.821 StartZ=0 EndX=-82.8157 EndY=303.856 EndZ=0
    g26: LineSegment StartX=-81.6083 StartY=301.821 StartZ=0 EndX=-84.8823 EndY=299.879 EndZ=0
    g27: LineSegment StartX=-95.7983 StartY=299.879 StartZ=0 EndX=-84.8823 EndY=299.879 EndZ=0
    g28: ArcOfCircle CenterX=-95.7983 CenterY=297.879 CenterZ=0 NormalX=0 NormalY=0 NormalZ=1 AngleXU=0 Radius=2 StartAngle=1.5708 EndAngle=3.14159
    g29: LineSegment StartX=-97.7983 StartY=-297.879 StartZ=0 EndX=-97.7983 EndY=297.879 EndZ=0
    g30: ArcOfCircle CenterX=-95.7983 CenterY=-297.879 CenterZ=0 NormalX=0 NormalY=0 NormalZ=1 AngleXU=-2e-16 Radius=2 StartAngle=3.14159 EndAngle=4.71239
    g31: LineSegment StartX=-95.7983 StartY=-299.879 StartZ=0 EndX=-84.8823 EndY=-299.879 EndZ=0
    g32: LineSegment StartX=-81.6083 StartY=-301.821 StartZ=0 EndX=-84.8823 EndY=-299.879 EndZ=0
    g33: LineSegment StartX=-81.6083 StartY=-301.821 StartZ=0 EndX=-82.8157 EndY=-303.856 EndZ=0
    g34: ArcOfCircle CenterX=-80.2354 CenterY=-305.387 CenterZ=0 NormalX=0 NormalY=0 NormalZ=1 AngleXU=-2.22325 Radius=3 StartAngle=4.8295 EndAngle=6.28319
    g35: LineSegment StartX=-82.0568 StartY=-307.77 StartZ=0 EndX=-41.1423 EndY=-339.032 EndZ=0
    g36: ArcOfCircle CenterX=-39.4675 CenterY=-336.543 CenterZ=0 NormalX=0 NormalY=0 NormalZ=1 AngleXU=-2.22325 Radius=3 StartAngle=0.0601735 EndAngle=1.5708
    g37: LineSegment StartX=60.5804 StartY=-210.546 StartZ=0 EndX=-37.0837 EndY=-338.365 EndZ=0
    g38: ArcOfCircle CenterX=56.6074 CenterY=-207.51 CenterZ=0 NormalX=0 NormalY=0 NormalZ=1 AngleXU=-2.22325 Radius=5 StartAngle=1.5708 EndAngle=3.14159
    g39: LineSegment StartX=13.7937 StartY=-168.504 StartZ=0 EndX=59.6431 EndY=-203.537 EndZ=0
    g40: ArcOfCircle CenterX=10.758 CenterY=-172.477 CenterZ=0 NormalX=0 NormalY=0 NormalZ=1 AngleXU=-2.22325 Radius=5 StartAngle=3.14159 EndAngle=4.37255
    g41: ArcOfCircle CenterX=2.55641 CenterY=-159.918 CenterZ=0 NormalX=0 NormalY=0 NormalZ=1 AngleXU=-2.22325 Radius=10 StartAngle=0.117109 EndAngle=1.23096
    g42: LineSegment StartX=-5.95924 StartY=-166.494 StartZ=0 EndX=-2.54495 EndY=-168.519 EndZ=0
    g43: LineSegment StartX=-5.95924 StartY=-166.494 StartZ=0 EndX=-5.95856 EndY=-166.493 EndZ=0
    g44: BSplineCurve PolesCount=15 KnotsCount=15 Degree=1 IsPeriodic=0
    g45: LineSegment StartX=-5.87221 StartY=-166.546 StartZ=0 EndX=-5.87211 EndY=-166.545 EndZ=0
    g46: Circle CenterX=70 CenterY=0 CenterZ=0 NormalX=0 NormalY=0 NormalZ=1 AngleXU=-1.5708 Radius=1.7
    g47: Circle CenterX=30 CenterY=0 CenterZ=0 NormalX=0 NormalY=0 NormalZ=1 AngleXU=-1.5708 Radius=1.7
    g48: Circle CenterX=70 CenterY=-154 CenterZ=0 NormalX=0 NormalY=0 NormalZ=1 AngleXU=-1.5708 Radius=1.7
    g49: Circle CenterX=70 CenterY=154 CenterZ=0 NormalX=0 NormalY=0 NormalZ=1 AngleXU=-1.5708 Radius=1.7
    g50: Circle CenterX=52.6488 CenterY=-204.455 CenterZ=0 NormalX=0 NormalY=0 NormalZ=-1 AngleXU=2.22325 Radius=1.7
    g51: Circle CenterX=-42.6716 CenterY=-329.207 CenterZ=0 NormalX=0 NormalY=0 NormalZ=-1 AngleXU=2.22325 Radius=1.7
    g52: Circle CenterX=-42.6716 CenterY=329.207 CenterZ=0 NormalX=0 NormalY=0 NormalZ=1 AngleXU=-0.918344 Radius=1.7
    g53: Circle CenterX=52.6488 CenterY=204.455 CenterZ=0 NormalX=0 NormalY=0 NormalZ=1 AngleXU=-0.918344 Radius=1.7
FEATURE [Sketcher::SketchObject] Unfold_Sketch_bends002
  FullyConstrained = false
  sketch-geometry (5):
    g0: LineSegment StartX=-83.2453 StartY=-300.85 StartZ=0 EndX=-4.18193 EndY=-167.548 EndZ=0
    g1: LineSegment StartX=-88.6097 StartY=299.879 StartZ=0 EndX=-88.6097 EndY=-299.879 EndZ=0
    g2: LineSegment StartX=-85.1307 StartY=299.879 StartZ=0 EndX=-85.1307 EndY=-299.879 EndZ=0
    g3: LineSegment StartX=-83.2453 StartY=300.85 StartZ=0 EndX=-4.18193 EndY=167.548 EndZ=0
    g4: LineSegment StartX=1.21948 StartY=147.976 StartZ=0 EndX=1.21948 EndY=-147.976 EndZ=0
FEATURE [Sketcher::SketchObject] Unfold_Sketch002  label="sink_Unfold_Sketch002"
  ExternalGeometry = -> [Unfold_Sketch_bends002]
  FullyConstrained = false
  sketch-geometry (55):
    g0: ArcOfCircle CenterX=-95.7983 CenterY=-297.879 CenterZ=0 NormalX=0 NormalY=0 NormalZ=1 AngleXU=-2e-16 Radius=2 StartAngle=3.14159 EndAngle=4.71239
    g1: LineSegment StartX=-97.7983 StartY=-297.879 StartZ=0 EndX=-97.7983 EndY=297.879 EndZ=0
    g2: ArcOfCircle CenterX=-95.7983 CenterY=297.879 CenterZ=0 NormalX=0 NormalY=0 NormalZ=1 AngleXU=0 Radius=2 StartAngle=1.5708 EndAngle=3.14159
    g3: LineSegment StartX=-81.6083 StartY=301.821 StartZ=0 EndX=-84.8823 EndY=299.879 EndZ=0
    g4: LineSegment StartX=-81.6083 StartY=301.821 StartZ=0 EndX=-82.8157 EndY=303.856 EndZ=0
    g5: ArcOfCircle CenterX=-80.2354 CenterY=305.387 CenterZ=0 NormalX=0 NormalY=0 NormalZ=1 AngleXU=2.22325 Radius=3 StartAngle=0 EndAngle=1.45369
    g6: LineSegment StartX=-82.0568 StartY=307.77 StartZ=0 EndX=-41.1423 EndY=339.032 EndZ=0
    g7: ArcOfCircle CenterX=10.758 CenterY=172.477 CenterZ=0 NormalX=0 NormalY=0 NormalZ=1 AngleXU=2.22325 Radius=5 StartAngle=1.91063 EndAngle=3.14159
    g8: LineSegment StartX=13.7937 StartY=168.504 StartZ=0 EndX=59.6431 EndY=203.537 EndZ=0
    g9: ArcOfCircle CenterX=2.55641 CenterY=159.918 CenterZ=0 NormalX=0 NormalY=0 NormalZ=1 AngleXU=2.22325 Radius=10 StartAngle=5.05223 EndAngle=6.16608
    g10: ArcOfCircle CenterX=56.6074 CenterY=207.51 CenterZ=0 NormalX=0 NormalY=0 NormalZ=1 AngleXU=2.22325 Radius=5 StartAngle=3.14159 EndAngle=4.71239
    g11: LineSegment StartX=60.5804 StartY=210.546 StartZ=0 EndX=-37.0837 EndY=338.365 EndZ=0
    g12: ArcOfCircle CenterX=-39.4675 CenterY=336.543 CenterZ=0 NormalX=0 NormalY=0 NormalZ=1 AngleXU=2.22325 Radius=3 StartAngle=4.71239 EndAngle=6.22301
    g13: ArcOfCircle CenterX=-0.71755 CenterY=157.976 CenterZ=0 NormalX=0 NormalY=0 NormalZ=1 AngleXU=1.5708 Radius=10 StartAngle=0.551659 EndAngle=3.14159
    g14: ArcOfCircle CenterX=3.15651 CenterY=-157.976 CenterZ=0 NormalX=0 NormalY=0 NormalZ=1 AngleXU=-1.5708 Radius=10 StartAngle=1.91063 EndAngle=3.14159
    g15: ArcOfCircle CenterX=17.2986 CenterY=-152.976 CenterZ=0 NormalX=0 NormalY=0 NormalZ=1 AngleXU=-1.5708 Radius=5 StartAngle=5.05223 EndAngle=6.28319
    g16: LineSegment StartX=75 StartY=-157.976 StartZ=0 EndX=17.2986 EndY=-157.976 EndZ=0
    g17: ArcOfCircle CenterX=75 CenterY=-152.976 CenterZ=0 NormalX=0 NormalY=0 NormalZ=1 AngleXU=-1.5708 Radius=5 StartAngle=0 EndAngle=1.5708
    g18: LineSegment StartX=80 StartY=152.976 StartZ=0 EndX=80 EndY=-152.976 EndZ=0
    g19: ArcOfCircle CenterX=3.15651 CenterY=157.976 CenterZ=0 NormalX=0 NormalY=0 NormalZ=1 AngleXU=1.5708 Radius=10 StartAngle=3.14159 EndAngle=4.37255
    g20: ArcOfCircle CenterX=17.2986 CenterY=152.976 CenterZ=0 NormalX=0 NormalY=0 NormalZ=1 AngleXU=1.5708 Radius=5 StartAngle=0 EndAngle=1.23096
    g21: LineSegment StartX=17.2986 StartY=157.976 StartZ=0 EndX=75 EndY=157.976 EndZ=0
    g22: ArcOfCircle CenterX=75 CenterY=152.976 CenterZ=0 NormalX=0 NormalY=0 NormalZ=1 AngleXU=1.5708 Radius=5 StartAngle=4.71239 EndAngle=6.28319
    g23: ArcOfCircle CenterX=-0.71755 CenterY=-157.976 CenterZ=0 NormalX=0 NormalY=0 NormalZ=1 AngleXU=-1.5708 Radius=10 StartAngle=3.14159 EndAngle=5.73153
    g24: LineSegment StartX=-5.95924 StartY=-166.494 StartZ=0 EndX=-5.95856 EndY=-166.493 EndZ=0
    g25: ArcOfCircle CenterX=-39.4675 CenterY=-336.543 CenterZ=0 NormalX=0 NormalY=0 NormalZ=1 AngleXU=-2.22325 Radius=3 StartAngle=0.0601735 EndAngle=1.5708
    g26: LineSegment StartX=-82.0568 StartY=-307.77 StartZ=0 EndX=-41.1423 EndY=-339.032 EndZ=0
    g27: LineSegment StartX=60.5804 StartY=-210.546 StartZ=0 EndX=-37.0837 EndY=-338.365 EndZ=0
    g28: ArcOfCircle CenterX=-80.2354 CenterY=-305.387 CenterZ=0 NormalX=0 NormalY=0 NormalZ=1 AngleXU=-2.22325 Radius=3 StartAngle=4.8295 EndAngle=6.28319
    g29: ArcOfCircle CenterX=56.6074 CenterY=-207.51 CenterZ=0 NormalX=0 NormalY=0 NormalZ=1 AngleXU=-2.22325 Radius=5 StartAngle=1.5708 EndAngle=3.14159
    g30: LineSegment StartX=-81.6083 StartY=-301.821 StartZ=0 EndX=-82.8157 EndY=-303.856 EndZ=0
    g31: LineSegment StartX=13.7937 StartY=-168.504 StartZ=0 EndX=59.6431 EndY=-203.537 EndZ=0
    g32: ArcOfCircle CenterX=10.758 CenterY=-172.477 CenterZ=0 NormalX=0 NormalY=0 NormalZ=1 AngleXU=-2.22325 Radius=5 StartAngle=3.14159 EndAngle=4.37255
    g33: ArcOfCircle CenterX=2.55641 CenterY=-159.918 CenterZ=0 NormalX=0 NormalY=0 NormalZ=1 AngleXU=-2.22325 Radius=10 StartAngle=0.117109 EndAngle=1.23096
    g34: LineSegment StartX=-81.6083 StartY=-301.821 StartZ=0 EndX=-84.8823 EndY=-299.879 EndZ=0
    g35: Circle CenterX=70 CenterY=0 CenterZ=0 NormalX=0 NormalY=0 NormalZ=1 AngleXU=-1.5708 Radius=1.7
    g36: Circle CenterX=30 CenterY=0 CenterZ=0 NormalX=0 NormalY=0 NormalZ=1 AngleXU=-1.5708 Radius=1.7
    g37: Circle CenterX=70 CenterY=-154 CenterZ=0 NormalX=0 NormalY=0 NormalZ=1 AngleXU=-1.5708 Radius=1.7
    g38: Circle CenterX=70 CenterY=154 CenterZ=0 NormalX=0 NormalY=0 NormalZ=1 AngleXU=-1.5708 Radius=1.7
    g39: Circle CenterX=52.6488 CenterY=-204.455 CenterZ=0 NormalX=0 NormalY=0 NormalZ=-1 AngleXU=2.22325 Radius=1.7
    g40: Circle CenterX=-42.6716 CenterY=-329.207 CenterZ=0 NormalX=0 NormalY=0 NormalZ=-1 AngleXU=2.22325 Radius=1.7
    g41: Circle CenterX=-42.6716 CenterY=329.207 CenterZ=0 NormalX=0 NormalY=0 NormalZ=1 AngleXU=-0.918344 Radius=1.7
    g42: Circle CenterX=52.6488 CenterY=204.455 CenterZ=0 NormalX=0 NormalY=0 NormalZ=1 AngleXU=-0.918344 Radius=1.7
    g43: LineSegment StartX=-95.7983 StartY=-299.879 StartZ=0 EndX=-84.8823 EndY=-299.879 EndZ=0
    g44: LineSegment StartX=-0.71755 StartY=-147.976 StartZ=0 EndX=3.15651 EndY=-147.976 EndZ=0
    g45: LineSegment StartX=3.15651 StartY=147.976 StartZ=0 EndX=-0.71755 EndY=147.976 EndZ=0
    g46: LineSegment StartX=-95.7983 StartY=299.879 StartZ=0 EndX=-84.8823 EndY=299.879 EndZ=0
    g47: LineSegment StartX=-2.54495 StartY=-168.519 StartZ=0 EndX=-5.95856 EndY=-166.493 EndZ=0
    g48: LineSegment StartX=-5.95856 StartY=166.493 StartZ=0 EndX=-2.54495 EndY=168.519 EndZ=0
    g49: LineSegment StartX=-4.18193 StartY=167.548 StartZ=0 EndX=-5.2022 EndY=169.268 EndZ=0
    g50: LineSegment StartX=1.21948 StartY=147.976 StartZ=0 EndX=1.21948 EndY=145.976 EndZ=0
    g51: LineSegment StartX=1.21948 StartY=-147.976 StartZ=0 EndX=1.21948 EndY=-145.976 EndZ=0
    g52: LineSegment StartX=-4.18193 StartY=-167.548 StartZ=0 EndX=-5.2022 EndY=-169.268 EndZ=0
    g53: LineSegment StartX=-83.2453 StartY=300.85 StartZ=0 EndX=-82.225 EndY=299.129 EndZ=0
    g54: LineSegment StartX=-83.2453 StartY=-300.85 StartZ=0 EndX=-82.225 EndY=-299.129 EndZ=0
  constraints (65):
    c: Coincident(g0,g1)
    c: Coincident(g1,g2)
    c: Coincident(g0,g43)
    c: Coincident(g2,g46)
    c: Coincident(g34,g43)
    c: Coincident(g3,g46)
    c: Coincident(g28,g30)
    c: Coincident(g4,g5)
    c: Coincident(g26,g28)
    c: Coincident(g5,g6)
    c: Coincident(g30,g34)
    c: Coincident(g3,g4)
    c: Coincident(g25,g26)
    c: Coincident(g6,g12)
    c: Coincident(g25,g27)
    c: Coincident(g11,g12)
    c: Coincident(g23,g24)
    c: Coincident(g23,g44)
    c: Coincident(g13,g45)
    c: Coincident(g14,g44)
    c: Coincident(g19,g45)
    c: Coincident(g32,g33)
    c: Coincident(g7,g9)
    c: Coincident(g14,g15)
    c: Coincident(g19,g20)
    c: Coincident(g31,g32)
    c: Coincident(g7,g8)
    c: Coincident(g15,g16)
    c: Coincident(g20,g21)
    c: Coincident(g29,g31)
    c: Coincident(g8,g10)
    c: Coincident(g27,g29)
    c: Coincident(g10,g11)
    c: Coincident(g16,g17)
    c: Coincident(g21,g22)
    c: Coincident(g17,g18)
    c: Coincident(g18,g22)
    c: Block(g23)
    c: Block(g33)
    c: Block(g14)
    c: Block(g19)
    c: Block(g13)
    c: Block(g9)
    c: Coincident(g47,g33)
    c: Coincident(g47,g23)
    c: Coincident(g48,g9)
    c: Coincident(g48,g13)
    c: Coincident(g49,g-4)
    c: PointOnObject(g49,g-4)
    c: Coincident(g50,g-3)
    c: PointOnObject(g50,g-3)
    c: Coincident(g51,g-3)
    c: PointOnObject(g51,g-3)
    c: Coincident(g52,g-5)
    c: PointOnObject(g52,g-5)
    c: Equal(g52,g51)
    c: Equal(g51,g50)
    c: Equal(g50,g49)
    c: Distance(g49) = 2
    c: Coincident(g53,g-4)
    c: PointOnObject(g53,g-4)
    c: Equal(g53,g49)
    c: Coincident(g54,g-5)
    c: PointOnObject(g54,g-5)
    c: Equal(g54,g52)
FEATURE [App::DocumentObjectGroup] Group004  label="sink_Group"
  Group = -> [Page002,Unfold002,Unfold_Sketch002,Unfold_Sketch_Outline002,Unfold_Sketch_bends002]
FEATURE [Sketcher::SketchObject] Sketch048
  FullyConstrained = true
  expr: Constraints[4] = 3 mm + 28.5 mm - <<base_sketch>>.Constraints.offset
  sketch-geometry (3):
    g0: LineSegment StartX=0 StartY=5 StartZ=0 EndX=0 EndY=0 EndZ=0
    g1: LineSegment StartX=0 StartY=0 StartZ=0 EndX=-10.5 EndY=-15 EndZ=0
    g2: LineSegment StartX=-10.5 StartY=-15 StartZ=0 EndX=-15.5 EndY=-5 EndZ=0
  constraints (9):
    c: PointOnObject(g0,g-2)
    c: Coincident(g0,g-1)
    c: Coincident(g1,g0)
    c: Coincident(g2,g1)
    c: DistanceX(g1,g0) = 10.5
    c: DistanceY(g0,g0) = 5
    c: DistanceY(g1,g0) = 15
    c: DistanceX(g1,g2) = -5
    c: DistanceY(g1,g2) = 10
FEATURE [Sketcher::SketchObject] Sketch049
  FullyConstrained = true
  Placement = pos=(0,0,0) rot=(1,0,0;1.5708rad)
  expr: Constraints[10] = <<base_sketch>>.Constraints.face_width / 2 + 30 mm
  expr: Constraints[7] = <<faces_bridge>>.Constraints.offset
  sketch-geometry (6):
    g0: LineSegment StartX=-325.502 StartY=0 StartZ=0 EndX=193.217 EndY=0 EndZ=0
    g1: LineSegment StartX=193.217 StartY=0 StartZ=0 EndX=193.217 EndY=36 EndZ=0
    g2: LineSegment StartX=193.217 StartY=36 StartZ=0 EndX=-325.502 EndY=36 EndZ=0
    g3: LineSegment StartX=-325.502 StartY=36 StartZ=0 EndX=-325.502 EndY=0 EndZ=0
    g4: GeomPoint X=-326.502 Y=0 Z=0
    g5: GeomPoint X=192.217 Y=0 Z=0
  constraints (17):
    c: Coincident(g1,g0)
    c: Vertical(g1)
    c: Coincident(g2,g1)
    c: Coincident(g3,g2)
    c: Coincident(g3,g0)
    c: Vertical(g3)
    c: PointOnObject(g4,g0)
    c: DistanceX(g4) = -326.502
    c: PointOnObject(g5,g0)
    c: Distance(g5,g4) = 518.719  'sink_length'
    c: DistanceX(g5) = 192.217
    c: Distance(g5,g1) = 1
    c: Distance(g4,g3) = 1
    c: PointOnObject(g0,g-1)
    c: Horizontal(g2)
    c: DistanceY(g1) = 36
    c: PointOnObject(g0,g-1)
FEATURE [PartDesign::SubShapeBinder] Binder016
  BindCopyOnChange = 0
  BindMode = 0
  ClaimChildren = true
  Context = -> Body011 [Binder016.]
  Fuse = false
  MakeFace = true
  OffsetFill = false
  OffsetIntersection = false
  OffsetJoinType = 0
  OffsetOpenResult = false
  PartialLoad = false
  Placement = pos=(0,0,0) rot=(1,0,0;1.5708rad)
  Relative = false
  Support = -> [Sketch049]
  _Version = 2
FEATURE [Part::FeaturePython] BaseBend006  # WARN: FeaturePython — macro-defined, semantics opaque (R4)
  BendSide = 0
  BendSketch = -> Sketch048
  MidPlane = false
  Reverse = false
  length = 518.719
  radius = 2
  thickness = 1
  expr: length = Sketch049.Constraints.sink_length
FEATURE [Part::FeaturePython] Placment004  # WARN: FeaturePython — macro-defined, semantics opaque (R4)
  AttacherType = Attacher::AttachEngine3D
  AttachmentOffset = pos=(0,-1.5,0) rot=(0,0,1;0rad)
  ExposePlacement = true
  MapMode = 7
  MarkerShape = 1
  MarkerSize = 20
  NumElements = 1
  Placement = pos=(192.217,0,-1.5) rot=(0.57735,-0.57735,-0.57735;2.0944rad)
  Support = -> [Sketch049]
  Type = lattice2AttachablePlacement.AttachablePlacement
  isLattice = 1
FEATURE [Part::FeaturePython] Populate016  label="Populate Placment004 with BaseBend006"  # WARN: FeaturePython — macro-defined, semantics opaque (R4)
  Copying = 0
  ExposePlacement = false
  MarkerShape = 1
  MarkerSize = 0
  NumElements = 0
  Object = -> BaseBend006
  OutputCompounding = 2
  PlacementsTo = -> Placment004
  Referencing = 0
  Type = lattice2PopulateCopies.LatticePopulateCopies
  isLattice = 0
FEATURE [PartDesign::Pad] Pad014
  Direction = (0,-1,2e-16)
  Length = 1
  Length2 = 10
  Placement = pos=(0,0,0) rot=(1,0,0;1.5708rad)
  Profile = -> Binder016
  Reversed = true
  Type = 0
FEATURE [Part::Compound] Compound015  label="sink2_fuse1"
  Links = -> [Populate016]
FEATURE [Sketcher::SketchObject] Sketch051  label="drain_tube"
  FullyConstrained = true
  MapMode = 2
  Placement = pos=(-313.37,0,0) rot=(0,0,1;0rad)
  sketch-geometry (1):
    g0: Circle CenterX=0 CenterY=37.5 CenterZ=0 NormalX=0 NormalY=0 NormalZ=1 AngleXU=0 Radius=25
  constraints (3):
    c: PointOnObject(g0,g-2)
    c: Diameter(g0) = 50
    c: DistanceY(g0) = 37.5
FEATURE [Sketcher::SketchObject] Sketch050  label="drain_holder_sketch"
  ExternalGeometry = -> [Part__Mirroring,Sketch051]
  FullyConstrained = true
  Placement = pos=(-326.502,0,0) rot=(0,0,1;0rad)
  expr: .Placement.Base.x = <<faces_bridge>>.Constraints.offset
  sketch-geometry (3):
    g0: LineSegment StartX=-94.606 StartY=76.2 StartZ=0 EndX=94.606 EndY=76.2 EndZ=0
    g1: LineSegment StartX=94.606 StartY=76.2 StartZ=0 EndX=109.855 EndY=63.2588 EndZ=0
    g2: LineSegment StartX=-109.855 StartY=63.2588 StartZ=0 EndX=-94.606 EndY=76.2 EndZ=0
  constraints (10):
    c: Coincident(g1,g0)
    c: Distance(g0,g-3) = 3
    c: Parallel(g1,g-3)
    c: Coincident(g2,g0)
    c: Distance(g1) = 20
    c: Symmetric(g2,g1,g-2)
    c: Symmetric(g0,g0,g-2)
    c: Distance(g-4,g0) = 13.7
    c: Angle(g0,g1) = 2.43787
    c: DistanceY(g0) = 76.2  'offset'
FEATURE [PartDesign::SubShapeBinder] Binder017
  BindCopyOnChange = 0
  BindMode = 0
  ClaimChildren = true
  Context = -> Body012 [Binder017.]
  Fuse = false
  MakeFace = true
  OffsetFill = false
  OffsetIntersection = false
  OffsetJoinType = 0
  OffsetOpenResult = false
  PartialLoad = false
  Relative = false
  Support = -> [Sketch050]
  _Version = 2
FEATURE [PartDesign::FeaturePython] BaseBend007  # WARN: FeaturePython — macro-defined, semantics opaque (R4)
  BendSide = 0
  BendSketch = -> Binder017
  MidPlane = false
  Reverse = false
  length = 70
  radius = 0.1
  thickness = 0.3
FEATURE [Part::FeaturePython] Placment005  # WARN: FeaturePython — macro-defined, semantics opaque (R4)
  AttacherType = Attacher::AttachEngine3D
  AttachmentOffset = pos=(3,0,0) rot=(0,-1,0;1.5708rad)
  ExposePlacement = true
  MapMode = 45
  MarkerShape = 1
  MarkerSize = 50
  NumElements = 1
  Placement = pos=(-430.674,72.0167,0) rot=(0.887503,0.325836,0.325836;1.68986rad)
  Support = -> [Sketch050]
  Type = lattice2AttachablePlacement.AttachablePlacement
  isLattice = 1
FEATURE [Part::FeaturePython] Mirror002  label="Mirror002 of Placment005"  # WARN: FeaturePython — macro-defined, semantics opaque (R4)
  ExposePlacement = false
  FlipX = true
  FlipY = false
  FlipZ = false
  MarkerShape = 1
  MarkerSize = 10
  NumElements = 1
  Object = -> Placment005
  ObjectTraversal = 0
  PivotPlacement = pos=(-326.502,0,0) rot=(0,0,1;0rad)
  Type = lattice2Mirror.LatticeMirror
  isLattice = 1
  expr: .PivotPlacement.Base.x = <<faces_bridge>>.Constraints.offset
FEATURE [Part::FeaturePython] Join002  # WARN: FeaturePython — macro-defined, semantics opaque (R4)
  ExposePlacement = false
  Interleave = false
  Links = -> [Placment005,Mirror002]
  MarkerShape = 1
  MarkerSize = 0
  NumElements = 2
  Placement = pos=(326.502,0,0) rot=(0,0,1;0rad)
  Type = lattice2JoinArrays.JoinArrays
  isLattice = 1
  expr: .Placement.Base.x = -<<faces_bridge>>.Constraints.offset
FEATURE [Part::FeaturePython] LinearArray005  # WARN: FeaturePython — macro-defined, semantics opaque (R4)
  Alignment = 0
  CellStart = A1
  Count = 2
  Dir = (0,0,1)
  DirIsDriven = true
  DistributionLaw = 0
  DrivenProperty = 1
  EndInclusive = true
  ExposePlacement = false
  GeneratorMode = 0
  MarkerShape = 1
  MarkerSize = 0
  NumElements = 2
  OrientMode = 0
  Point = (0,0,0)
  PointIsDriven = true
  Reverse = false
  SpanEnd = 60
  SpanStart = 10
  Step = 50
  Type = lattice2LinearArray.LinearArray
  VSGVersion = 1
  Values = 10.0 | 60.0
  ValuesSource = 2
  isLattice = 1
FEATURE [Part::FeaturePython] Populate017  label="Populate LinearArray005 with Join002"  # WARN: FeaturePython — macro-defined, semantics opaque (R4)
  Copying = 0
  ExposePlacement = false
  MarkerShape = 1
  MarkerSize = 0
  NumElements = 4
  Object = -> Join002
  OutputCompounding = 0
  PlacementsTo = -> LinearArray005
  Referencing = 0
  Type = lattice2PopulateCopies.LatticePopulateCopies
  isLattice = 1
FEATURE [Part::FeaturePython] Populate018  label="Populate Populate LinearArray005 with Join002 with hole_3.4_mm"  # WARN: FeaturePython — macro-defined, semantics opaque (R4)
  Copying = 0
  ExposePlacement = false
  MarkerShape = 1
  MarkerSize = 0
  NumElements = 0
  Object = -> Cylinder
  OutputCompounding = 1
  PlacementsTo = -> Populate017
  Referencing = 0
  Type = lattice2PopulateCopies.LatticePopulateCopies
  isLattice = 0
FEATURE [Sketcher::SketchObject] Sketch053  label="face_cut"
  ExternalGeometry = -> [Sketch]
  FullyConstrained = true
  sketch-geometry (6):
    g0: LineSegment StartX=-221.133 StartY=71 StartZ=0 EndX=221.133 EndY=71 EndZ=0
    g1: LineSegment StartX=221.133 StartY=71 StartZ=0 EndX=223.074 EndY=68.7127 EndZ=0
    g2: LineSegment StartX=223.074 StartY=68.7127 StartZ=0 EndX=223.074 EndY=0 EndZ=0
    g3: LineSegment StartX=223.074 StartY=0 StartZ=0 EndX=-223.074 EndY=0 EndZ=0
    g4: LineSegment StartX=-221.133 StartY=71 StartZ=0 EndX=-223.074 EndY=68.7127 EndZ=0
    g5: LineSegment StartX=-223.074 StartY=68.7127 StartZ=0 EndX=-223.074 EndY=0 EndZ=0
  constraints (16):
    c: Coincident(g0,g1)
    c: Coincident(g1,g2)
    c: PointOnObject(g2,g-1)
    c: Vertical(g2)
    c: Coincident(g2,g3)
    c: Perpendicular(g-3,g1)
    c: Distance(g1) = 3
    c: PointOnObject(g0,g-3)
    c: DistanceY(g-3,g0) = 50
    c: Coincident(g0,g4)
    c: Coincident(g4,g5)
    c: PointOnObject(g5,g-1)
    c: Vertical(g5)
    c: Coincident(g5,g3)
    c: Symmetric(g0,g0,g-2)
    c: Symmetric(g4,g1,g-2)
FEATURE [Part::Extrusion] Extrude010
  Base = -> Sketch053
  Dir = (0,0,1)
  DirMode = 2
  FaceMakerClass = Part::FaceMakerBullseye
  LengthFwd = 115
  LengthRev = 0
  Placement = pos=(0,0,-115) rot=(0,0,1;0rad)
  Solid = true
  Symmetric = false
  expr: .Placement.Base.z = -<<Properties>>.bottom_extend
  expr: LengthFwd = -.Placement.Base.z
FEATURE [Part::FeaturePython] Mirror003  label="Mirror003 of Extrude010"  # WARN: FeaturePython — macro-defined, semantics opaque (R4)
  ExposePlacement = false
  FlipX = true
  FlipY = false
  FlipZ = false
  MarkerShape = 1
  MarkerSize = 0
  NumElements = 0
  Object = -> Extrude010
  ObjectTraversal = 0
  PivotPlacement = pos=(-326.502,0,0) rot=(0,0,1;0rad)
  Type = lattice2Mirror.LatticeMirror
  isLattice = 0
  expr: .PivotPlacement.Base.x = <<faces_bridge>>.Constraints.offset
FEATURE [Part::Compound] Compound016
  Links = -> [Mirror003,Extrude010]
FEATURE [PartDesign::SubShapeBinder] Binder018
  BindCopyOnChange = 0
  BindMode = 0
  ClaimChildren = false
  Context = -> Body [Binder018.]
  Fuse = false
  MakeFace = true
  OffsetFill = false
  OffsetIntersection = false
  OffsetJoinType = 0
  OffsetOpenResult = false
  PartialLoad = false
  Relative = true
  Support = -> [Sketch]
  _Version = 2
  expr: Support = <<base_sketch>>._self
FEATURE [PartDesign::SubShapeBinder] Binder019
  BindCopyOnChange = 0
  BindMode = 0
  ClaimChildren = false
  Context = -> Body [Binder019.]
  Fuse = false
  MakeFace = true
  OffsetFill = false
  OffsetIntersection = false
  OffsetJoinType = 0
  OffsetOpenResult = false
  PartialLoad = false
  Relative = true
  Support = -> [Sketch053]
  _Version = 2
  expr: Support = <<face_cut>>._self
FEATURE [Sketcher::SketchObject] Sketch054
  AttachmentOffset = pos=(0,0,0) rot=(0,-1,0;1.5708rad)
  ExternalGeometry = -> [Binder019]
  FullyConstrained = true
  MapMode = 7
  Placement = pos=(162.217,21,0) rot=(0.251276,-0.68442,-0.68442;2.64923rad)
  Support = -> [Binder018]
  expr: Constraints[8] = 180 deg - 6 deg
  sketch-geometry (7):
    g0: ArcOfCircle CenterX=-0.3 CenterY=0 CenterZ=0 NormalX=0 NormalY=0 NormalZ=1 AngleXU=0 Radius=15 StartAngle=1.5708 EndAngle=2.78257
    g1: ArcOfCircle CenterX=-19.0248 CenterY=7.02713 CenterZ=0 NormalX=0 NormalY=0 NormalZ=1 AngleXU=0 Radius=5 StartAngle=4.60767 EndAngle=5.92417
    g2: LineSegment StartX=-19.5475 StartY=2.05452 StartZ=0 EndX=-77.2728 EndY=8.12169 EndZ=0
    g3: LineSegment StartX=-77.2728 StartY=8.12169 StartZ=0 EndX=-77.2728 EndY=0 EndZ=0
    g4: LineSegment StartX=-77.2728 StartY=0 StartZ=0 EndX=0.17 EndY=0 EndZ=0
    g5: LineSegment StartX=0.17 StartY=15 StartZ=0 EndX=-0.3 EndY=15 EndZ=0
    g6: LineSegment StartX=0.17 StartY=0 StartZ=0 EndX=0.17 EndY=15 EndZ=0
  constraints (19):
    c: PointOnObject(g0,g-1)
    c: Tangent(g1,g2) = 1.5708
    c: Coincident(g2,g3)
    c: Vertical(g3)
    c: Coincident(g3,g4)
    c: Horizontal(g5)
    c: Tangent(g5,g0) = -1.5708
    c: Tangent(g1,g0) = 1.5708
    c: Angle(g2) = 3.03687
    c: Radius(g0) = 15
    c: Radius(g1) = 5
    c: Coincident(g3,g-3)
    c: DistanceX(g-2,g0) = -0.3
    c: PointOnObject(g4,g-1)
    c: Coincident(g6,g4)
    c: Coincident(g6,g5)
    c: Vertical(g6)
    c: DistanceX(g4) = 0.17
    c: PointOnObject(g-1,g2)
FEATURE [Sketcher::SketchObject] Sketch055
  AttachmentOffset = pos=(0,0,0) rot=(0,-1,0;1.5708rad)
  FullyConstrained = true
  MapMode = 7
  Placement = pos=(162.217,21,0) rot=(0,-0.707107,-0.707107;3.14159rad)
  Support = -> [Binder018]
  sketch-geometry (5):
    g0: LineSegment StartX=0.3 StartY=15 StartZ=0 EndX=-0.17 EndY=15 EndZ=0
    g1: LineSegment StartX=-0.17 StartY=0 StartZ=0 EndX=19.6649 EndY=0 EndZ=0
    g2: ArcOfCircle CenterX=0.3 CenterY=0 CenterZ=0 NormalX=0 NormalY=0 NormalZ=1 AngleXU=0 Radius=15 StartAngle=0.25268 EndAngle=1.5708
    g3: ArcOfCircle CenterX=19.6649 CenterY=5 CenterZ=0 NormalX=0 NormalY=0 NormalZ=1 AngleXU=0 Radius=5 StartAngle=3.39427 EndAngle=4.71239
    g4: LineSegment StartX=-0.17 StartY=15 StartZ=0 EndX=-0.17 EndY=0 EndZ=0
  constraints (14):
    c: PointOnObject(g1,g-1)
    c: Tangent(g2,g0) = -1.5708
    c: Horizontal(g0)
    c: Radius(g2) = 15
    c: Tangent(g3,g2) = 1.5708
    c: DistanceX(g0) = 0.3
    c: PointOnObject(g2,g1)
    c: Radius(g3) = 5
    c: Tangent(g3,g1) = -1.5708
    c: PointOnObject(g1,g-1)
    c: DistanceX(g1) = -0.17
    c: Coincident(g4,g0)
    c: Coincident(g4,g1)
    c: Vertical(g4)
FEATURE [PartDesign::Pocket] Pocket010
  BaseFeature = -> Pad
  Direction = (0.647059,-0.76244,-1e-16)
  Length = 5
  Length2 = 5
  Midplane = true
  Profile = -> Sketch054
  ReferenceAxis = -> Sketch054 [N_Axis]
  Refine = true
  Type = 0
FEATURE [PartDesign::Pocket] Pocket011
  BaseFeature = -> Pocket010
  Direction = (2e-16,-1,0)
  Length = 5
  Length2 = 5
  Midplane = true
  Profile = -> Sketch055
  ReferenceAxis = -> Sketch055 [N_Axis]
  Refine = true
  Type = 0
FEATURE [Sketcher::SketchObject] Sketch056
  ExternalGeometry = -> [Binder018]
  FullyConstrained = true
  MapMode = 1
  Placement = pos=(162.217,21,0) rot=(0,0,1;0rad)
  Support = -> [Binder018]
  sketch-geometry (4):
    g0: ArcOfCircle CenterX=-0.0367138 CenterY=0.1 CenterZ=0 NormalX=0 NormalY=0 NormalZ=1 AngleXU=0 Radius=0.1 StartAngle=4.71239 EndAngle=5.41611
    g1: LineSegment StartX=-0.0367138 StartY=0.1 StartZ=0 EndX=-0.0367138 EndY=-3.0958 EndZ=0
    g2: LineSegment StartX=-0.0367138 StartY=-3.0958 StartZ=0 EndX=2.03115 EndY=-2.3366 EndZ=0
    g3: LineSegment StartX=2.03115 StartY=-2.3366 StartZ=0 EndX=-0.0367138 EndY=0.1 EndZ=0
  constraints (11):
    c: Radius(g0) = 0.1
    c: Tangent(g0,g-3) = -1.5708
    c: Tangent(g0,g-1) = -1.5708
    c: Coincident(g1,g0)
    c: Vertical(g1)
    c: Coincident(g1,g2)
    c: Coincident(g2,g3)
    c: Coincident(g3,g1)
    c: PointOnObject(g0,g3)
    c: Equal(g1,g3)
    c: Distance(g1,g2) = 3
FEATURE [PartDesign::Plane] DatumPlane003
  AttachmentOffset = pos=(0,0,-326.502) rot=(0,0,1;0rad)
  Length = 258.015
  MapMode = 5
  Placement = pos=(-326.502,0,0) rot=(0.57735,0.57735,0.57735;2.0944rad)
  ResizeMode = 0
  Support = -> [YZ_Plane]
  Width = 949.356
  expr: .AttachmentOffset.Base.z = <<faces_bridge>>.Constraints.offset
FEATURE [PartDesign::Mirrored] Mirrored007
  MirrorPlane = -> YZ_Plane
FEATURE [PartDesign::Mirrored] Mirrored008
  MirrorPlane = -> DatumPlane003
FEATURE [PartDesign::MultiTransform] MultiTransform001
  BaseFeature = -> Pocket011
  Originals = -> [Pocket010,Pocket011]
  Transformations = -> [Mirrored007,Mirrored008]
FEATURE [Part::FeaturePython] LinearArray006  label="screw_holes_placements"  # WARN: FeaturePython — macro-defined, semantics opaque (R4)
  Alignment = 0
  CellStart = A1
  Count = 3
  Dir = (1,0,0)
  DirIsDriven = true
  DistributionLaw = 0
  DrivenProperty = 1
  EndInclusive = true
  ExposePlacement = false
  GeneratorMode = 1
  MarkerShape = 1
  MarkerSize = 10
  NumElements = 3
  OrientMode = 1
  Placement = pos=(-976.007,0,0) rot=(1,0,0;1.5708rad)
  Point = (0,0,0)
  PointIsDriven = true
  Reverse = false
  SpanEnd = 500
  SpanStart = 0
  Step = 649.505
  Type = lattice2LinearArray.LinearArray
  VSGVersion = 1
  Values = 0.0 | 649.5048374651765 | 1299.009674930353
  ValuesSource = 2
  isLattice = 1
  expr: .Placement.Base.x = <<faces_bridge>>.Constraints.offset - Step * 1 mm
  expr: Step = <<wall>>.Constraints.distance - <<faces_bridge>>.Constraints.offset - 6 mm
FEATURE [Part::FeaturePython] LinearArray007  # WARN: FeaturePython — macro-defined, semantics opaque (R4)
  Alignment = 0
  CellStart = A1
  Count = 2
  Dir = (0,0,1)
  DirIsDriven = true
  DistributionLaw = 0
  DrivenProperty = 1
  EndInclusive = true
  ExposePlacement = false
  GeneratorMode = 0
  MarkerShape = 1
  MarkerSize = 0
  NumElements = 2
  OrientMode = 0
  Point = (0,0,0)
  PointIsDriven = true
  Reverse = false
  SpanEnd = 80
  SpanStart = 10
  Step = 70
  Type = lattice2LinearArray.LinearArray
  VSGVersion = 1
  Values = 10.0 | 80.0
  ValuesSource = 2
  isLattice = 1
FEATURE [Part::FeaturePython] Populate019  label="Populate LinearArray007 with screw_holes_placements"  # WARN: FeaturePython — macro-defined, semantics opaque (R4)
  Copying = 0
  ExposePlacement = false
  MarkerShape = 1
  MarkerSize = 0
  NumElements = 6
  Object = -> LinearArray006
  OutputCompounding = 0
  Placement = pos=(0,3,0) rot=(0,0,1;0rad)
  PlacementsTo = -> LinearArray007
  Referencing = 0
  Type = lattice2PopulateCopies.LatticePopulateCopies
  isLattice = 1
FEATURE [Part::FeaturePython] Populate020  label="Populate Populate LinearArray007 with screw_holes_placements with hole_3.4_mm"  # WARN: FeaturePython — macro-defined, semantics opaque (R4)
  Copying = 0
  ExposePlacement = false
  MarkerShape = 1
  MarkerSize = 0
  NumElements = 0
  Object = -> Cylinder
  OutputCompounding = 1
  PlacementsTo = -> Populate019
  Referencing = 0
  Type = lattice2PopulateCopies.LatticePopulateCopies
  isLattice = 0
FEATURE [Part::FeaturePython] Placment006  label="front_shield_placement"  # WARN: FeaturePython — macro-defined, semantics opaque (R4)
  AttacherType = Attacher::AttachEngine3D
  ExposePlacement = true
  MarkerShape = 1
  MarkerSize = 50
  NumElements = 1
  Placement = pos=(0,154.059,-115) rot=(0,0,1;0rad)
  Type = lattice2AttachablePlacement.AttachablePlacement
  isLattice = 1
  expr: .Placement.Base.y = <<base_sketch>>.Constraints.max_y
  expr: .Placement.Base.z = -<<Properties>>.bottom_extend
FEATURE [Part::FeaturePython] Populate021  label="Populate Placment006 with Populate Populate LinearArray007 with screw_holes_placements with hole_3.4_mm"  # WARN: FeaturePython — macro-defined, semantics opaque (R4)
  Copying = 0
  ExposePlacement = false
  MarkerShape = 1
  MarkerSize = 0
  NumElements = 0
  Object = -> Populate020
  OutputCompounding = 2
  PlacementsTo = -> Placment006
  Referencing = 0
  Type = lattice2PopulateCopies.LatticePopulateCopies
  isLattice = 0
FEATURE [Sketcher::SketchObject] Sketch057
  FullyConstrained = true
  expr: Constraints[1] = <<wall>>.Constraints.distance
  expr: Constraints[2] = <<length>>.Length
  sketch-geometry (1):
    g0: LineSegment StartX=-982.007 StartY=3 StartZ=0 EndX=329.002 EndY=3 EndZ=0
  constraints (4):
    c: Horizontal(g0)
    c: DistanceX(g0) = 329.002
    c: DistanceX(g0,g0) = 1311.01
    c: DistanceY(g0) = 3
FEATURE [PartDesign::SubShapeBinder] Binder020
  BindCopyOnChange = 0
  BindMode = 0
  ClaimChildren = true
  Context = -> Body013 [Binder020.]
  Fuse = false
  MakeFace = true
  OffsetFill = false
  OffsetIntersection = false
  OffsetJoinType = 0
  OffsetOpenResult = false
  PartialLoad = false
  Relative = false
  Support = -> [Sketch057]
  _Version = 2
FEATURE [PartDesign::FeaturePython] BaseBend008  # WARN: FeaturePython — macro-defined, semantics opaque (R4)
  BendSide = 0
  BendSketch = -> Binder020
  MidPlane = false
  Reverse = false
  length = 133
  radius = 0
  thickness = 0.3
  expr: length = <<Properties>>.bottom_extend + 18 mm
FEATURE [Part::Compound] Compound017  label="front_shield_cut1"
  Links = -> [Populate020]
FEATURE [PartDesign::Boolean] Boolean009
  BaseFeature = -> BaseBend008
  Group = -> [Compound017]
  Type = 1
FEATURE [PartDesign::Body] Body013  label="front_shield"
  Group = -> [Binder020,BaseBend008,Boolean009]
  Origin = -> Origin016
  Placement = pos=(0,154.059,-115) rot=(0,0,1;0rad)
  Tip = -> Boolean009
  expr: Placement = <<front_shield_placement>>.Placement
FEATURE [Part::FeaturePython] Placment007  label="drain_holder_placement"  # WARN: FeaturePython — macro-defined, semantics opaque (R4)
  AttacherType = Attacher::AttachEngine3D
  ExposePlacement = true
  MarkerShape = 1
  MarkerSize = 50
  NumElements = 1
  Placement = pos=(-326.502,0,-115) rot=(0,0,1;0rad)
  Type = lattice2AttachablePlacement.AttachablePlacement
  isLattice = 1
  expr: .Placement.Base.x = <<faces_bridge>>.Constraints.offset
  expr: .Placement.Base.z = -<<Properties>>.bottom_extend
FEATURE [Part::FeaturePython] Populate022  label="Populate drain_holder_placement with Populate Populate LinearArray005 with Join002 with hole_3.4_mm"  # WARN: FeaturePython — macro-defined, semantics opaque (R4)
  Copying = 0
  ExposePlacement = false
  MarkerShape = 1
  MarkerSize = 0
  NumElements = 0
  Object = -> Populate018
  OutputCompounding = 2
  PlacementsTo = -> Placment007
  Referencing = 0
  Type = lattice2PopulateCopies.LatticePopulateCopies
  isLattice = 0
FEATURE [Part::Cylinder] Cylinder001  label="drain_fix_hole"
  Angle = 360
  AttacherType = Attacher::AttachEngine3D
  FirstAngle = 0
  Height = 10
  Radius = 2
  SecondAngle = 0
FEATURE [Part::FeaturePython] LinearArray008  label="drain_fix_hole_placements"  # WARN: FeaturePython — macro-defined, semantics opaque (R4)
  Alignment = 0
  CellStart = A1
  Count = 2
  Dir = (1,0,0)
  DirIsDriven = true
  DistributionLaw = 0
  DrivenProperty = 1
  EndInclusive = true
  ExposePlacement = false
  GeneratorMode = 0
  MarkerShape = 1
  MarkerSize = 0
  NumElements = 2
  OrientMode = 1
  Placement = pos=(0,76.2,0) rot=(0.57735,-0.57735,0.57735;2.0944rad)
  Point = (0,0,0)
  PointIsDriven = true
  Reverse = false
  SpanEnd = 45
  SpanStart = 7.5
  Step = 37.5
  Type = lattice2LinearArray.LinearArray
  VSGVersion = 1
  Values = 7.5 | 45.0
  ValuesSource = 2
  isLattice = 1
  expr: .Placement.Base.y = <<drain_holder_sketch>>.Constraints.offset
  expr: SpanEnd = <<BaseBend007>>.length - (15 mm / 2 + 17.5 mm)
  expr: SpanStart = 15 mm / 2
FEATURE [Part::FeaturePython] Populate023  label="Populate drain_fix_hole_placements with drain_fix_hole"  # WARN: FeaturePython — macro-defined, semantics opaque (R4)
  Copying = 0
  ExposePlacement = false
  MarkerShape = 1
  MarkerSize = 0
  NumElements = 0
  Object = -> Cylinder001
  OutputCompounding = 1
  PlacementsTo = -> LinearArray008
  Referencing = 0
  Type = lattice2PopulateCopies.LatticePopulateCopies
  isLattice = 0
FEATURE [Part::Compound] Compound018  label="drain_holder_cut1"
  Links = -> [Populate018,Populate023]
FEATURE [PartDesign::Boolean] Boolean008
  BaseFeature = -> BaseBend007
  Group = -> [Compound018]
  Type = 1
FEATURE [PartDesign::Body] Body012  label="drain_holder"
  Group = -> [Binder017,BaseBend007,Boolean008]
  Origin = -> Origin015
  Placement = pos=(-313,0,-115) rot=(0,0,1;0rad)
  Tip = -> Boolean008
FEATURE [Part::FeaturePython] LinearArray009  label="bar_placements"  # WARN: FeaturePython — macro-defined, semantics opaque (R4)
  Alignment = 0
  CellStart = A1
  Count = 2
  Dir = (-1,0,0)
  DirIsDriven = true
  DistributionLaw = 0
  DrivenProperty = 1
  EndInclusive = true
  ExposePlacement = false
  GeneratorMode = 0
  MarkerShape = 1
  MarkerSize = 0
  NumElements = 2
  OrientMode = 0
  Placement = pos=(326.002,18,142.5) rot=(0.707107,0,-0.707107;3.14159rad)
  Point = (0,0,0)
  PointIsDriven = true
  Reverse = false
  SpanEnd = 559.8
  SpanStart = 0
  Step = 559.8
  Type = lattice2LinearArray.LinearArray
  VSGVersion = 1
  Values = 0.0 | 559.8
  ValuesSource = 2
  isLattice = 1
  expr: .Placement.Base.x = <<wall>>.Constraints.distance - 3 mm
  expr: .Placement.Base.y = <<base_sketch>>.Constraints.offset - 3 mm
FEATURE [Part::FeaturePython] Placment008  # WARN: FeaturePython — macro-defined, semantics opaque (R4)
  AttacherType = Attacher::AttachEngine3D
  AttachmentOffset = pos=(0,0,0) rot=(0,0,1;3.14159rad)
  ExposePlacement = true
  MarkerShape = 1
  MarkerSize = 20
  NumElements = 1
  Placement = pos=(0,0,0) rot=(0,0,1;3.14159rad)
  Type = lattice2AttachablePlacement.AttachablePlacement
  isLattice = 1
FEATURE [Part::FeaturePython] Mirror004  label="Mirror004 of Placment008"  # WARN: FeaturePython — macro-defined, semantics opaque (R4)
  ExposePlacement = false
  FlipX = true
  FlipY = false
  FlipZ = true
  MarkerShape = 1
  MarkerSize = 20
  NumElements = 1
  Object = -> Placment008
  ObjectTraversal = 0
  PivotPlacement = pos=(0,0,652.505) rot=(0,0,1;0rad)
  Type = lattice2Mirror.LatticeMirror
  isLattice = 1
  expr: .PivotPlacement.Base.z = (<<length>>.Length - 6 mm) / 2
FEATURE [Part::FeaturePython] Join003  # WARN: FeaturePython — macro-defined, semantics opaque (R4)
  ExposePlacement = false
  Interleave = false
  Links = -> [Mirror004,Placment008]
  MarkerShape = 1
  MarkerSize = 20
  NumElements = 2
  Type = lattice2JoinArrays.JoinArrays
  isLattice = 1
FEATURE [Part::FeaturePython] Populate024  label="Populate Join003 with Extrude009"  # WARN: FeaturePython — macro-defined, semantics opaque (R4)
  Copying = 0
  ExposePlacement = false
  MarkerShape = 1
  MarkerSize = 0
  NumElements = 0
  Object = -> Extrude009
  OutputCompounding = 1
  PlacementsTo = -> Join003
  Referencing = 0
  Type = lattice2PopulateCopies.LatticePopulateCopies
  isLattice = 0
FEATURE [Part::Compound] Compound019
  Links = -> [Populate024,Populate015]
FEATURE [Part::FeaturePython] Populate025  label="Populate bar_placements with Compound019"  # WARN: FeaturePython — macro-defined, semantics opaque (R4)
  Copying = 0
  ExposePlacement = false
  MarkerShape = 1
  MarkerSize = 0
  NumElements = 0
  Object = -> Compound019
  OutputCompounding = 1
  PlacementsTo = -> LinearArray009
  Referencing = 0
  Type = lattice2PopulateCopies.LatticePopulateCopies
  isLattice = 0
FEATURE [Part::Compound] Compound  label="face_cut1"
  Links = -> [Populate001,Extrude001,Populate005,Populate011,Compound016,Populate021,Populate022,Populate025]
FEATURE [PartDesign::Boolean] Boolean
  BaseFeature = -> MultiTransform001
  Group = -> [Compound]
  Refine = true
  Type = 1
FEATURE [PartDesign::Body] Body  label="face_material_0.30ansi"
  Group = -> [Binder,BaseBend,Extend,Bend,Binder001,Pad,Binder018,Sketch054,Binder019,Sketch055,Pocket010,Pocket011,Sketch056,DatumPlane003,MultiTransform001,Mirrored007,Mirrored008,Boolean]
  Origin = -> Origin
  Tip = -> Boolean
FEATURE [PartDesign::SubShapeBinder] Binder021
  BindCopyOnChange = 0
  BindMode = 0
  ClaimChildren = false
  Context = -> Part [Part001.Body014.Binder021.]
  Fuse = false
  MakeFace = true
  OffsetFill = false
  OffsetIntersection = false
  OffsetJoinType = 0
  OffsetOpenResult = false
  PartialLoad = false
  Relative = false
  Support = -> [Sketch021]
  _Version = 2
  expr: Support = <<cap_cut>>._self
FEATURE [Sketcher::SketchObject] Sketch058  label="cap_holes_sketch"
  ExternalGeometry = -> [Sketch021]
  FullyConstrained = true
  expr: Constraints[17] = <<Properties>>.rivet_d
  sketch-geometry (10):
    g0: Circle CenterX=265.532 CenterY=19.1617 CenterZ=0 NormalX=0 NormalY=0 NormalZ=1 AngleXU=0 Radius=1.7
    g1: Circle CenterX=245.599 CenterY=20.8045 CenterZ=0 NormalX=0 NormalY=0 NormalZ=1 AngleXU=0 Radius=1.7
    g2: Circle CenterX=320.081 CenterY=150.856 CenterZ=0 NormalX=0 NormalY=0 NormalZ=1 AngleXU=0 Radius=1.7
    g3: Circle CenterX=304.826 CenterY=163.789 CenterZ=0 NormalX=0 NormalY=0 NormalZ=1 AngleXU=0 Radius=1.7
    g4: LineSegment StartX=245.599 StartY=20.8045 StartZ=0 EndX=255.566 EndY=19.9831 EndZ=0
    g5: LineSegment StartX=255.566 StartY=19.9831 StartZ=0 EndX=265.532 EndY=19.1617 EndZ=0
    g6: LineSegment StartX=320.081 StartY=150.856 StartZ=0 EndX=312.454 EndY=157.323 EndZ=0
    g7: LineSegment StartX=312.454 StartY=157.323 StartZ=0 EndX=304.826 EndY=163.789 EndZ=0
    g8: LineSegment StartX=254.744 StartY=2.98e-14 StartZ=0 EndX=255.566 EndY=19.9831 EndZ=0
    g9: LineSegment StartX=312.454 StartY=157.323 StartZ=0 EndX=326.002 EndY=172.034 EndZ=0
  constraints (26):
    c: Coincident(g4,g1)
    c: PointOnObject(g4,g-3)
    c: Coincident(g4,g5)
    c: Coincident(g5,g0)
    c: PointOnObject(g6,g-3)
    c: Coincident(g6,g7)
    c: Coincident(g7,g3)
    c: Equal(g5,g4)
    c: Equal(g4,g6)
    c: Equal(g6,g7)
    c: Perpendicular(g-3,g5)
    c: Perpendicular(g-3,g6)
    c: Parallel(g6,g7)
    c: Parallel(g5,g4)
    c: Equal(g1,g0)
    c: Equal(g1,g2)
    c: Equal(g1,g3)
    c: Diameter(g1) = 3.4
    c: Distance(g0,g1) = 20
    c: Coincident(g8,g-3)
    c: Coincident(g8,g4)
    c: Coincident(g9,g6)
    c: Coincident(g9,g-3)
    c: Equal(g9,g8)
    c: Distance(g8) = 20
    c: Coincident(g2,g6)
FEATURE [Part::Extrusion] Extrude011  label="cap_holes"
  Base = -> Sketch058
  Dir = (0,0,1)
  DirMode = 2
  FaceMakerClass = Part::FaceMakerBullseye
  LengthFwd = 10
  LengthRev = 0
  Solid = true
  Symmetric = true
FEATURE [Part::Mirroring] Part__Mirroring012  label="cap_holes (Mirror #13)"
  Base = (-326.502,0,0)
  Normal = (1,0,0)
  Source = -> Extrude011
  expr: .Base.x = <<faces_bridge>>.Constraints.offset
FEATURE [Part::Compound] Compound020
  Links = -> [Extrude011,Part__Mirroring012]
  Placement = pos=(0,0,38) rot=(0,0,1;0rad)
FEATURE [Part::Compound] Compound022  label="cap_inner_cut1"
  Links = -> [Extrude011]
FEATURE [Part::Compound] Compound021  label="cap_outer_cut1"
  Links = -> [Compound020]
FEATURE [PartDesign::SubShapeBinder] Binder022
  BindCopyOnChange = 0
  BindMode = 0
  ClaimChildren = false
  Context = -> Part [Part001.Body014.Binder022.]
  Fuse = false
  MakeFace = true
  OffsetFill = false
  OffsetIntersection = false
  OffsetJoinType = 0
  OffsetOpenResult = false
  PartialLoad = false
  Relative = true
  Support = -> [Sketch058]
  _Version = 2
  expr: Support = <<cap_holes_sketch>>._self
FEATURE [Sketcher::SketchObject] Sketch059
  ExternalGeometry = -> [Binder022,Binder021]
  FullyConstrained = false
  MapMode = 5
  Support = -> [XY_Plane017]
  sketch-geometry (11):
    g0: GeomPoint X=127.415 Y=-176.142 Z=0
    g1: GeomPoint X=236.279 Y=54.7236 Z=0
    g2: GeomPoint X=325.491 Y=0 Z=0
    g3: ArcOfCircle CenterX=245.599 CenterY=20.8045 CenterZ=0 NormalX=0 NormalY=0 NormalZ=1 AngleXU=0 Radius=80.403 StartAngle=0 EndAngle=5.76307
    g4: ArcOfCircle CenterX=320.081 CenterY=150.856 CenterZ=0 NormalX=0 NormalY=0 NormalZ=1 AngleXU=0 Radius=80.403 StartAngle=5.76307 EndAngle=8.72161
    g5: LineSegment StartX=326.002 StartY=172.034 StartZ=0 EndX=326.002 EndY=20.8045 EndZ=0
    g6: ArcOfCircle CenterX=498.036 CenterY=0 CenterZ=0 NormalX=0 NormalY=0 NormalZ=1 AngleXU=0 Radius=313.696 StartAngle=2.43842 EndAngle=3.14032
    g7: LineSegment StartX=389.852 StartY=110.898 StartZ=0 EndX=315.37 EndY=-19.154 EndZ=0
    g8: LineSegment StartX=326.002 StartY=20.8045 StartZ=0 EndX=326.002 EndY=0.4 EndZ=0
    g9: LineSegment StartX=326.002 StartY=0.4 StartZ=0 EndX=184.341 EndY=0.4 EndZ=0
    g10: Circle CenterX=265.532 CenterY=19.1617 CenterZ=0 NormalX=0 NormalY=0 NormalZ=1 AngleXU=0 Radius=80.403
  constraints (20):
    c: PointOnObject(g2,g-1)
    c: Coincident(g3,g-4)
    c: Coincident(g4,g-7)
    c: Coincident(g5,g-6)
    c: Tangent(g5,g3) = 1.5708
    c: Vertical(g5)
    c: Equal(g3,g4)
    c: Coincident(g6,g-6)
    c: Coincident(g6,g4)
    c: Tangent(g7,g3) = 1.5708
    c: Tangent(g7,g4) = 1.5708
    c: Vertical(g8)
    c: Coincident(g9,g8)
    c: Coincident(g10,g-3)
    c: Tangent(g10,g6)
    c: Equal(g10,g3)
    c: Coincident(g9,g6)
    c: Tangent(g8,g3) = 1.5708
    c: Horizontal(g9)
    c: DistanceY(g8) = 0.4
FEATURE [Part::FeaturePython] Placment009  # WARN: FeaturePython — macro-defined, semantics opaque (R4)
  AttacherType = Attacher::AttachEngine3D
  AttachmentOffset = pos=(3,14,-20) rot=(0,-1,0;1.5708rad)
  ExposePlacement = true
  MapMode = 7
  MarkerShape = 1
  MarkerSize = 10
  NumElements = 1
  Placement = pos=(183.813,19.6539,14) rot=(0.251276,-0.68442,-0.68442;2.64923rad)
  Support = -> [Sketch011]
  Type = lattice2AttachablePlacement.AttachablePlacement
  isLattice = 1
FEATURE [Part::FeaturePython] Placment010  # WARN: FeaturePython — macro-defined, semantics opaque (R4)
  AttacherType = Attacher::AttachEngine3D
  AttachmentOffset = pos=(3,14,20) rot=(0,-1,0;1.5708rad)
  ExposePlacement = true
  MapMode = 7
  MarkerShape = 1
  MarkerSize = 10
  NumElements = 1
  Placement = pos=(305.695,123.091,14) rot=(0.251276,-0.68442,-0.68442;2.64923rad)
  Support = -> [Sketch011]
  Type = lattice2AttachablePlacement.AttachablePlacement
  isLattice = 1
  expr: AttachmentOffset = placement(vector(<<Placment009>>.AttachmentOffset.Base.x; <<Placment009>>.AttachmentOffset.Base.y; -<<Placment009>>.AttachmentOffset.Base.z); rotation(<<Placment009>>.AttachmentOffset.Rotation.Axis; <<Placment009>>.AttachmentOffset.Rotation.Angle))
FEATURE [Part::FeaturePython] Join004  label="top_connection_holes_placement"  # WARN: FeaturePython — macro-defined, semantics opaque (R4)
  ExposePlacement = false
  Interleave = false
  Links = -> [Placment009,Placment010]
  MarkerShape = 1
  MarkerSize = 0
  NumElements = 2
  Type = lattice2JoinArrays.JoinArrays
  isLattice = 1
FEATURE [Part::FeaturePython] Populate026  label="Populate top_connection_holes_placement with hole_3.4_mm"  # WARN: FeaturePython — macro-defined, semantics opaque (R4)
  Copying = 0
  ExposePlacement = false
  MarkerShape = 1
  MarkerSize = 0
  NumElements = 0
  Object = -> Cylinder
  OutputCompounding = 1
  PlacementsTo = -> Join004
  Referencing = 0
  Type = lattice2PopulateCopies.LatticePopulateCopies
  isLattice = 0
FEATURE [Part::Compound] Compound023  label="top_supplement_cut1"
  Links = -> [Populate026,Extrude002]
FEATURE [PartDesign::Boolean] Boolean012
  BaseFeature = -> Bend002
  Group = -> [Compound023]
  Type = 1
FEATURE [PartDesign::Body] Body004  label="top_supplement_material_0.30ansi"
  Group = -> [Binder009,Sketch017,BaseBend002,Bend002,Boolean012]
  Origin = -> Origin005
  Tip = -> Boolean012
FEATURE [Sketcher::SketchObject] Sketch060
  ExternalGeometry = -> [Sketch010]
  FullyConstrained = true
  Placement = pos=(0,0,0) rot=(0.57735,0.57735,0.57735;2.0944rad)
  sketch-geometry (6):
    g0: LineSegment StartX=134.059 StartY=0 StartZ=0 EndX=139.059 EndY=0 EndZ=0
    g1: LineSegment StartX=139.059 StartY=0 StartZ=0 EndX=139.059 EndY=10 EndZ=0
    g2: LineSegment StartX=156.316 StartY=12.8025 StartZ=0 EndX=157.184 EndY=17.7265 EndZ=0
    g3: LineSegment StartX=157.184 StartY=17.7265 StartZ=0 EndX=147.336 EndY=19.463 EndZ=0
    g4: LineSegment StartX=141.948 StartY=23.4593 StartZ=0 EndX=146.873 EndY=22.5911 EndZ=0
    g5: LineSegment StartX=146.873 StartY=22.5911 StartZ=0 EndX=148.609 EndY=32.4392 EndZ=0
  constraints (21):
    c: Horizontal(g0)
    c: Coincident(g0,g1)
    c: Coincident(g2,g3)
    c: Coincident(g4,g5)
    c: PointOnObject(g0,g-1)
    c: PointOnObject(g2,g-3)
    c: Perpendicular(g3,g2)
    c: Perpendicular(g1,g0)
    c: Perpendicular(g5,g4)
    c: Parallel(g2,g-3)
    c: Perpendicular(g-3,g4)
    c: Distance(g4,g-3) = 11
    c: Equal(g4,g2)
    c: Equal(g2,g0)
    c: Equal(g1,g3)
    c: Equal(g3,g5)
    c: DistanceX(g0,g0) = 5
    c: DistanceY(g1,g1) = 10
    c: Distance(g-3,g4) = 3
    c: Distance(g2,g-3) = 6
    c: DistanceX(g0,g-3) = 15
FEATURE [Part::FeaturePython] Placment011  # WARN: FeaturePython — macro-defined, semantics opaque (R4)
  AttacherType = Attacher::AttachEngine3D
  ExposePlacement = true
  MapMode = 51
  MarkerShape = 1
  MarkerSize = 5
  NumElements = 1
  Placement = pos=(0,139.059,0) rot=(0,0,1;0rad)
  Support = -> [Sketch060]
  Type = lattice2AttachablePlacement.AttachablePlacement
  isLattice = 1
FEATURE [Part::FeaturePython] PlacementSubsequence001  # WARN: FeaturePython — macro-defined, semantics opaque (R4)
  Base = -> Placment011
  CycleMode = 0
  ExposePlacement = false
  MarkerShape = 1
  MarkerSize = 0
  NumElements = 3
  Type = lattice2AttachablePlacement.AttachedPlacementSubsequence
  isLattice = 1
FEATURE [Part::FeaturePython] LinearArray010  # WARN: FeaturePython — macro-defined, semantics opaque (R4)
  Alignment = 0
  CellStart = A1
  Count = 2
  Dir = (1,0,0)
  DirIsDriven = true
  DistributionLaw = 0
  DrivenProperty = 1
  EndInclusive = true
  ExposePlacement = false
  GeneratorMode = 0
  MarkerShape = 1
  MarkerSize = 0
  NumElements = 2
  OrientMode = 1
  Placement = pos=(-100,0,0) rot=(0,0,1;0rad)
  Point = (0,0,0)
  PointIsDriven = true
  Reverse = false
  SpanEnd = 200
  SpanStart = 0
  Step = 200
  Type = lattice2LinearArray.LinearArray
  VSGVersion = 1
  Values = 0.0 | 200.0
  ValuesSource = 2
  isLattice = 1
  expr: .Placement.Base.x = -SpanEnd / 2
FEATURE [Part::FeaturePython] Populate027  label="Populate LinearArray010 with PlacementSubsequence001"  # WARN: FeaturePython — macro-defined, semantics opaque (R4)
  Copying = 0
  ExposePlacement = false
  MarkerShape = 1
  MarkerSize = 0
  NumElements = 6
  Object = -> PlacementSubsequence001
  OutputCompounding = 0
  PlacementsTo = -> LinearArray010
  Referencing = 0
  Type = lattice2PopulateCopies.LatticePopulateCopies
  isLattice = 1
FEATURE [Part::FeaturePython] Populate028  label="Populate Populate LinearArray010 with PlacementSubsequence001 with hole_3.4_mm"  # WARN: FeaturePython — macro-defined, semantics opaque (R4)
  Copying = 0
  ExposePlacement = false
  MarkerShape = 1
  MarkerSize = 0
  NumElements = 0
  Object = -> Cylinder
  OutputCompounding = 1
  PlacementsTo = -> Populate027
  Referencing = 0
  Type = lattice2PopulateCopies.LatticePopulateCopies
  isLattice = 0
FEATURE [Part::Compound] Compound007  label="top_cut1"
  Links = -> [Extrude002,Populate008,Populate026,Populate028]
FEATURE [PartDesign::Boolean] Boolean001
  BaseFeature = -> Mirrored
  Group = -> [Compound007]
  Type = 1
FEATURE [PartDesign::Body] Body002  label="top_material_0.30ansi"
  Group = -> [BaseBend001,Binder002,Pocket,Bend001,Pocket001,Mirrored,Boolean001,Binder003]
  Origin = -> Origin003
  Tip = -> Boolean001
FEATURE [Part::FeaturePython] Populate029  label="Populate PlacementSubsequence001 with hole_3.4_mm"  # WARN: FeaturePython — macro-defined, semantics opaque (R4)
  Copying = 0
  ExposePlacement = false
  MarkerShape = 1
  MarkerSize = 0
  NumElements = 0
  Object = -> Cylinder
  OutputCompounding = 1
  PlacementsTo = -> PlacementSubsequence001
  Referencing = 0
  Type = lattice2PopulateCopies.LatticePopulateCopies
  isLattice = 0
FEATURE [PartDesign::SubShapeBinder] Binder023
  BindCopyOnChange = 0
  BindMode = 0
  ClaimChildren = true
  Context = -> Body015 [Binder023.]
  Fuse = false
  MakeFace = true
  OffsetFill = false
  OffsetIntersection = false
  OffsetJoinType = 0
  OffsetOpenResult = false
  PartialLoad = false
  Relative = true
  Support = -> [Sketch060]
  _Version = 2
FEATURE [PartDesign::SubShapeBinder] Binder024
  BindCopyOnChange = 0
  BindMode = 0
  ClaimChildren = true
  Context = -> Body015 [Binder024.]
  Fuse = false
  MakeFace = true
  OffsetFill = false
  OffsetIntersection = false
  OffsetJoinType = 0
  OffsetOpenResult = false
  PartialLoad = false
  Relative = true
  Support = -> [Sketch010]
  _Version = 2
  expr: Support = <<top_base_sketch>>._self
FEATURE [Sketcher::SketchObject] Sketch061  label="led_holder_base_sketch"
  ExternalGeometry = -> [Binder024,Binder023]
  FullyConstrained = true
  MapMode = 5
  Placement = pos=(0,0,0) rot=(0.57735,0.57735,0.57735;2.0944rad)
  Support = -> [YZ_Plane018]
  sketch-geometry (16):
    g0: LineSegment StartX=126.541 StartY=3 StartZ=0 EndX=151.541 EndY=3 EndZ=0
    g1: LineSegment StartX=151.541 StartY=3 StartZ=0 EndX=155.272 EndY=24.1563 EndZ=0
    g2: LineSegment StartX=155.272 StartY=24.1563 StartZ=0 EndX=183.226 EndY=19.2272 EndZ=0
    g3: LineSegment StartX=183.226 StartY=19.2272 StartZ=0 EndX=183.226 EndY=24.3043 EndZ=0
    g4: LineSegment StartX=183.226 StartY=24.3043 StartZ=0 EndX=155.155 EndY=29.254 EndZ=0
    g5: LineSegment StartX=150.522 StartY=26.0094 StartZ=0 EndX=147.929 EndY=11.3054 EndZ=0
    g6: LineSegment StartX=143.99 StartY=8 StartZ=0 EndX=126.541 EndY=8 EndZ=0
    g7: LineSegment StartX=126.541 StartY=8 StartZ=0 EndX=126.541 EndY=3 EndZ=0
    g8: ArcOfCircle CenterX=143.99 CenterY=12 CenterZ=0 NormalX=0 NormalY=0 NormalZ=1 AngleXU=0 Radius=4 StartAngle=4.71239 EndAngle=6.10865
    g9: GeomPoint X=147.346 Y=8 Z=0
    g10: LineSegment StartX=151.541 StartY=0 StartZ=0 EndX=151.541 EndY=3 EndZ=0
    g11: LineSegment StartX=151.541 StartY=3 StartZ=0 EndX=154.496 EndY=2.47906 EndZ=0
    g12: ArcOfCircle CenterX=154.461 CenterY=25.3148 CenterZ=0 NormalX=0 NormalY=0 NormalZ=1 AngleXU=0 Radius=4 StartAngle=1.39626 EndAngle=2.96706
    g13: GeomPoint X=151.216 Y=29.9486 Z=0
    g14: LineSegment StartX=155.272 StartY=24.1563 StartZ=0 EndX=151.216 EndY=29.9486 EndZ=0
    g15: LineSegment StartX=151.541 StartY=3 StartZ=0 EndX=146.617 EndY=3.86824 EndZ=0
  constraints (44):
    c: Horizontal(g0)
    c: Coincident(g0,g1)
    c: Coincident(g1,g2)
    c: Coincident(g2,g3)
    c: Coincident(g3,g4)
    c: Horizontal(g6)
    c: Coincident(g6,g7)
    c: Coincident(g7,g0)
    c: Vertical(g7)
    c: PointOnObject(g9,g5)
    c: PointOnObject(g9,g6)
    c: Tangent(g5,g8) = 1.5708
    c: Tangent(g6,g8) = 1.5708
    c: PointOnObject(g10,g-1)
    c: Coincident(g10,g0)
    c: Vertical(g10)
    c: Coincident(g10,g11)
    c: PointOnObject(g11,g-3)
    c: Perpendicular(g-3,g11)
    c: Perpendicular(g1,g11)
    c: Equal(g10,g11)
    c: DistanceY(g10,g10) = 3
    c: Perpendicular(g-3,g2)
    c: PointOnObject(g-3,g2)
    c: DistanceX(g-3,g3) = 25
    c: PointOnObject(g13,g4)
    c: PointOnObject(g13,g5)
    c: Tangent(g4,g12) = -1.5708
    c: Tangent(g5,g12) = -1.5708
    c: Coincident(g14,g1)
    c: Coincident(g14,g13)
    c: PointOnObject(g12,g14)
    c: Parallel(g5,g1)
    c: Coincident(g15,g0)
    c: PointOnObject(g15,g5)
    c: Perpendicular(g5,g15)
    c: Distance(g15) = 5
    c: Equal(g8,g12)
    c: Equal(g15,g7)
    c: Radius(g8) = 4
    c: DistanceX(g0,g0) = 25
    c: Parallel(g2,g4)
    c: Vertical(g3)
    c: DistanceX(g2) = 183.226  'total_length'
FEATURE [PartDesign::Pad] Pad016
  Direction = (1,0,0)
  Length = 15
  Length2 = 10
  Midplane = true
  Placement = pos=(0,0,0) rot=(0.57735,0.57735,0.57735;2.0944rad)
  Profile = -> Sketch061
  ReferenceAxis = -> Sketch061 [N_Axis]
  Type = 0
FEATURE [Part::Compound] Compound024  label="led_holder_cut1"
  Links = -> [Populate029]
FEATURE [PartDesign::Boolean] Boolean013
  BaseFeature = -> Pad016
  Group = -> [Compound024]
  Type = 1
FEATURE [PartDesign::Body] Body015  label="led_holder"
  Group = -> [Sketch061,Binder023,Binder024,Pad016,Boolean013]
  Origin = -> Origin018
  Tip = -> Boolean013
FEATURE [Part::FeaturePython] Placment012  # WARN: FeaturePython — macro-defined, semantics opaque (R4)
  AttacherType = Attacher::AttachEngine3D
  ExposePlacement = true
  MarkerShape = 1
  MarkerSize = 10
  NumElements = 1
  Placement = pos=(0,-15,0) rot=(0,0,1;0rad)
  Type = lattice2AttachablePlacement.AttachablePlacement
  isLattice = 1
FEATURE [Part::FeaturePython] Populate031  label="Populate Placment012 with Extrude006"  # WARN: FeaturePython — macro-defined, semantics opaque (R4)
  Copying = 0
  ExposePlacement = false
  MarkerShape = 1
  MarkerSize = 0
  NumElements = 0
  Object = -> Extrude006
  OutputCompounding = 2
  PlacementsTo = -> Placment012
  Referencing = 0
  Type = lattice2PopulateCopies.LatticePopulateCopies
  isLattice = 0
FEATURE [Part::Compound] Compound025  label="sink2_cut1"
  Links = -> [Populate031]
FEATURE [App::Part] Part003  label="bar_part"
  Group = -> [Spreadsheet001,Body009,Body010]
  Origin = -> Origin019
FEATURE [Part::MultiFuse] Fusion001
  Shapes = -> [Extrude002,Populate009]
FEATURE [Part::Compound] Compound009  label="top_dropper_fix_cut1"
  Links = -> [Fusion001]
FEATURE [PartDesign::Boolean] Boolean002
  BaseFeature = -> Mirrored001
  Group = -> [Compound009]
  Type = 1
FEATURE [PartDesign::Body] Body003  label="top_dropper_fix"
  Group = -> [Binder006,Sketch016,Pad001,Mirrored001,Boolean002,Binder008]
  Origin = -> Origin004
  Placement = pos=(0,0,3) rot=(0,0,1;0rad)
  Tip = -> Boolean002
FEATURE [PartDesign::FeaturePython] Bend004  # WARN: FeaturePython — macro-defined, semantics opaque (R4)
  AutoMiter = true
  BaseFeature = -> Pad014
  BendType = 0
  LengthList = [50]
  LengthSpec = 0
  ReliefFactor = 0.7
  UseReliefFactor = false
  angle = 40
  baseObject = -> Pad014 [Edge3]
  bendAList = [40]
  extend1 = 0
  extend2 = 0
  gap1 = 0
  gap2 = 0
  invert = false
  kfactor = 0.5
  length = 50
  maxExtendDist = 5
  minGap = 0.1
  minReliefGap = 1
  miterangle1 = 0
  miterangle2 = 0
  offset = 0
  radius = 1
  reliefType = 0
  reliefd = 1
  reliefw = 0.8
  sketchflip = false
  sketchinvert = false
  unfold = false
FEATURE [Sketcher::SketchObject] Sketch062
  ExternalGeometry = -> [Bend004]
  FullyConstrained = true
  MapMode = 5
  Placement = pos=(0,0.407604,0.34202) rot=(0,0.422618,0.906308;3.14159rad)
  Support = -> [Bend004]
  sketch-geometry (3):
    g0: LineSegment StartX=325.502 StartY=-51.2856 StartZ=0 EndX=-193.217 EndY=-24.1006 EndZ=0
    g1: LineSegment StartX=-193.217 StartY=-24.1006 StartZ=0 EndX=-193.217 EndY=-51.2856 EndZ=0
    g2: LineSegment StartX=-193.217 StartY=-51.2856 StartZ=0 EndX=325.502 EndY=-51.2856 EndZ=0
  constraints (7):
    c: Coincident(g0,g1)
    c: Vertical(g1)
    c: Angle(g0) = 3.08923
    c: Coincident(g0,g-4)
    c: Coincident(g1,g-4)
    c: Coincident(g2,g1)
    c: Coincident(g2,g0)
FEATURE [PartDesign::Pocket] Pocket012
  BaseFeature = -> Bend004
  Direction = (0,-0.766044,-0.642788)
  Length = 5
  Length2 = 5
  Profile = -> Sketch062
  ReferenceAxis = -> Sketch062 [N_Axis]
  Type = 0
FEATURE [PartDesign::FeaturePython] Bend005  # WARN: FeaturePython — macro-defined, semantics opaque (R4)
  AutoMiter = true
  BaseFeature = -> Pocket012
  BendType = 0
  LengthList = [20]
  LengthSpec = 0
  ReliefFactor = 0.7
  UseReliefFactor = false
  angle = 90
  baseObject = -> Pocket012 [Edge10]
  bendAList = [90]
  extend1 = 0
  extend2 = 0
  gap1 = 0
  gap2 = 0
  invert = false
  kfactor = 0.5
  length = 20
  maxExtendDist = 5
  minGap = 0.1
  minReliefGap = 1
  miterangle1 = 0
  miterangle2 = 0
  offset = 0
  radius = 1
  reliefType = 0
  reliefd = 1
  reliefw = 0.8
  sketchflip = false
  sketchinvert = false
  unfold = false
  expr: radius = Bend004.radius
FEATURE [PartDesign::Boolean] Boolean014
  BaseFeature = -> Bend005
  Group = -> [Compound025]
  Type = 1
FEATURE [PartDesign::Fillet] Fillet002
  Base = -> Boolean014 [Edge36,Edge2,Edge8,Edge50]
  BaseFeature = -> Boolean014
  Radius = 11
  SupportTransform = false
  UseAllEdges = false
FEATURE [PartDesign::Body] Body011  label="sink2_material_0.30ansi"
  Group = -> [Binder016,Pad014,Bend004,Sketch062,Pocket012,Bend005,Boolean014,Fillet002]
  Origin = -> Origin014
  Placement = pos=(0,17,0) rot=(0,0,1;0rad)
  Tip = -> Fillet002
  expr: .Placement.Base.y = <<base_sketch>>.Constraints.offset - 3 mm - 1 mm
FEATURE [TechDraw::DrawViewPart] View008
  CoarseView = false
  Direction = (0,1,0)
  Focus = 100
  HardHidden = false
  IsoCount = 0
  IsoHidden = false
  IsoVisible = false
  LockPosition = false
  Perspective = false
  Rotation = 0
  Scale = 0.5
  ScaleType = 2
  ScrubCount = 0
  SeamHidden = false
  SeamVisible = true
  SmoothHidden = false
  SmoothVisible = true
  Source = -> [Body011]
  X = 165.7
  XDirection = (-1,0,0)
  Y = 184.675
FEATURE [TechDraw::DrawViewPart] View009
  CoarseView = false
  Direction = (1,0,0)
  Focus = 100
  HardHidden = false
  IsoCount = 0
  IsoHidden = false
  IsoVisible = false
  LockPosition = false
  Perspective = false
  Rotation = 0
  ScaleType = 0
  ScrubCount = 0
  SeamHidden = false
  SeamVisible = true
  SmoothHidden = false
  SmoothVisible = true
  Source = -> [Body011]
  X = 48.5
  XDirection = (0,1,0)
  Y = 55
FEATURE [TechDraw::DrawViewPart] View010
  CoarseView = false
  Direction = (0.99863,-0.033641,0.040092)
  Focus = 100
  HardHidden = false
  IsoCount = 0
  IsoHidden = false
  IsoVisible = false
  LockPosition = false
  Perspective = false
  Rotation = 0
  ScaleType = 0
  ScrubCount = 0
  SeamHidden = false
  SeamVisible = true
  SmoothHidden = false
  SmoothVisible = true
  Source = -> [Body011]
  X = 258.5
  XDirection = (0.0336681,0.999434,-1.89271e-07)
  Y = 95
FEATURE [TechDraw::DrawViewDimension] Dimension010
  AngleOverride = false
  Arbitrary = false
  ArbitraryTolerances = false
  EqualTolerance = true
  ExtensionAngle = 0
  FormatSpec = %.2w
  FormatSpecOverTolerance = %+.2w
  FormatSpecUnderTolerance = %+.2w
  Inverted = false
  LineAngle = 0
  LockPosition = false
  MeasureType = 1
  OverTolerance = 0
  References2D = -> [View009]
  Rotation = 0
  ScaleType = 0
  TheoreticalExact = false
  Type = 6
  UnderTolerance = 0
  X = -11.9973
  Y = 14.2181
FEATURE [TechDraw::DrawViewDimension] Dimension011
  AngleOverride = false
  Arbitrary = false
  ArbitraryTolerances = false
  EqualTolerance = true
  ExtensionAngle = 0
  FormatSpec = %.2w
  FormatSpecOverTolerance = %+.2w
  FormatSpecUnderTolerance = %+.2w
  Inverted = false
  LineAngle = 0
  LockPosition = false
  MeasureType = 1
  OverTolerance = 0
  References2D = -> [View010]
  Rotation = 0
  ScaleType = 0
  TheoreticalExact = false
  Type = 6
  UnderTolerance = 0
  X = 4.65944
  Y = -15.7142
FEATURE [Part::Feature] Unfold003
  shape: bbox 500.6 x 1 x 108.4 mm, 15 faces (baked)
FEATURE [Sketcher::SketchObject] Unfold_Sketch_Outline003
  FullyConstrained = false
  sketch-geometry (10):
    g0: LineSegment StartX=-24.7028 StartY=187.646 StartZ=0 EndX=-35.7297 EndY=188.224 EndZ=0
    g1: ArcOfCircle CenterX=-36.3054 CenterY=177.239 CenterZ=0 NormalX=0 NormalY=0 NormalZ=1 AngleXU=-0.0523599 Radius=11 StartAngle=1.5708 EndAngle=3.14159
    g2: LineSegment StartX=-47.2903 StartY=177.815 StartZ=0 EndX=-72.3437 EndY=-300.232 EndZ=0
    g3: ArcOfCircle CenterX=-61.3588 CenterY=-300.808 CenterZ=0 NormalX=0 NormalY=0 NormalZ=1 AngleXU=-0.0523599 Radius=11 StartAngle=3.14159 EndAngle=4.71239
    g4: LineSegment StartX=-61.9345 StartY=-311.793 StartZ=0 EndX=-50.9076 EndY=-312.37 EndZ=0
    g5: LineSegment StartX=25 StartY=-312.37 StartZ=0 EndX=-50.9076 EndY=-312.37 EndZ=0
    g6: ArcOfCircle CenterX=25 CenterY=-301.37 CenterZ=0 NormalX=0 NormalY=0 NormalZ=1 AngleXU=0 Radius=11 StartAngle=4.71239 EndAngle=6.28319
    g7: LineSegment StartX=36 StartY=176.646 StartZ=0 EndX=36 EndY=-301.37 EndZ=0
    g8: ArcOfCircle CenterX=25 CenterY=176.646 CenterZ=0 NormalX=0 NormalY=0 NormalZ=1 AngleXU=0 Radius=11 StartAngle=0 EndAngle=1.5708
    g9: LineSegment StartX=-24.7028 StartY=187.646 StartZ=0 EndX=25 EndY=187.646 EndZ=0
FEATURE [Sketcher::SketchObject] Unfold_Sketch_Internal001
  FullyConstrained = false
  sketch-geometry (3):
    g0: Circle CenterX=30 CenterY=0 CenterZ=0 NormalX=0 NormalY=0 NormalZ=1 AngleXU=-1.5708 Radius=1.7
    g1: Circle CenterX=30 CenterY=154 CenterZ=0 NormalX=0 NormalY=0 NormalZ=1 AngleXU=-1.5708 Radius=1.7
    g2: Circle CenterX=30 CenterY=-154 CenterZ=0 NormalX=0 NormalY=0 NormalZ=1 AngleXU=-1.5708 Radius=1.7
FEATURE [Sketcher::SketchObject] Unfold_Sketch_bends003
  FullyConstrained = false
  sketch-geometry (2):
    g0: LineSegment StartX=-25.7224 StartY=187.7 StartZ=0 EndX=-51.9272 EndY=-312.317 EndZ=0
    g1: LineSegment StartX=-0.453786 StartY=-312.37 StartZ=0 EndX=-0.453786 EndY=187.646 EndZ=0
FEATURE [Sketcher::SketchObject] Unfold_Sketch003  label="Unfold_Sketch"
  ExternalGeometry = -> [Unfold_Sketch_bends003]
  FullyConstrained = false
  sketch-geometry (17):
    g0: ArcOfCircle CenterX=25 CenterY=-301.37 CenterZ=0 NormalX=0 NormalY=0 NormalZ=1 AngleXU=0 Radius=11 StartAngle=4.71239 EndAngle=6.28319
    g1: LineSegment StartX=36 StartY=176.646 StartZ=0 EndX=36 EndY=-301.37 EndZ=0
    g2: ArcOfCircle CenterX=25 CenterY=176.646 CenterZ=0 NormalX=0 NormalY=0 NormalZ=1 AngleXU=0 Radius=11 StartAngle=0 EndAngle=1.5708
    g3: ArcOfCircle CenterX=-36.3054 CenterY=177.239 CenterZ=0 NormalX=0 NormalY=0 NormalZ=1 AngleXU=-0.0523599 Radius=11 StartAngle=1.5708 EndAngle=3.14159
    g4: LineSegment StartX=-47.2903 StartY=177.815 StartZ=0 EndX=-72.3437 EndY=-300.232 EndZ=0
    g5: ArcOfCircle CenterX=-61.3588 CenterY=-300.808 CenterZ=0 NormalX=0 NormalY=0 NormalZ=1 AngleXU=-0.0523599 Radius=11 StartAngle=3.14159 EndAngle=4.71239
    g6: Circle CenterX=30 CenterY=0 CenterZ=0 NormalX=0 NormalY=0 NormalZ=1 AngleXU=-1.5708 Radius=1.7
    g7: Circle CenterX=30 CenterY=-154 CenterZ=0 NormalX=0 NormalY=0 NormalZ=1 AngleXU=-1.5708 Radius=1.7
    g8: Circle CenterX=30 CenterY=154 CenterZ=0 NormalX=0 NormalY=0 NormalZ=1 AngleXU=-1.5708 Radius=1.7
    g9: LineSegment StartX=-24.7028 StartY=187.646 StartZ=0 EndX=-35.7297 EndY=188.224 EndZ=0
    g10: LineSegment StartX=-61.9345 StartY=-311.793 StartZ=0 EndX=-50.9076 EndY=-312.37 EndZ=0
    g11: LineSegment StartX=25 StartY=-312.37 StartZ=0 EndX=-50.9076 EndY=-312.37 EndZ=0
    g12: LineSegment StartX=-24.7028 StartY=187.646 StartZ=0 EndX=25 EndY=187.646 EndZ=0
    g13: LineSegment StartX=-0.453786 StartY=-312.37 StartZ=0 EndX=-0.453786 EndY=-310.37 EndZ=0
    g14: LineSegment StartX=-51.9272 StartY=-312.317 StartZ=0 EndX=-51.8225 EndY=-310.32 EndZ=0
    g15: LineSegment StartX=-0.453786 StartY=187.646 StartZ=0 EndX=-0.453786 EndY=185.646 EndZ=0
    g16: LineSegment StartX=-25.7224 StartY=187.7 StartZ=0 EndX=-25.8271 EndY=185.702 EndZ=0
  constraints (22):
    c: Coincident(g13,g-4)
    c: PointOnObject(g13,g-4)
    c: Coincident(g14,g-3)
    c: PointOnObject(g14,g-3)
    c: Coincident(g15,g-4)
    c: PointOnObject(g15,g-4)
    c: Coincident(g16,g-3)
    c: PointOnObject(g16,g-3)
    c: Equal(g16,g15)
    c: Equal(g15,g13)
    c: Equal(g13,g14)
    c: Distance(g13) = 2
    c: Coincident(g4,g5)
    c: Coincident(g5,g10)
    c: Coincident(g10,g11)
    c: Coincident(g3,g4)
    c: Coincident(g3,g9)
    c: Coincident(g9,g12)
    c: Coincident(g0,g11)
    c: Coincident(g2,g12)
    c: Coincident(g0,g1)
    c: Coincident(g1,g2)
FEATURE [Part::Mirroring] Part__Mirroring013  label="Unfold_Sketch (Mirror #14)"
  Base = (0,0,0)
  Normal = (1,0,0)
  Source = -> Unfold_Sketch003
FEATURE [Part::Mirroring] Part__Mirroring014  label="sink2_material_0.30ansi (Mirror #15)"
  Base = (0,0,0)
  Normal = (1,0,0)
  Source = -> Body011
FEATURE [TechDraw::DrawViewPart] View011
  CoarseView = false
  Direction = (0,1,0)
  Focus = 100
  HardHidden = false
  IsoCount = 0
  IsoHidden = false
  IsoVisible = false
  LockPosition = false
  Perspective = false
  Rotation = 0
  Scale = 0.5
  ScaleType = 1
  ScrubCount = 0
  SeamHidden = false
  SeamVisible = true
  SmoothHidden = false
  SmoothVisible = true
  Source = -> [Part__Mirroring014]
  X = 148.5
  XDirection = (-1,0,0)
  Y = 185
FEATURE [TechDraw::DrawViewPart] View012
  CoarseView = false
  Direction = (-1,0,0)
  Focus = 100
  HardHidden = false
  IsoCount = 0
  IsoHidden = false
  IsoVisible = false
  LockPosition = false
  Perspective = false
  Rotation = 0
  ScaleType = 0
  ScrubCount = 0
  SeamHidden = false
  SeamVisible = true
  SmoothHidden = false
  SmoothVisible = true
  Source = -> [Part__Mirroring014]
  X = 38.5
  XDirection = (0,-1,0)
  Y = 51
FEATURE [TechDraw::DrawViewPart] View013
  CoarseView = false
  Direction = (-0.99863,-0.033641,0.040092)
  Focus = 100
  HardHidden = false
  IsoCount = 0
  IsoHidden = false
  IsoVisible = false
  LockPosition = false
  Perspective = false
  Rotation = 0
  ScaleType = 0
  ScrubCount = 0
  SeamHidden = false
  SeamVisible = true
  SmoothHidden = false
  SmoothVisible = true
  Source = -> [Part__Mirroring014]
  X = 38.5
  XDirection = (0.0336681,-0.999434,1.89271e-07)
  Y = 120
FEATURE [TechDraw::DrawViewPart] View014
  CoarseView = false
  Direction = (0.57735,0.57735,0.57735)
  Focus = 100
  HardHidden = false
  IsoCount = 0
  IsoHidden = false
  IsoVisible = false
  LockPosition = false
  Perspective = false
  Rotation = 0
  Scale = 0.55
  ScaleType = 2
  ScrubCount = 0
  SeamHidden = false
  SeamVisible = true
  SmoothHidden = false
  SmoothVisible = true
  Source = -> [Part__Mirroring014]
  X = 191.126
  XDirection = (-0.707107,0.707107,0)
  Y = 84.7065
FEATURE [TechDraw::DrawViewDimension] Dimension012
  AngleOverride = false
  Arbitrary = false
  ArbitraryTolerances = false
  EqualTolerance = true
  ExtensionAngle = 0
  FormatSpec = %.2w
  FormatSpecOverTolerance = %+.2w
  FormatSpecUnderTolerance = %+.2w
  Inverted = false
  LineAngle = 0
  LockPosition = false
  MeasureType = 1
  OverTolerance = 0
  References2D = -> [View012]
  Rotation = 0
  ScaleType = 0
  TheoreticalExact = false
  Type = 6
  UnderTolerance = 0
  X = 12.5562
  Y = 8.12862
FEATURE [TechDraw::DrawViewDimension] Dimension013
  AngleOverride = false
  Arbitrary = false
  ArbitraryTolerances = false
  EqualTolerance = true
  ExtensionAngle = 0
  FormatSpec = %.2w
  FormatSpecOverTolerance = %+.2w
  FormatSpecUnderTolerance = %+.2w
  Inverted = false
  LineAngle = 0
  LockPosition = false
  MeasureType = 1
  OverTolerance = 0
  References2D = -> [View013]
  Rotation = 0
  ScaleType = 0
  TheoreticalExact = false
  Type = 6
  UnderTolerance = 0
  X = -8.82471
  Y = -14.0995
FEATURE [TechDraw::DrawPage] Page004
  KeepUpdated = true
  NextBalloonIndex = 1
  ProjectionType = 0
  Template = -> Template
  Views = -> [View011,View012,View013,View014,Dimension012,Dimension013]
FEATURE [App::DocumentObjectGroup] Group007  label="drain2_mirror"
  Group = -> [Page004,Part__Mirroring014,Part__Mirroring013]
FEATURE [TechDraw::DrawViewPart] View015
  CoarseView = false
  Direction = (-0.57735,0.57735,0.57735)
  Focus = 100
  HardHidden = false
  IsoCount = 0
  IsoHidden = false
  IsoVisible = false
  LockPosition = false
  Perspective = false
  Rotation = 0
  Scale = 0.6
  ScaleType = 2
  ScrubCount = 0
  SeamHidden = false
  SeamVisible = true
  SmoothHidden = false
  SmoothVisible = true
  Source = -> [Body011]
  X = 120.554
  XDirection = (-0.707107,-0.707107,0)
  Y = 91.2908
FEATURE [TechDraw::DrawPage] Page003
  KeepUpdated = true
  NextBalloonIndex = 1
  ProjectionType = 0
  Template = -> Template
  Views = -> [View008,View009,View010,Dimension010,Dimension011,View015]
FEATURE [App::DocumentObjectGroup] Group006  label="drain2"
  Group = -> [Unfold003,Unfold_Sketch003,Unfold_Sketch_Outline003,Unfold_Sketch_Internal001,Unfold_Sketch_bends003,Page003]
FEATURE [App::DocumentObjectGroup] Group002  label="metal_unfold"
  Group = -> [Group003,Group004,Group005,Group006,Group007]
FEATURE [PartDesign::SubShapeBinder] Binder025
  BindCopyOnChange = 0
  BindMode = 0
  ClaimChildren = true
  Context = -> Part [Part001.Body005.Binder025.]
  Fuse = false
  MakeFace = true
  OffsetFill = false
  OffsetIntersection = false
  OffsetJoinType = 0
  OffsetOpenResult = false
  PartialLoad = false
  Placement = pos=(0,0,40) rot=(0,0,1;0rad)
  Relative = false
  Support = -> [CapCornerCut]
  _Version = 2
FEATURE [PartDesign::Pocket] Pocket013
  BaseFeature = -> Bend003
  Direction = (0,0,1)
  Length = 5
  Length2 = 5
  Profile = -> Binder025
  Type = 0
FEATURE [PartDesign::Boolean] Boolean003
  BaseFeature = -> Pocket013
  Group = -> [Compound010]
  Type = 0
FEATURE [PartDesign::Pocket] Pocket003
  BaseFeature = -> Boolean003
  Direction = (0,0,-1)
  Length = 5
  Length2 = 5
  Profile = -> Binder012
  Reversed = true
  Type = 1
FEATURE [PartDesign::Boolean] Boolean011
  BaseFeature = -> Pocket003
  Group = -> [Compound021]
  Type = 1
FEATURE [PartDesign::Mirrored] Mirrored003
  BaseFeature = -> Boolean011
  MirrorPlane = -> DatumPlane001
  Originals = -> [Pocket003]
  Refine = true
FEATURE [PartDesign::Body] Body005  label="cap_outer_material_0.30ansi"
  Group = -> [Binder010,BaseBend003,Bend003,Binder025,Pocket013,Boolean003,Binder012,Pocket003,DatumPlane001,Boolean011,Mirrored003]
  Origin = -> Origin007
  Tip = -> Pocket013
FEATURE [PartDesign::FeaturePython] BaseBend009  # WARN: FeaturePython — macro-defined, semantics opaque (R4)
  BendSide = 0
  BendSketch = -> Sketch059
  MidPlane = false
  Reverse = false
  length = 100
  radius = 0.1
  thickness = 0.3
FEATURE [PartDesign::FeaturePython] Bend006  # WARN: FeaturePython — macro-defined, semantics opaque (R4)
  AutoMiter = true
  BaseFeature = -> BaseBend009
  BendType = 0
  LengthList = [40]
  LengthSpec = 0
  ReliefFactor = 0.7
  UseReliefFactor = false
  angle = 90
  baseObject = -> BaseBend009 [Edge16]
  bendAList = [90]
  extend1 = 0
  extend2 = 0
  gap1 = 0
  gap2 = 0
  invert = false
  kfactor = 0.5
  length = 40
  maxExtendDist = 5
  minGap = 0.2
  minReliefGap = 1
  miterangle1 = 0
  miterangle2 = 0
  offset = 0
  radius = 0.1
  reliefType = 0
  reliefd = 1
  reliefw = 0.8
  sketchflip = false
  sketchinvert = false
  unfold = false
  expr: radius = BaseBend009.radius
FEATURE [PartDesign::FeaturePython] Bend007  # WARN: FeaturePython — macro-defined, semantics opaque (R4)
  AutoMiter = true
  BaseFeature = -> Bend006
  BendType = 0
  LengthList = [30]
  LengthSpec = 0
  ReliefFactor = 0.7
  UseReliefFactor = false
  angle = 90
  baseObject = -> Bend006 [Edge3]
  bendAList = [90]
  extend1 = 0
  extend2 = 0
  gap1 = 3
  gap2 = 6
  invert = false
  kfactor = 0.5
  length = 30
  maxExtendDist = 5
  minGap = 0.2
  minReliefGap = 1
  miterangle1 = 0
  miterangle2 = 0
  offset = 0
  radius = 0.1
  reliefType = 0
  reliefd = 1
  reliefw = 0.8
  sketchflip = false
  sketchinvert = false
  unfold = false
  expr: radius = BaseBend009.radius
FEATURE [PartDesign::FeaturePython] Bend008  # WARN: FeaturePython — macro-defined, semantics opaque (R4)
  AutoMiter = true
  BaseFeature = -> Bend007
  BendType = 0
  LengthList = [60]
  LengthSpec = 0
  ReliefFactor = 0.7
  UseReliefFactor = false
  angle = 90
  baseObject = -> Bend007 [Edge3]
  bendAList = [90]
  extend1 = 0
  extend2 = 0
  gap1 = 0
  gap2 = 0
  invert = false
  kfactor = 0.5
  length = 60
  maxExtendDist = 5
  minGap = 0.2
  minReliefGap = 1
  miterangle1 = 0
  miterangle2 = 0
  offset = 0
  radius = 0.1
  reliefType = 0
  reliefd = 1
  reliefw = 0.8
  sketchflip = false
  sketchinvert = false
  unfold = false
  expr: radius = BaseBend009.radius
FEATURE [PartDesign::Boolean] Boolean010
  BaseFeature = -> Bend008
  Group = -> [Compound022]
  Type = 1
FEATURE [PartDesign::Body] Body014  label="cap_inner"
  Group = -> [Binder021,Sketch059,BaseBend009,Bend006,Bend007,Bend008,Boolean010,Binder022]
  Origin = -> Origin017
  Placement = pos=(0,0,37.1) rot=(0,0,1;0rad)
  Tip = -> Bend008
FEATURE [App::Part] Part001  label="cap"
  Group = -> [Body005,Body014]
  Origin = -> Origin006
FEATURE [App::Part] Part  label="top"
  Group = -> [Body002,Body003,Body004,Part001]
  Origin = -> Origin002
  Placement = pos=(0,0,755) rot=(0,0,1;0rad)
  expr: .Placement.Base.z = <<Properties>>.face_height
FEATURE [App::DocumentObjectGroup] Group001  label="parts"
  Group = -> [Body,Part,Part002,Body011,Body012,Body013,Body015,Part003]
FEATURE [Sketcher::SketchObject] Sketch063  label="door_plexiglas_BaseSketch"
  FullyConstrained = true
  sketch-geometry (1):
    g0: LineSegment StartX=0 StartY=0 StartZ=0 EndX=244.572 EndY=0 EndZ=0
  constraints (3):
    c: Coincident(g0,g-1)
    c: Horizontal(g0)
    c: DistanceX(g0) = 244.572  'length'
FEATURE [PartDesign::SubShapeBinder] Binder026
  BindCopyOnChange = 0
  BindMode = 0
  ClaimChildren = true
  Context = -> Part004 [Body016.Binder026.]
  Fuse = false
  MakeFace = true
  OffsetFill = false
  OffsetIntersection = false
  OffsetJoinType = 0
  OffsetOpenResult = false
  PartialLoad = false
  Relative = false
  Support = -> [Sketch063]
  _Version = 2
  expr: Support = <<door_plexiglas_BaseSketch>>._self
FEATURE [PartDesign::FeaturePython] BaseBend010  # WARN: FeaturePython — macro-defined, semantics opaque (R4)
  BendSide = 1
  BendSketch = -> Binder026
  MidPlane = false
  Reverse = false
  length = 100
  radius = 1
  thickness = 4
FEATURE [PartDesign::Body] Body016  label="door_plexiglass"
  Group = -> [BaseBend010,Binder026]
  Origin = -> Origin020
  Tip = -> BaseBend010
FEATURE [PartDesign::Body] Body017  label="door_fix"
  Origin = -> Origin022
FEATURE [App::Part] Part004  label="door"
  Group = -> [Body016,Body017]
  Origin = -> Origin021
FEATURE [Part::FeaturePython] CapCornerCut  # WARN: FeaturePython — macro-defined, semantics opaque (R4)
  CompositBendRadius = 0.1
  CompositThickness = 0.3
  Offset = 0.1
  Source = -> Sketch018
note: 1 file-system path scrubbed to <path> (originals preserved in the JSON sidecar)

RESOLVED EXTERNAL PARTS (link-assembly join: the EXTERNAL_REF files above that resolve inside this repo's crawl, each included once):
---- part dropper.FCStd = doc fcstd_03601a3bb068 ----
FCSTD DOCUMENT  (FreeCAD 1.1R38827 (Git))
Label: dropper
License: All rights reserved
LicenseURL: http://en.wikipedia.org/wiki/All_rights_reserved
objects: Sketcher::SketchObject×9, Part::FeaturePython×4, PartDesign::Revolution×3, PartDesign::Body×2, PartDesign::CoordinateSystem×1, Spreadsheet::Sheet×1, PartDesign::SubShapeBinder×1, PartDesign::Pad×1, PartDesign::Pocket×1, PartDesign::Groove×1, App::Part×1
note: 44 computed .brp shape members not serialized (recipe doc carries the construction recipe); baked Part::Feature solids carry a one-line shape summary decoded from their .brp

FEATURE [Sketcher::SketchObject] Sketch005
  ArcFitTolerance = 0
  AttachmentSupport = -> [YZ_Plane001]
  FullyConstrained = true
  MakeInternals = false
  MapMode = 5
  Placement = pos=(0,0,0) rot=(0.57735,0.57735,0.57735;2.0944rad)
  sketch-geometry (14):
    g0: LineSegment StartX=11.3 StartY=0 StartZ=0 EndX=11.3 EndY=1 EndZ=0
    g1: LineSegment StartX=11.3 StartY=1 StartZ=0 EndX=10.7 EndY=1 EndZ=0
    g2: LineSegment StartX=10.7 StartY=1 StartZ=0 EndX=10.7 EndY=9.9 EndZ=0
    g3: LineSegment StartX=10.7 StartY=9.9 StartZ=0 EndX=6.6 EndY=9.9 EndZ=0
    g4: LineSegment StartX=6.6 StartY=9.9 StartZ=0 EndX=6.6 EndY=3 EndZ=0
    g5: LineSegment StartX=6.6 StartY=3 StartZ=0 EndX=2.5 EndY=3 EndZ=0
    g6: LineSegment StartX=2.5 StartY=3 StartZ=0 EndX=2.5 EndY=20 EndZ=0
    g7: LineSegment StartX=2.5 StartY=20 StartZ=0 EndX=1.45 EndY=20 EndZ=0
    g8: LineSegment StartX=1.45 StartY=20 StartZ=0 EndX=1.45 EndY=2.5 EndZ=0
    g9: LineSegment StartX=1.45 StartY=2.5 StartZ=0 EndX=7 EndY=-0.6 EndZ=0
    g10: LineSegment StartX=7 StartY=-0.6 StartZ=0 EndX=7 EndY=8.85 EndZ=0
    g11: LineSegment StartX=7 StartY=8.85 StartZ=0 EndX=9.5 EndY=8.85 EndZ=0
    g12: LineSegment StartX=9.5 StartY=8.85 StartZ=0 EndX=9.5 EndY=0 EndZ=0
    g13: LineSegment StartX=9.5 StartY=0 StartZ=0 EndX=11.3 EndY=0 EndZ=0
  constraints (43):
    c: PointOnObject(g0,g-1)
    c: Vertical(g0)
    c: Coincident(g0,g1)
    c: Horizontal(g1)
    c: Coincident(g1,g2)
    c: Vertical(g2)
    c: Coincident(g2,g3)
    c: Horizontal(g3)
    c: Coincident(g3,g4)
    c: Vertical(g4)
    c: Coincident(g4,g5)
    c: Coincident(g5,g6)
    c: Vertical(g6)
    c: Coincident(g6,g7)
    c: Horizontal(g7)
    c: Coincident(g7,g8)
    c: Vertical(g8)
    c: Coincident(g8,g9)
    c: Coincident(g9,g10)
    c: Vertical(g10)
    c: Coincident(g10,g11)
    c: Horizontal(g11)
    c: Coincident(g11,g12)
    c: Vertical(g12)
    c: Coincident(g12,g13)
    c: Coincident(g13,g0)
    c: Horizontal(g13)
    c: DistanceX(g0) = 11.3  'outer_r'
    c: DistanceY(g0) = 1
    c: DistanceY(g2) = 9.9
    c: DistanceX(g1,g0) = 0.6
    c: DistanceX(g3,g2) = 4.1
    c: DistanceY(g4,g3) = 6.9
    c: DistanceX(g6) = 2.5
    c: DistanceX(g7) = 1.45
    c: DistanceY(g9,g3) = 10.5
    c: DistanceX(g12,g0) = 1.8
    c: DistanceY(g11) = 8.85
    c: DistanceX(g9) = 7
    c: DistanceY(g9,g6) = 20.6
    c: Horizontal(g5)
    c: DistanceY(g8,g5) = 0.5
    c: DistanceY(g7) = 20
FEATURE [PartDesign::Revolution] Revolution002
  Angle = 360
  Angle2 = 60
  Axis = (0,0,1)
  Base = (0,0,0)
  Placement = pos=(0,0,0) rot=(1,1,1;2.0944rad)
  Profile = -> Sketch005
  ReferenceAxis = -> Sketch005 [V_Axis]
  Reversed = true
  Suppressed = false
  Type = 0
FEATURE [Sketcher::SketchObject] Sketch006
  ArcFitTolerance = 0
  AttachmentSupport = -> [YZ_Plane001]
  FullyConstrained = true
  MakeInternals = false
  MapMode = 5
  Placement = pos=(0,0,0) rot=(0.57735,0.57735,0.57735;2.0944rad)
  expr: Constraints[27] = Sketch005.Constraints.outer_r
  expr: Constraints[28] = Sketch005.Constraints[28]
  expr: Constraints[29] = Sketch005.Constraints[29]
  expr: Constraints[30] = Sketch005.Constraints[30]
  expr: Constraints[31] = Sketch005.Constraints[31]
  expr: Constraints[32] = Sketch005.Constraints[32]
  expr: Constraints[33] = Sketch005.Constraints[33]
  expr: Constraints[34] = Sketch005.Constraints[34]
  expr: Constraints[35] = Sketch005.Constraints[35]
  expr: Constraints[36] = Sketch005.Constraints[36]
  expr: Constraints[37] = Sketch005.Constraints[37]
  expr: Constraints[38] = Sketch005.Constraints[38]
  expr: Constraints[39] = Sketch005.Constraints[39]
  expr: Constraints[41] = Sketch005.Constraints[41]
  expr: Constraints[69] = Sketch005.Constraints.outer_r
  expr: Constraints[70] = Sketch005.Constraints[28]
  expr: Constraints[71] = Sketch005.Constraints[29]
  expr: Constraints[72] = Sketch005.Constraints[30]
  expr: Constraints[73] = Sketch005.Constraints[31]
  expr: Constraints[74] = Sketch005.Constraints[32]
  expr: Constraints[75] = Sketch005.Constraints[33]
  expr: Constraints[76] = Sketch005.Constraints[34]
  expr: Constraints[77] = Sketch005.Constraints[35]
  expr: Constraints[78] = Sketch005.Constraints[36]
  expr: Constraints[79] = Sketch005.Constraints[37]
  expr: Constraints[80] = Sketch005.Constraints[38]
  expr: Constraints[81] = Sketch005.Constraints[39]
  expr: Constraints[83] = Sketch005.Constraints[41]
  sketch-geometry (32):
    g0: LineSegment [constr] StartX=11.3 StartY=0 StartZ=0 EndX=11.3 EndY=1 EndZ=0
    g1: LineSegment [constr] StartX=11.3 StartY=1 StartZ=0 EndX=10.7 EndY=1 EndZ=0
    g2: LineSegment [constr] StartX=10.7 StartY=1 StartZ=0 EndX=10.7 EndY=9.9 EndZ=0
    g3: LineSegment [constr] StartX=10.7 StartY=9.9 StartZ=0 EndX=6.6 EndY=9.9 EndZ=0
    g4: LineSegment StartX=6.6 StartY=9.9 StartZ=0 EndX=6.6 EndY=3 EndZ=0
    g5: LineSegment StartX=6.6 StartY=3 StartZ=0 EndX=2.5 EndY=3 EndZ=0
    g6: LineSegment [constr] StartX=2.5 StartY=3 StartZ=0 EndX=2.5 EndY=20 EndZ=0
    g7: LineSegment [constr] StartX=2.5 StartY=20 StartZ=0 EndX=1.45 EndY=20 EndZ=0
    g8: LineSegment [constr] StartX=1.45 StartY=20 StartZ=0 EndX=1.45 EndY=2.5 EndZ=0
    g9: LineSegment [constr] StartX=1.45 StartY=2.5 StartZ=0 EndX=7 EndY=-0.6 EndZ=0
    g10: LineSegment [constr] StartX=7 StartY=-0.6 StartZ=0 EndX=7 EndY=8.85 EndZ=0
    g11: LineSegment [constr] StartX=7 StartY=8.85 StartZ=0 EndX=9.5 EndY=8.85 EndZ=0
    g12: LineSegment [constr] StartX=9.5 StartY=8.85 StartZ=0 EndX=9.5 EndY=0 EndZ=0
    g13: LineSegment [constr] StartX=9.5 StartY=0 StartZ=0 EndX=11.3 EndY=0 EndZ=0
    g14: LineSegment [constr] StartX=11.3 StartY=0 StartZ=0 EndX=11.3 EndY=1 EndZ=0
    g15: LineSegment [constr] StartX=11.3 StartY=1 StartZ=0 EndX=10.7 EndY=1 EndZ=0
    g16: LineSegment [constr] StartX=10.7 StartY=1 StartZ=0 EndX=10.7 EndY=9.9 EndZ=0
    g17: LineSegment [constr] StartX=10.7 StartY=9.9 StartZ=0 EndX=6.6 EndY=9.9 EndZ=0
    g18: LineSegment [constr] StartX=6.6 StartY=9.9 StartZ=0 EndX=6.6 EndY=3 EndZ=0
    g19: LineSegment [constr] StartX=6.6 StartY=3 StartZ=0 EndX=2.5 EndY=3 EndZ=0
    g20: LineSegment [constr] StartX=2.5 StartY=3 StartZ=0 EndX=2.5 EndY=20 EndZ=0
    g21: LineSegment [constr] StartX=2.5 StartY=20 StartZ=0 EndX=1.45 EndY=20 EndZ=0
    g22: LineSegment [constr] StartX=1.45 StartY=20 StartZ=0 EndX=1.45 EndY=2.5 EndZ=0
    g23: LineSegment [constr] StartX=1.45 StartY=2.5 StartZ=0 EndX=7 EndY=-0.6 EndZ=0
    g24: LineSegment [constr] StartX=7 StartY=-0.6 StartZ=0 EndX=7 EndY=8.85 EndZ=0
    g25: LineSegment [constr] StartX=7 StartY=8.85 StartZ=0 EndX=9.5 EndY=8.85 EndZ=0
    g26: LineSegment [constr] StartX=9.5 StartY=8.85 StartZ=0 EndX=9.5 EndY=0 EndZ=0
    g27: LineSegment [constr] StartX=9.5 StartY=0 StartZ=0 EndX=11.3 EndY=0 EndZ=0
    g28: LineSegment StartX=2.5 StartY=3 StartZ=0 EndX=2.04763 EndY=3 EndZ=0
    g29: LineSegment StartX=2.04763 StartY=3 StartZ=0 EndX=2.04763 EndY=12.6758 EndZ=0
    g30: LineSegment StartX=2.04763 StartY=12.6758 StartZ=0 EndX=6.6 EndY=9.9 EndZ=0
    g31: GeomPoint [constr] X=2.5 Y=12.4 Z=0
  constraints (94):
    c: PointOnObject(g0,g-1)
    c: Vertical(g0)
    c: Coincident(g0,g1)
    c: Horizontal(g1)
    c: Coincident(g1,g2)
    c: Vertical(g2)
    c: Coincident(g2,g3)
    c: Horizontal(g3)
    c: Coincident(g3,g4)
    c: Vertical(g4)
    c: Coincident(g4,g5)
    c: Coincident(g5,g6)
    c: Vertical(g6)
    c: Coincident(g6,g7)
    c: Horizontal(g7)
    c: Coincident(g7,g8)
    c: Vertical(g8)
    c: Coincident(g8,g9)
    c: Coincident(g9,g10)
    c: Vertical(g10)
    c: Coincident(g10,g11)
    c: Horizontal(g11)
    c: Coincident(g11,g12)
    c: Vertical(g12)
    c: Coincident(g12,g13)
    c: Coincident(g13,g0)
    c: Horizontal(g13)
    c: DistanceX(g0) = 11.3
    c: DistanceY(g0) = 1
    c: DistanceY(g2) = 9.9
    c: DistanceX(g1,g0) = 0.6
    c: DistanceX(g3,g2) = 4.1
    c: DistanceY(g4,g3) = 6.9
    c: DistanceX(g6) = 2.5
    c: DistanceX(g7) = 1.45
    c: DistanceY(g9,g3) = 10.5
    c: DistanceX(g12,g0) = 1.8
    c: DistanceY(g11) = 8.85
    c: DistanceX(g9) = 7
    c: DistanceY(g9,g6) = 20.6
    c: Horizontal(g5)
    c: DistanceY(g8,g5) = 0.5
    c: PointOnObject(g14,g-1)
    c: Vertical(g14)
    c: Coincident(g14,g15)
    c: Horizontal(g15)
    c: Coincident(g15,g16)
    c: Vertical(g16)
    c: Coincident(g16,g17)
    c: Horizontal(g17)
    c: Coincident(g17,g18)
    c: Vertical(g18)
    c: Coincident(g18,g19)
    c: Coincident(g19,g20)
    c: Vertical(g20)
    c: Coincident(g20,g21)
    c: Horizontal(g21)
    c: Coincident(g21,g22)
    c: Vertical(g22)
    c: Coincident(g22,g23)
    c: Coincident(g23,g24)
    c: Vertical(g24)
    c: Coincident(g24,g25)
    c: Horizontal(g25)
    c: Coincident(g25,g26)
    c: Vertical(g26)
    c: Coincident(g26,g27)
    c: Coincident(g27,g14)
    c: Horizontal(g27)
    c: DistanceX(g14) = 11.3
    c: DistanceY(g14) = 1
    c: DistanceY(g16) = 9.9
    c: DistanceX(g15,g14) = 0.6
    c: DistanceX(g17,g16) = 4.1
    c: DistanceY(g18,g17) = 6.9
    c: DistanceX(g20) = 2.5
    c: DistanceX(g21) = 1.45
    c: DistanceY(g23,g17) = 10.5
    c: DistanceX(g26,g14) = 1.8
    c: DistanceY(g25) = 8.85
    c: DistanceX(g23) = 7
    c: DistanceY(g23,g20) = 20.6
    c: Horizontal(g19)
    c: DistanceY(g22,g19) = 0.5
    c: Coincident(g28,g5)
    c: Horizontal(g28)
    c: Coincident(g29,g28)
    c: Vertical(g29)
    c: Coincident(g30,g29)
    c: Coincident(g30,g4)
    c: PointOnObject(g31,g30)
    c: PointOnObject(g31,g6)
    c: DistanceY(g4,g31) = 2.5
    c: DistanceX(g29,g31) = 0.452366
FEATURE [PartDesign::Body] Body001
  AllowCompound = false
  Group = -> [Sketch005,Revolution002,Sketch006]
  Origin = -> Origin001
  Placement = pos=(0,0,2.5) rot=(0,0,1;0rad)
  Tip = -> Revolution002
FEATURE [Sketcher::SketchObject] Sketch007  label="base"
  ArcFitTolerance = 0
  FullyConstrained = true
  MakeInternals = false
  expr: .Constraints.r = Sketch005.Constraints.outer_r + 0.5 mm
  sketch-geometry (1):
    g0: Circle CenterX=0 CenterY=0 CenterZ=0 NormalX=0 NormalY=0 NormalZ=1 AngleXU=0 Radius=11.8
  constraints (2):
    c: Coincident(g0,g-1)
    c: Radius(g0) = 11.8  'r'
FEATURE [Sketcher::SketchObject] Sketch002
  ArcFitTolerance = 0
  AttachmentSupport = -> [YZ_Plane]
  FullyConstrained = true
  MakeInternals = false
  MapMode = 5
  Placement = pos=(0,0,0) rot=(0.57735,0.57735,0.57735;2.0944rad)
  expr: Constraints[18] = Sketch001.Constraints[18]
  expr: Constraints[19] = Sketch001.Constraints[19]
  expr: Constraints[20] = Sketch001.Constraints[20]
  expr: Constraints[21] = Sketch001.Constraints[21]
  expr: Constraints[22] = Sketch001.Constraints[22]
  expr: Constraints[23] = Sketch001.Constraints[23]
  expr: Constraints[24] = Sketch001.Constraints[24]
  expr: Constraints[25] = Sketch001.Constraints[25]
  expr: Constraints[27] = Sketch001.Constraints[27]
  sketch-geometry (13):
    g0: LineSegment [constr] StartX=1.15 StartY=0 StartZ=0 EndX=1.15 EndY=-18.1612 EndZ=0
    g1: LineSegment StartX=1.15 StartY=-18.1612 StartZ=0 EndX=2.765 EndY=-8.77 EndZ=0
    g2: LineSegment [constr] StartX=2.765 StartY=-8.77 StartZ=0 EndX=2.2 EndY=-8.77 EndZ=0
    g3: LineSegment [constr] StartX=2.2 StartY=-8.77 StartZ=0 EndX=2.2 EndY=-5.32 EndZ=0
    g4: LineSegment [constr] StartX=2.2 StartY=-5.32 StartZ=0 EndX=3.35 EndY=-5.32 EndZ=0
    g5: LineSegment [constr] StartX=3.35 StartY=-5.32 StartZ=0 EndX=3.35 EndY=-3.66 EndZ=0
    g6: LineSegment [constr] StartX=3.35 StartY=-3.66 StartZ=0 EndX=2.65 EndY=-3.66 EndZ=0
    g7: LineSegment [constr] StartX=2.65 StartY=-3.66 StartZ=0 EndX=2.65 EndY=0 EndZ=0
    g8: LineSegment [constr] StartX=2.65 StartY=0 StartZ=0 EndX=1.15 EndY=0 EndZ=0
    g9: GeomPoint [constr] X=-2.765 Y=-8.77 Z=0
    g10: GeomPoint [constr] X=-2.765 Y=-8.77 Z=0
    g11: LineSegment StartX=1.15 StartY=-18.1612 StartZ=0 EndX=-3.0574 EndY=-18.1612 EndZ=0
    g12: LineSegment StartX=-3.0574 StartY=-18.1612 StartZ=0 EndX=2.765 EndY=-8.77 EndZ=0
  constraints (34):
    c: PointOnObject(g0,g-1)
    c: Vertical(g0)
    c: Coincident(g0,g1)
    c: Coincident(g1,g2)
    c: Horizontal(g2)
    c: Coincident(g2,g3)
    c: Vertical(g3)
    c: Coincident(g3,g4)
    c: Horizontal(g4)
    c: Coincident(g4,g5)
    c: Vertical(g5)
    c: Coincident(g5,g6)
    c: Horizontal(g6)
    c: Coincident(g6,g7)
    c: PointOnObject(g7,g-1)
    c: Vertical(g7)
    c: Coincident(g7,g8)
    c: Coincident(g8,g0)
    c: DistanceY(g2,g3) = 3.45
    c: DistanceY(g4,g5) = 1.66
    c: DistanceY(g6,g7) = 3.66
    c: DistanceX(g2) = 2.2
    c: DistanceX(g4) = 3.35
    c: DistanceX(g0) = 1.15
    c: DistanceX(g7) = 2.65
    c: DistanceX(g1) = 2.765
    c: Symmetric(g9,g1,g-2)
    c: Distance(g9,g1) = 5.45
    c: Symmetric(g10,g1,g-2)
    c: Coincident(g11,g1)
    c: Horizontal(g11)
    c: Coincident(g12,g11)
    c: Coincident(g12,g1)
    c: Distance(g9,g12) = 4.7
FEATURE [Sketcher::SketchObject] Sketch001
  ArcFitTolerance = 0
  AttachmentSupport = -> [XZ_Plane]
  FullyConstrained = true
  MakeInternals = false
  MapMode = 5
  Placement = pos=(0,0,0) rot=(1,0,0;1.5708rad)
  sketch-geometry (10):
    g0: LineSegment StartX=1.15 StartY=0 StartZ=0 EndX=1.15 EndY=-18.1612 EndZ=0
    g1: LineSegment StartX=1.15 StartY=-18.1612 StartZ=0 EndX=2.765 EndY=-8.77 EndZ=0
    g2: LineSegment StartX=2.765 StartY=-8.77 StartZ=0 EndX=2.2 EndY=-8.77 EndZ=0
    g3: LineSegment StartX=2.2 StartY=-8.77 StartZ=0 EndX=2.2 EndY=-5.32 EndZ=0
    g4: LineSegment StartX=2.2 StartY=-5.32 StartZ=0 EndX=3.35 EndY=-5.32 EndZ=0
    g5: LineSegment StartX=3.35 StartY=-5.32 StartZ=0 EndX=3.35 EndY=-3.66 EndZ=0
    g6: LineSegment StartX=3.35 StartY=-3.66 StartZ=0 EndX=2.65 EndY=-3.66 EndZ=0
    g7: LineSegment StartX=2.65 StartY=-3.66 StartZ=0 EndX=2.65 EndY=0 EndZ=0
    g8: LineSegment StartX=2.65 StartY=0 StartZ=0 EndX=1.15 EndY=0 EndZ=0
    g9: GeomPoint [constr] X=-2.765 Y=-8.77 Z=0
  constraints (28):
    c: PointOnObject(g0,g-1)
    c: Vertical(g0)
    c: Coincident(g0,g1)
    c: Coincident(g1,g2)
    c: Horizontal(g2)
    c: Coincident(g2,g3)
    c: Vertical(g3)
    c: Coincident(g3,g4)
    c: Horizontal(g4)
    c: Coincident(g4,g5)
    c: Vertical(g5)
    c: Coincident(g5,g6)
    c: Horizontal(g6)
    c: Coincident(g6,g7)
    c: PointOnObject(g7,g-1)
    c: Vertical(g7)
    c: Coincident(g7,g8)
    c: Coincident(g8,g0)
    c: DistanceY(g2,g3) = 3.45
    c: DistanceY(g4,g5) = 1.66
    c: DistanceY(g6,g7) = 3.66
    c: DistanceX(g2) = 2.2
    c: DistanceX(g4) = 3.35
    c: DistanceX(g0) = 1.15
    c: DistanceX(g7) = 2.65
    c: DistanceX(g1) = 2.765
    c: Symmetric(g9,g1,g-2)
    c: Distance(g9,g1) = 5.45
FEATURE [Sketcher::SketchObject] Sketch  label="fix_sketch"
  ArcFitTolerance = 0
  AttachmentSupport = -> [XY_Plane]
  FullyConstrained = true
  MakeInternals = false
  MapMode = 5
  sketch-geometry (5):
    g0: ArcOfCircle CenterX=0 CenterY=0 CenterZ=0 NormalX=0 NormalY=0 NormalZ=1 AngleXU=0 Radius=10.5 StartAngle=0.496317 EndAngle=1.5708
    g1: ArcOfCircle CenterX=16.5 CenterY=0 CenterZ=0 NormalX=0 NormalY=0 NormalZ=1 AngleXU=0 Radius=3.25 StartAngle=0 EndAngle=1.34547
    g2: LineSegment StartX=17.2261 StartY=3.16784 StartZ=0 EndX=9.23309 EndY=5 EndZ=0
    g3: GeomPoint [constr] X=-19.75 Y=0 Z=0
    g4: GeomPoint [constr] X=0 Y=-10.5 Z=0
  constraints (14):
    c: PointOnObject(g0,g-2)
    c: PointOnObject(g1,g-1)
    c: PointOnObject(g1,g-1)
    c: Coincident(g2,g0)
    c: Tangent(g2,g1) = -1.5708
    c: Diameter(g0) = 21
    c: DistanceX(g1) = 19.75
    c: DistanceY(g0) = 5
    c: Diameter(g1) = 6.5
    c: Coincident(g0,g-1)
    c: Symmetric(g3,g1,g-2)
    c: DistanceX(g3,g1) = 39.5  'length'
    c: Symmetric(g4,g0,g-1)
    c: DistanceY(g4,g0) = 21  'width'
FEATURE [Sketcher::SketchObject] Sketch004
  ArcFitTolerance = 0
  AttachmentSupport = -> [YZ_Plane]
  FullyConstrained = true
  MakeInternals = false
  MapMode = 5
  Placement = pos=(0,0,0) rot=(0.57735,0.57735,0.57735;2.0944rad)
  expr: Constraints[3] = Sketch003.Constraints[9]
  sketch-geometry (6):
    g0: LineSegment StartX=7.75 StartY=10.9 StartZ=0 EndX=0 EndY=10.9 EndZ=0
    g1: LineSegment StartX=0 StartY=10.9 StartZ=0 EndX=0 EndY=1.5 EndZ=0
    g2: LineSegment StartX=0 StartY=1.5 StartZ=0 EndX=7.25 EndY=1.5 EndZ=0
    g3: LineSegment StartX=7.25 StartY=1.5 StartZ=0 EndX=7.25 EndY=2.5 EndZ=0
    g4: LineSegment StartX=7.25 StartY=2.5 StartZ=0 EndX=7.75 EndY=4 EndZ=0
    g5: LineSegment StartX=7.75 StartY=4 StartZ=0 EndX=7.75 EndY=10.9 EndZ=0
  constraints (18):
    c: Coincident(g0,g1)
    c: Horizontal(g0)
    c: Vertical(g1)
    c: DistanceY(g0) = 10.9
    c: Horizontal(g2)
    c: Coincident(g2,g3)
    c: Vertical(g3)
    c: Coincident(g3,g4)
    c: Coincident(g4,g5)
    c: Vertical(g5)
    c: Coincident(g0,g5)
    c: Coincident(g1,g2)
    c: DistanceY(g1,g0) = 9.4
    c: DistanceX(g0) = 7.75
    c: DistanceY(g2,g3) = 1
    c: DistanceY(g3,g4) = 1.5
    c: DistanceX(g2,g4) = 0.5
    c: Vertical(g1,g-1)
FEATURE [Sketcher::SketchObject] Sketch003
  ArcFitTolerance = 0
  AttachmentSupport = -> [YZ_Plane]
  FullyConstrained = true
  MakeInternals = false
  MapMode = 5
  Placement = pos=(0,0,0) rot=(0.57735,0.57735,0.57735;2.0944rad)
  sketch-geometry (4):
    g0: LineSegment StartX=0 StartY=0 StartZ=0 EndX=8.825 EndY=0 EndZ=0
    g1: LineSegment StartX=8.825 StartY=0 StartZ=0 EndX=8.825 EndY=10.9 EndZ=0
    g2: LineSegment StartX=8.825 StartY=10.9 StartZ=0 EndX=0 EndY=10.9 EndZ=0
    g3: LineSegment StartX=0 StartY=10.9 StartZ=0 EndX=0 EndY=0 EndZ=0
  constraints (11):
    c: Coincident(g0,g1)
    c: Coincident(g1,g2)
    c: Coincident(g2,g3)
    c: Coincident(g3,g0)
    c: Horizontal(g0)
    c: Horizontal(g2)
    c: Vertical(g1)
    c: Vertical(g3)
    c: Coincident(g0,g-1)
    c: DistanceY(g2) = 10.9
    c: DistanceX(g0) = 8.825
FEATURE [PartDesign::CoordinateSystem] LCS_0
  AttacherType = Attacher::AttachEngine3D
  AttachmentOffset = pos=(0,0,2.45) rot=(0,0,1;0rad)
  AttachmentSupport = -> [X_Axis002]
  MapMode = 2
  Placement = pos=(0,0,2.45) rot=(0,0,1;0rad)
FEATURE [Spreadsheet::Sheet] Spreadsheet  label="Properties"
  cells = B2(top_d)==22.6 mm; C2(bot_d)==21 mm; D2(top_height)==20 mm; E2(bot_base_height)==2.4 mm; F2(total_height)==22.4 mm; G2(total_width)==38.9 mm
FEATURE [Part::FeaturePython] Mirror  label="Mirror of Sketch"  # WARN: FeaturePython — macro-defined, semantics opaque (R4)
  ExposePlacement = false
  FlipX = true
  FlipY = false
  FlipZ = false
  MarkerShape = 1
  MarkerSize = 0
  NumElements = 0
  Object = -> Sketch
  ObjectTraversal = 0
  Type = lattice2Mirror.LatticeMirror
  isLattice = 0
FEATURE [Part::FeaturePython] Mirror001  label="Mirror001 of Mirror of Sketch"  # WARN: FeaturePython — macro-defined, semantics opaque (R4)
  ExposePlacement = false
  FlipX = false
  FlipY = true
  FlipZ = false
  MarkerShape = 1
  MarkerSize = 0
  NumElements = 0
  Object = -> Mirror
  ObjectTraversal = 0
  Type = lattice2Mirror.LatticeMirror
  isLattice = 0
FEATURE [Part::FeaturePython] Mirror002  label="Mirror002 of Mirror001 of Mirror of Sketch"  # WARN: FeaturePython — macro-defined, semantics opaque (R4)
  ExposePlacement = false
  FlipX = true
  FlipY = false
  FlipZ = false
  MarkerShape = 1
  MarkerSize = 0
  NumElements = 0
  Object = -> Mirror001
  ObjectTraversal = 0
  Type = lattice2Mirror.LatticeMirror
  isLattice = 0
FEATURE [PartDesign::SubShapeBinder] Binder
  BindCopyOnChange = 0
  BindMode = 0
  ClaimChildren = true
  Context = -> Part [Body.Binder.]
  Fuse = false
  MakeFace = true
  OffsetFill = false
  OffsetIntersection = false
  OffsetJoinType = 0
  OffsetOpenResult = false
  PartialLoad = false
  Relative = true
  Support = -> [Connect]
  _Version = 2
FEATURE [PartDesign::Pad] Pad
  Direction = (0,0,1)
  Length = 2.45
  Length2 = 10
  Profile = -> Binder
  Suppressed = false
  Type = 0
FEATURE [PartDesign::Revolution] Revolution
  Angle = 360
  Angle2 = 60
  Axis = (0,2e-16,1)
  Base = (0,0,0)
  BaseFeature = -> Pad
  Profile = -> Sketch001
  ReferenceAxis = -> Sketch001 [V_Axis]
  Reversed = true
  Suppressed = false
  Type = 0
FEATURE [PartDesign::Pocket] Pocket
  BaseFeature = -> Revolution
  Direction = (-1,0,0)
  Length = 5
  Length2 = 5
  Midplane = true
  Profile = -> Sketch002
  ReferenceAxis = -> Sketch002 [N_Axis]
  Suppressed = false
  Type = 1
FEATURE [PartDesign::Revolution] Revolution001
  Angle = 360
  Angle2 = 60
  Axis = (0,0,1)
  Base = (0,0,0)
  BaseFeature = -> Pocket
  Profile = -> Sketch003
  ReferenceAxis = -> Sketch003 [V_Axis]
  Reversed = true
  Suppressed = false
  Type = 0
FEATURE [PartDesign::Groove] Groove
  Angle = 360
  Angle2 = 60
  Axis = (0,0,1)
  Base = (0,0,0)
  BaseFeature = -> Revolution001
  Profile = -> Sketch004
  ReferenceAxis = -> Sketch004 [V_Axis]
  Suppressed = false
  Type = 0
FEATURE [Sketcher::SketchObject] Sketch008  label="feed"
  ArcFitTolerance = 0
  AttachmentSupport = -> [XY_Plane]
  FullyConstrained = true
  MakeInternals = false
  MapMode = 5
  sketch-geometry (1):
    g0: Circle CenterX=0 CenterY=0 CenterZ=0 NormalX=0 NormalY=0 NormalZ=1 AngleXU=0 Radius=4
  constraints (2):
    c: Coincident(g0,g-1)
    c: Diameter(g0) = 8
FEATURE [PartDesign::Body] Body
  AllowCompound = false
  Group = -> [Sketch,Pad,Sketch001,Revolution,Sketch002,Pocket,Sketch003,Sketch004,Revolution001,Groove,Sketch008,Binder]
  Origin = -> Origin
  Tip = -> Groove
FEATURE [App::Part] Part  label="dropper"
  Group = -> [LCS_0,Body001,Body]
  Origin = -> Origin002
FEATURE [Part::FeaturePython] Connect  label="fix"  # WARN: FeaturePython — macro-defined, semantics opaque (R4)
  Objects = -> [Sketch,Mirror002,Mirror001,Mirror]
  Tolerance = 0
---- part module.FCStd = doc fcstd_3955753b3a20 ----
FCSTD DOCUMENT  (FreeCAD 1.1R38827 (Git))
Label: module
License: All rights reserved
LicenseURL: http://en.wikipedia.org/wiki/All_rights_reserved
objects: Sketcher::SketchObject×2, Part::Feature×1, PartDesign::FeatureBase×1, PartDesign::Body×1, Spreadsheet::Sheet×1
note: 8 computed .brp shape members not serialized (recipe doc carries the construction recipe); baked Part::Feature solids carry a one-line shape summary decoded from their .brp

FEATURE [Part::Feature] Part__Feature  label="module002"
  shape: bbox 170 x 148 x 41.12 mm, 715 faces (baked)
FEATURE [Sketcher::SketchObject] Sketch  label="module_holes"
  ArcFitTolerance = 0
  FullyConstrained = true
  MakeInternals = false
  sketch-geometry (10):
    g0: LineSegment StartX=59.5 StartY=-3.5 StartZ=0 EndX=59.5 EndY=3.5 EndZ=0
    g1: LineSegment StartX=59.5 StartY=3.5 StartZ=0 EndX=72.5 EndY=3.5 EndZ=0
    g2: LineSegment StartX=72.5 StartY=3.5 StartZ=0 EndX=72.5 EndY=-3.5 EndZ=0
    g3: LineSegment StartX=72.5 StartY=-3.5 StartZ=0 EndX=59.5 EndY=-3.5 EndZ=0
    g4: GeomPoint [constr] X=66 Y=0 Z=0
    g5: LineSegment StartX=-72.5 StartY=-3.5 StartZ=0 EndX=-72.5 EndY=3.5 EndZ=0
    g6: LineSegment StartX=-72.5 StartY=3.5 StartZ=0 EndX=-59.5 EndY=3.5 EndZ=0
    g7: LineSegment StartX=-59.5 StartY=3.5 StartZ=0 EndX=-59.5 EndY=-3.5 EndZ=0
    g8: LineSegment StartX=-59.5 StartY=-3.5 StartZ=0 EndX=-72.5 EndY=-3.5 EndZ=0
    g9: GeomPoint [constr] X=-66 Y=0 Z=0
  constraints (25):
    c: Coincident(g0,g1)
    c: Coincident(g1,g2)
    c: Coincident(g2,g3)
    c: Coincident(g3,g0)
    c: Horizontal(g1)
    c: Horizontal(g3)
    c: Vertical(g0)
    c: Vertical(g2)
    c: Symmetric(g1,g0,g4)
    c: PointOnObject(g4,g-1)
    c: Coincident(g5,g6)
    c: Coincident(g6,g7)
    c: Coincident(g7,g8)
    c: Coincident(g8,g5)
    c: Horizontal(g6)
    c: Horizontal(g8)
    c: Vertical(g5)
    c: Vertical(g7)
    c: Symmetric(g6,g5,g9)
    c: Symmetric(g9,g4,g-2)
    c: Equal(g1,g6)
    c: Equal(g7,g2)
    c: DistanceX(g1,g1) = 13
    c: DistanceY(g2,g2) = 7
    c: DistanceX(g9,g4) = 132
FEATURE [PartDesign::FeatureBase] BaseFeature
  BaseFeature = -> Part__Feature
  Placement = pos=(0,0,0) rot=(0,0,1;1.5708rad)
  Suppressed = false
FEATURE [PartDesign::Body] Body  label="module_Body"
  AllowCompound = false
  BaseFeature = -> Part__Feature
  Group = -> [BaseFeature]
  Origin = -> Origin
  Tip = -> BaseFeature
FEATURE [Spreadsheet::Sheet] Spreadsheet  label="Properties"
  cells = B2(module_width)==148 mm; C2(module_height)==160 mm; D2(module_fixture_distance_x)==132 mm; E2(module_fixture_distance_y)==80 mm; F2(module_hole_x)==13 mm; G2(module_hole_y)==7 mm
FEATURE [Sketcher::SketchObject] Sketch001  label="module_holes001"
  ArcFitTolerance = 0
  FullyConstrained = true
  MakeInternals = false
  sketch-geometry (10):
    g0: LineSegment StartX=59 StartY=-3.5 StartZ=0 EndX=59 EndY=3.5 EndZ=0
    g1: LineSegment StartX=59 StartY=3.5 StartZ=0 EndX=73 EndY=3.5 EndZ=0
    g2: LineSegment StartX=73 StartY=3.5 StartZ=0 EndX=73 EndY=-3.5 EndZ=0
    g3: LineSegment StartX=73 StartY=-3.5 StartZ=0 EndX=59 EndY=-3.5 EndZ=0
    g4: GeomPoint [constr] X=66 Y=0 Z=0
    g5: LineSegment StartX=-73 StartY=-3.5 StartZ=0 EndX=-73 EndY=3.5 EndZ=0
    g6: LineSegment StartX=-73 StartY=3.5 StartZ=0 EndX=-59 EndY=3.5 EndZ=0
    g7: LineSegment StartX=-59 StartY=3.5 StartZ=0 EndX=-59 EndY=-3.5 EndZ=0
    g8: LineSegment StartX=-59 StartY=-3.5 StartZ=0 EndX=-73 EndY=-3.5 EndZ=0
    g9: GeomPoint [constr] X=-66 Y=0 Z=0
  constraints (25):
    c: Coincident(g0,g1)
    c: Coincident(g1,g2)
    c: Coincident(g2,g3)
    c: Coincident(g3,g0)
    c: Horizontal(g1)
    c: Horizontal(g3)
    c: Vertical(g0)
    c: Vertical(g2)
    c: Symmetric(g1,g0,g4)
    c: PointOnObject(g4,g-1)
    c: Coincident(g5,g6)
    c: Coincident(g6,g7)
    c: Coincident(g7,g8)
    c: Coincident(g8,g5)
    c: Horizontal(g6)
    c: Horizontal(g8)
    c: Vertical(g5)
    c: Vertical(g7)
    c: Symmetric(g6,g5,g9)
    c: Symmetric(g9,g4,g-2)
    c: Equal(g1,g6)
    c: Equal(g7,g2)
    c: DistanceX(g1,g1) = 14
    c: DistanceY(g2,g2) = 7
    c: DistanceX(g9,g4) = 132
